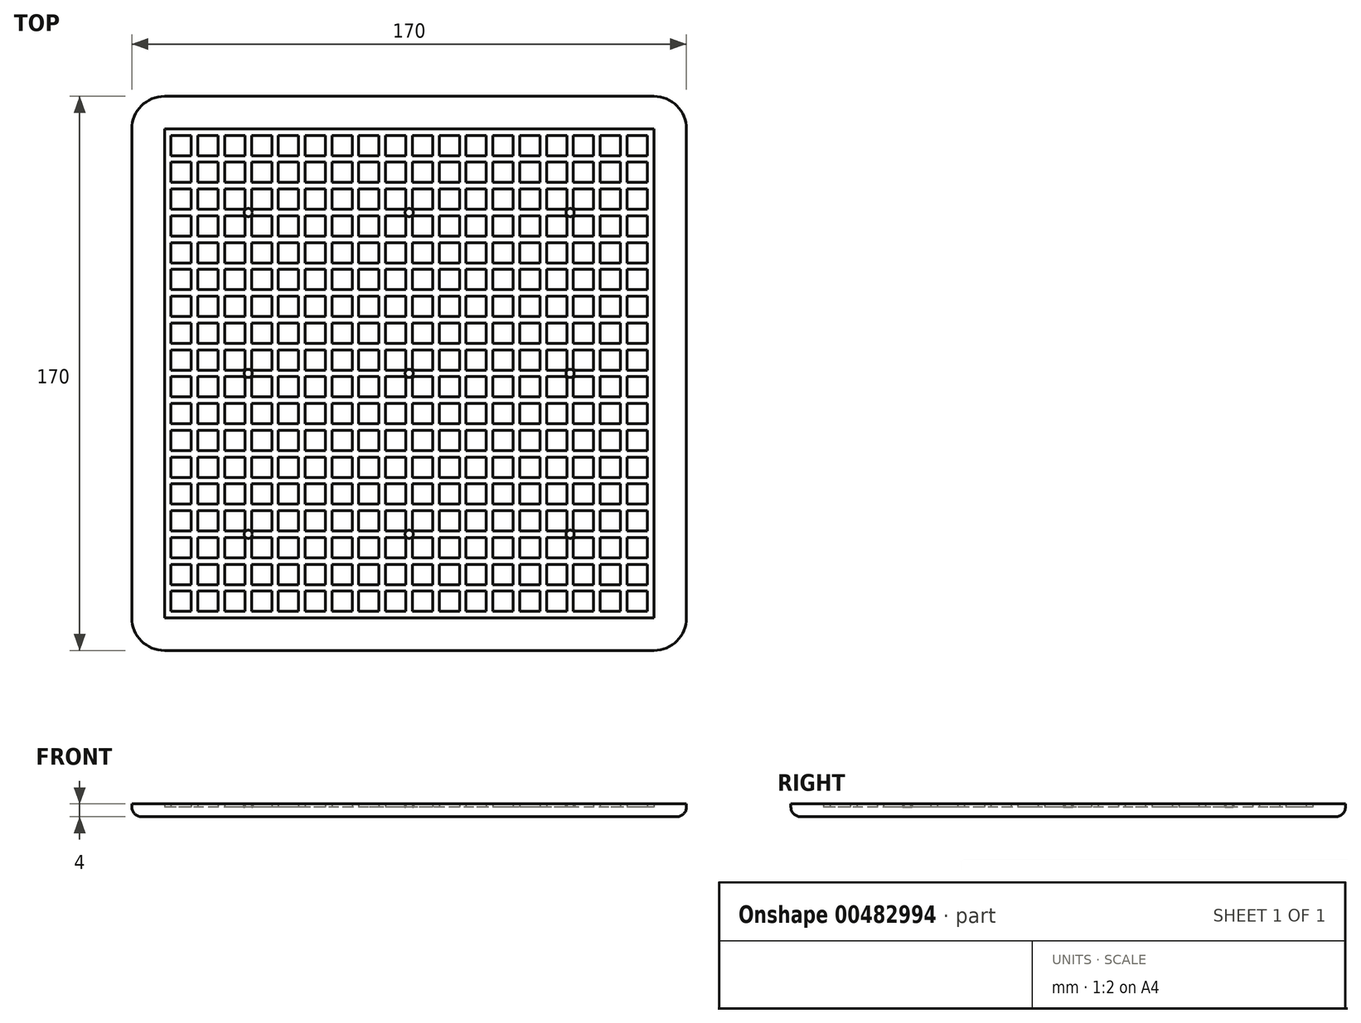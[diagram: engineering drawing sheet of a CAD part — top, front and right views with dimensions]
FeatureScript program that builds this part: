
annotation { "Feature Type Name" : "Feature", "Feature Type Description" : "" }
export const myFeature = defineFeature(function(context is Context, id is Id, definition is map)
    precondition{}
    {
        {
            var Q0;
            Q0=qCreatedBy(makeId("Top.planeOp"),FACE);
            var sketch = newSketch(context, id + "F0", { "sketchPlane" : qUnion([Q0])});
            skLineSegment(sketch, "E0.bottom", {"start": v(85, 85) * mm, "end": v(-85, 85) * mm});
            skLineSegment(sketch, "E0.top", {"start": v(85, -85) * mm, "end": v(-85, -85) * mm});
            skLineSegment(sketch, "E0.left", {"start": v(85, 85) * mm, "end": v(85, -85) * mm});
            skLineSegment(sketch, "E0.right", {"start": v(-85, 85) * mm, "end": v(-85, -85) * mm});
            skPoint(sketch, "E0.middle", {"position": v(0, 0) * mm});
            skSolve(sketch);
        }
        {
            var Q0;
            Q0=makeQuery(id+"F0.imprint","IMPRINT",FACE,{"disambiguationData":[TD([[makeQuery(id+"F0.imprint","IMPRINT",EDGE,{"derivedFrom":sQuery(id+"F0.wireOp",EDGE,"E0.bottom")}),1.0]])]});
            extrude(context, id + "F1", {"entities" : qUnion([Q0]), "depth" : 3 * mm});
        }
        {
            var Q0;
            Q0=makeQuery(id+"F1.opExtrude","CAP_FACE",FACE,{"disambiguationData":[OSD([sQuery(id+"F0.wireOp",EDGE,"E0.bottom"),sQuery(id+"F0.wireOp",EDGE,"E0.top"),sQuery(id+"F0.wireOp",EDGE,"E0.left"),sQuery(id+"F0.wireOp",EDGE,"E0.right")])],"isStart":false});
            var sketch = newSketch(context, id + "F2", { "sketchPlane" : qUnion([Q0])});
            skLineSegment(sketch, "E1.bottom", {"start": v(75, 75) * mm, "end": v(-75, 75) * mm});
            skLineSegment(sketch, "E1.top", {"start": v(75, -75) * mm, "end": v(-75, -75) * mm});
            skLineSegment(sketch, "E1.left", {"start": v(75, 75) * mm, "end": v(75, -75) * mm});
            skLineSegment(sketch, "E1.right", {"start": v(-75, 75) * mm, "end": v(-75, -75) * mm});
            skPoint(sketch, "E1.middle", {"position": v(0, 0) * mm});
            skSolve(sketch);
        }
        {
            var Q0;
            Q0=makeQuery(id+"F2.imprint","IMPRINT",FACE,{"disambiguationData":[TD([[makeQuery(id+"F2.imprint","IMPRINT",EDGE,{"derivedFrom":sQuery(id+"F2.wireOp",EDGE,"E1.bottom")}),-1.0]])]});
            extrude(context, id + "F3", {"entities" : qUnion([Q0]), "operationType" : NewBodyOperationType.ADD, "depth" : 1 * mm});
        }
        {
            var Q0;
            Q0=makeQuery(id+"F1.opExtrude","CAP_FACE",FACE,{"disambiguationData":[OSD([sQuery(id+"F0.wireOp",EDGE,"E0.bottom"),sQuery(id+"F0.wireOp",EDGE,"E0.top"),sQuery(id+"F0.wireOp",EDGE,"E0.left"),sQuery(id+"F0.wireOp",EDGE,"E0.right")])],"isStart":false});
            var sketch = newSketch(context, id + "F4", { "sketchPlane" : qUnion([Q0])});
            skLineSegment(sketch, "E2.bottom", {"start": v(-66.78, 73) * mm, "end": v(-73, 73) * mm});
            skLineSegment(sketch, "E2.top", {"start": v(-66.78, 66.78) * mm, "end": v(-73, 66.78) * mm});
            skLineSegment(sketch, "E2.left", {"start": v(-66.78, 73) * mm, "end": v(-66.78, 66.78) * mm});
            skLineSegment(sketch, "E2.right", {"start": v(-73, 73) * mm, "end": v(-73, 66.78) * mm});
            skPoint(sketch, "E2.middle", {"position": v(-69.89, 69.89) * mm});
            skLineSegment(sketch, "E3.0.1.0", {"start": v(-73, 64.78) * mm, "end": v(-73, 58.56) * mm});
            skLineSegment(sketch, "E3.0.1.1", {"start": v(-66.78, 58.56) * mm, "end": v(-73, 58.56) * mm});
            skLineSegment(sketch, "E3.0.1.2", {"start": v(-66.78, 64.78) * mm, "end": v(-66.78, 58.56) * mm});
            skLineSegment(sketch, "E3.0.1.3", {"start": v(-66.78, 64.78) * mm, "end": v(-73, 64.78) * mm});
            skLineSegment(sketch, "E3.0.2.0", {"start": v(-73, 56.56) * mm, "end": v(-73, 50.33) * mm});
            skLineSegment(sketch, "E3.0.2.1", {"start": v(-66.78, 50.33) * mm, "end": v(-73, 50.33) * mm});
            skLineSegment(sketch, "E3.0.2.2", {"start": v(-66.78, 56.56) * mm, "end": v(-66.78, 50.33) * mm});
            skLineSegment(sketch, "E3.0.2.3", {"start": v(-66.78, 56.56) * mm, "end": v(-73, 56.56) * mm});
            skLineSegment(sketch, "E3.0.3.0", {"start": v(-73, 48.33) * mm, "end": v(-73, 42.11) * mm});
            skLineSegment(sketch, "E3.0.3.1", {"start": v(-66.78, 42.11) * mm, "end": v(-73, 42.11) * mm});
            skLineSegment(sketch, "E3.0.3.2", {"start": v(-66.78, 48.33) * mm, "end": v(-66.78, 42.11) * mm});
            skLineSegment(sketch, "E3.0.3.3", {"start": v(-66.78, 48.33) * mm, "end": v(-73, 48.33) * mm});
            skLineSegment(sketch, "E3.0.4.0", {"start": v(-73, 40.11) * mm, "end": v(-73, 33.89) * mm});
            skLineSegment(sketch, "E3.0.4.1", {"start": v(-66.78, 33.89) * mm, "end": v(-73, 33.89) * mm});
            skLineSegment(sketch, "E3.0.4.2", {"start": v(-66.78, 40.11) * mm, "end": v(-66.78, 33.89) * mm});
            skLineSegment(sketch, "E3.0.4.3", {"start": v(-66.78, 40.11) * mm, "end": v(-73, 40.11) * mm});
            skLineSegment(sketch, "E3.0.5.0", {"start": v(-73, 31.89) * mm, "end": v(-73, 25.67) * mm});
            skLineSegment(sketch, "E3.0.5.1", {"start": v(-66.78, 25.67) * mm, "end": v(-73, 25.67) * mm});
            skLineSegment(sketch, "E3.0.5.2", {"start": v(-66.78, 31.89) * mm, "end": v(-66.78, 25.67) * mm});
            skLineSegment(sketch, "E3.0.5.3", {"start": v(-66.78, 31.89) * mm, "end": v(-73, 31.89) * mm});
            skLineSegment(sketch, "E3.0.6.0", {"start": v(-73, 23.67) * mm, "end": v(-73, 17.44) * mm});
            skLineSegment(sketch, "E3.0.6.1", {"start": v(-66.78, 17.44) * mm, "end": v(-73, 17.44) * mm});
            skLineSegment(sketch, "E3.0.6.2", {"start": v(-66.78, 23.67) * mm, "end": v(-66.78, 17.44) * mm});
            skLineSegment(sketch, "E3.0.6.3", {"start": v(-66.78, 23.67) * mm, "end": v(-73, 23.67) * mm});
            skLineSegment(sketch, "E3.0.7.0", {"start": v(-73, 15.44) * mm, "end": v(-73, 9.22) * mm});
            skLineSegment(sketch, "E3.0.7.1", {"start": v(-66.78, 9.22) * mm, "end": v(-73, 9.22) * mm});
            skLineSegment(sketch, "E3.0.7.2", {"start": v(-66.78, 15.44) * mm, "end": v(-66.78, 9.22) * mm});
            skLineSegment(sketch, "E3.0.7.3", {"start": v(-66.78, 15.44) * mm, "end": v(-73, 15.44) * mm});
            skLineSegment(sketch, "E3.0.8.0", {"start": v(-73, 7.22) * mm, "end": v(-73, 1) * mm});
            skLineSegment(sketch, "E3.0.8.1", {"start": v(-66.78, 1) * mm, "end": v(-73, 1) * mm});
            skLineSegment(sketch, "E3.0.8.2", {"start": v(-66.78, 7.22) * mm, "end": v(-66.78, 1) * mm});
            skLineSegment(sketch, "E3.0.8.3", {"start": v(-66.78, 7.22) * mm, "end": v(-73, 7.22) * mm});
            skLineSegment(sketch, "E3.0.9.0", {"start": v(-73, -1) * mm, "end": v(-73, -7.22) * mm});
            skLineSegment(sketch, "E3.0.9.1", {"start": v(-66.78, -7.22) * mm, "end": v(-73, -7.22) * mm});
            skLineSegment(sketch, "E3.0.9.2", {"start": v(-66.78, -1) * mm, "end": v(-66.78, -7.22) * mm});
            skLineSegment(sketch, "E3.0.9.3", {"start": v(-66.78, -1) * mm, "end": v(-73, -1) * mm});
            skLineSegment(sketch, "E3.0.10.0", {"start": v(-73, -9.22) * mm, "end": v(-73, -15.44) * mm});
            skLineSegment(sketch, "E3.0.10.1", {"start": v(-66.78, -15.44) * mm, "end": v(-73, -15.44) * mm});
            skLineSegment(sketch, "E3.0.10.2", {"start": v(-66.78, -9.22) * mm, "end": v(-66.78, -15.44) * mm});
            skLineSegment(sketch, "E3.0.10.3", {"start": v(-66.78, -9.22) * mm, "end": v(-73, -9.22) * mm});
            skLineSegment(sketch, "E3.0.11.0", {"start": v(-73, -17.44) * mm, "end": v(-73, -23.67) * mm});
            skLineSegment(sketch, "E3.0.11.1", {"start": v(-66.78, -23.67) * mm, "end": v(-73, -23.67) * mm});
            skLineSegment(sketch, "E3.0.11.2", {"start": v(-66.78, -17.44) * mm, "end": v(-66.78, -23.67) * mm});
            skLineSegment(sketch, "E3.0.11.3", {"start": v(-66.78, -17.44) * mm, "end": v(-73, -17.44) * mm});
            skLineSegment(sketch, "E3.0.12.0", {"start": v(-73, -25.67) * mm, "end": v(-73, -31.89) * mm});
            skLineSegment(sketch, "E3.0.12.1", {"start": v(-66.78, -31.89) * mm, "end": v(-73, -31.89) * mm});
            skLineSegment(sketch, "E3.0.12.2", {"start": v(-66.78, -25.67) * mm, "end": v(-66.78, -31.89) * mm});
            skLineSegment(sketch, "E3.0.12.3", {"start": v(-66.78, -25.67) * mm, "end": v(-73, -25.67) * mm});
            skLineSegment(sketch, "E3.0.13.0", {"start": v(-73, -33.89) * mm, "end": v(-73, -40.11) * mm});
            skLineSegment(sketch, "E3.0.13.1", {"start": v(-66.78, -40.11) * mm, "end": v(-73, -40.11) * mm});
            skLineSegment(sketch, "E3.0.13.2", {"start": v(-66.78, -33.89) * mm, "end": v(-66.78, -40.11) * mm});
            skLineSegment(sketch, "E3.0.13.3", {"start": v(-66.78, -33.89) * mm, "end": v(-73, -33.89) * mm});
            skLineSegment(sketch, "E3.0.14.0", {"start": v(-73, -42.11) * mm, "end": v(-73, -48.33) * mm});
            skLineSegment(sketch, "E3.0.14.1", {"start": v(-66.78, -48.33) * mm, "end": v(-73, -48.33) * mm});
            skLineSegment(sketch, "E3.0.14.2", {"start": v(-66.78, -42.11) * mm, "end": v(-66.78, -48.33) * mm});
            skLineSegment(sketch, "E3.0.14.3", {"start": v(-66.78, -42.11) * mm, "end": v(-73, -42.11) * mm});
            skLineSegment(sketch, "E3.0.15.0", {"start": v(-73, -50.33) * mm, "end": v(-73, -56.56) * mm});
            skLineSegment(sketch, "E3.0.15.1", {"start": v(-66.78, -56.56) * mm, "end": v(-73, -56.56) * mm});
            skLineSegment(sketch, "E3.0.15.2", {"start": v(-66.78, -50.33) * mm, "end": v(-66.78, -56.56) * mm});
            skLineSegment(sketch, "E3.0.15.3", {"start": v(-66.78, -50.33) * mm, "end": v(-73, -50.33) * mm});
            skLineSegment(sketch, "E3.0.16.0", {"start": v(-73, -58.56) * mm, "end": v(-73, -64.78) * mm});
            skLineSegment(sketch, "E3.0.16.1", {"start": v(-66.78, -64.78) * mm, "end": v(-73, -64.78) * mm});
            skLineSegment(sketch, "E3.0.16.2", {"start": v(-66.78, -58.56) * mm, "end": v(-66.78, -64.78) * mm});
            skLineSegment(sketch, "E3.0.16.3", {"start": v(-66.78, -58.56) * mm, "end": v(-73, -58.56) * mm});
            skLineSegment(sketch, "E3.0.17.0", {"start": v(-73, -66.78) * mm, "end": v(-73, -73) * mm});
            skLineSegment(sketch, "E3.0.17.1", {"start": v(-66.78, -73) * mm, "end": v(-73, -73) * mm});
            skLineSegment(sketch, "E3.0.17.2", {"start": v(-66.78, -66.78) * mm, "end": v(-66.78, -73) * mm});
            skLineSegment(sketch, "E3.0.17.3", {"start": v(-66.78, -66.78) * mm, "end": v(-73, -66.78) * mm});
            skLineSegment(sketch, "E3.1.0.0", {"start": v(-64.78, 73) * mm, "end": v(-64.78, 66.78) * mm});
            skLineSegment(sketch, "E3.1.0.1", {"start": v(-58.56, 66.78) * mm, "end": v(-64.78, 66.78) * mm});
            skLineSegment(sketch, "E3.1.0.2", {"start": v(-58.56, 73) * mm, "end": v(-58.56, 66.78) * mm});
            skLineSegment(sketch, "E3.1.0.3", {"start": v(-58.56, 73) * mm, "end": v(-64.78, 73) * mm});
            skLineSegment(sketch, "E3.1.1.0", {"start": v(-64.78, 64.78) * mm, "end": v(-64.78, 58.56) * mm});
            skLineSegment(sketch, "E3.1.1.1", {"start": v(-58.56, 58.56) * mm, "end": v(-64.78, 58.56) * mm});
            skLineSegment(sketch, "E3.1.1.2", {"start": v(-58.56, 64.78) * mm, "end": v(-58.56, 58.56) * mm});
            skLineSegment(sketch, "E3.1.1.3", {"start": v(-58.56, 64.78) * mm, "end": v(-64.78, 64.78) * mm});
            skLineSegment(sketch, "E3.1.2.0", {"start": v(-64.78, 56.56) * mm, "end": v(-64.78, 50.33) * mm});
            skLineSegment(sketch, "E3.1.2.1", {"start": v(-58.56, 50.33) * mm, "end": v(-64.78, 50.33) * mm});
            skLineSegment(sketch, "E3.1.2.2", {"start": v(-58.56, 56.56) * mm, "end": v(-58.56, 50.33) * mm});
            skLineSegment(sketch, "E3.1.2.3", {"start": v(-58.56, 56.56) * mm, "end": v(-64.78, 56.56) * mm});
            skLineSegment(sketch, "E3.1.3.0", {"start": v(-64.78, 48.33) * mm, "end": v(-64.78, 42.11) * mm});
            skLineSegment(sketch, "E3.1.3.1", {"start": v(-58.56, 42.11) * mm, "end": v(-64.78, 42.11) * mm});
            skLineSegment(sketch, "E3.1.3.2", {"start": v(-58.56, 48.33) * mm, "end": v(-58.56, 42.11) * mm});
            skLineSegment(sketch, "E3.1.3.3", {"start": v(-58.56, 48.33) * mm, "end": v(-64.78, 48.33) * mm});
            skLineSegment(sketch, "E3.1.4.0", {"start": v(-64.78, 40.11) * mm, "end": v(-64.78, 33.89) * mm});
            skLineSegment(sketch, "E3.1.4.1", {"start": v(-58.56, 33.89) * mm, "end": v(-64.78, 33.89) * mm});
            skLineSegment(sketch, "E3.1.4.2", {"start": v(-58.56, 40.11) * mm, "end": v(-58.56, 33.89) * mm});
            skLineSegment(sketch, "E3.1.4.3", {"start": v(-58.56, 40.11) * mm, "end": v(-64.78, 40.11) * mm});
            skLineSegment(sketch, "E3.1.5.0", {"start": v(-64.78, 31.89) * mm, "end": v(-64.78, 25.67) * mm});
            skLineSegment(sketch, "E3.1.5.1", {"start": v(-58.56, 25.67) * mm, "end": v(-64.78, 25.67) * mm});
            skLineSegment(sketch, "E3.1.5.2", {"start": v(-58.56, 31.89) * mm, "end": v(-58.56, 25.67) * mm});
            skLineSegment(sketch, "E3.1.5.3", {"start": v(-58.56, 31.89) * mm, "end": v(-64.78, 31.89) * mm});
            skLineSegment(sketch, "E3.1.6.0", {"start": v(-64.78, 23.67) * mm, "end": v(-64.78, 17.44) * mm});
            skLineSegment(sketch, "E3.1.6.1", {"start": v(-58.56, 17.44) * mm, "end": v(-64.78, 17.44) * mm});
            skLineSegment(sketch, "E3.1.6.2", {"start": v(-58.56, 23.67) * mm, "end": v(-58.56, 17.44) * mm});
            skLineSegment(sketch, "E3.1.6.3", {"start": v(-58.56, 23.67) * mm, "end": v(-64.78, 23.67) * mm});
            skLineSegment(sketch, "E3.1.7.0", {"start": v(-64.78, 15.44) * mm, "end": v(-64.78, 9.22) * mm});
            skLineSegment(sketch, "E3.1.7.1", {"start": v(-58.56, 9.22) * mm, "end": v(-64.78, 9.22) * mm});
            skLineSegment(sketch, "E3.1.7.2", {"start": v(-58.56, 15.44) * mm, "end": v(-58.56, 9.22) * mm});
            skLineSegment(sketch, "E3.1.7.3", {"start": v(-58.56, 15.44) * mm, "end": v(-64.78, 15.44) * mm});
            skLineSegment(sketch, "E3.1.8.0", {"start": v(-64.78, 7.22) * mm, "end": v(-64.78, 1) * mm});
            skLineSegment(sketch, "E3.1.8.1", {"start": v(-58.56, 1) * mm, "end": v(-64.78, 1) * mm});
            skLineSegment(sketch, "E3.1.8.2", {"start": v(-58.56, 7.22) * mm, "end": v(-58.56, 1) * mm});
            skLineSegment(sketch, "E3.1.8.3", {"start": v(-58.56, 7.22) * mm, "end": v(-64.78, 7.22) * mm});
            skLineSegment(sketch, "E3.1.9.0", {"start": v(-64.78, -1) * mm, "end": v(-64.78, -7.22) * mm});
            skLineSegment(sketch, "E3.1.9.1", {"start": v(-58.56, -7.22) * mm, "end": v(-64.78, -7.22) * mm});
            skLineSegment(sketch, "E3.1.9.2", {"start": v(-58.56, -1) * mm, "end": v(-58.56, -7.22) * mm});
            skLineSegment(sketch, "E3.1.9.3", {"start": v(-58.56, -1) * mm, "end": v(-64.78, -1) * mm});
            skLineSegment(sketch, "E3.1.10.0", {"start": v(-64.78, -9.22) * mm, "end": v(-64.78, -15.44) * mm});
            skLineSegment(sketch, "E3.1.10.1", {"start": v(-58.56, -15.44) * mm, "end": v(-64.78, -15.44) * mm});
            skLineSegment(sketch, "E3.1.10.2", {"start": v(-58.56, -9.22) * mm, "end": v(-58.56, -15.44) * mm});
            skLineSegment(sketch, "E3.1.10.3", {"start": v(-58.56, -9.22) * mm, "end": v(-64.78, -9.22) * mm});
            skLineSegment(sketch, "E3.1.11.0", {"start": v(-64.78, -17.44) * mm, "end": v(-64.78, -23.67) * mm});
            skLineSegment(sketch, "E3.1.11.1", {"start": v(-58.56, -23.67) * mm, "end": v(-64.78, -23.67) * mm});
            skLineSegment(sketch, "E3.1.11.2", {"start": v(-58.56, -17.44) * mm, "end": v(-58.56, -23.67) * mm});
            skLineSegment(sketch, "E3.1.11.3", {"start": v(-58.56, -17.44) * mm, "end": v(-64.78, -17.44) * mm});
            skLineSegment(sketch, "E3.1.12.0", {"start": v(-64.78, -25.67) * mm, "end": v(-64.78, -31.89) * mm});
            skLineSegment(sketch, "E3.1.12.1", {"start": v(-58.56, -31.89) * mm, "end": v(-64.78, -31.89) * mm});
            skLineSegment(sketch, "E3.1.12.2", {"start": v(-58.56, -25.67) * mm, "end": v(-58.56, -31.89) * mm});
            skLineSegment(sketch, "E3.1.12.3", {"start": v(-58.56, -25.67) * mm, "end": v(-64.78, -25.67) * mm});
            skLineSegment(sketch, "E3.1.13.0", {"start": v(-64.78, -33.89) * mm, "end": v(-64.78, -40.11) * mm});
            skLineSegment(sketch, "E3.1.13.1", {"start": v(-58.56, -40.11) * mm, "end": v(-64.78, -40.11) * mm});
            skLineSegment(sketch, "E3.1.13.2", {"start": v(-58.56, -33.89) * mm, "end": v(-58.56, -40.11) * mm});
            skLineSegment(sketch, "E3.1.13.3", {"start": v(-58.56, -33.89) * mm, "end": v(-64.78, -33.89) * mm});
            skLineSegment(sketch, "E3.1.14.0", {"start": v(-64.78, -42.11) * mm, "end": v(-64.78, -48.33) * mm});
            skLineSegment(sketch, "E3.1.14.1", {"start": v(-58.56, -48.33) * mm, "end": v(-64.78, -48.33) * mm});
            skLineSegment(sketch, "E3.1.14.2", {"start": v(-58.56, -42.11) * mm, "end": v(-58.56, -48.33) * mm});
            skLineSegment(sketch, "E3.1.14.3", {"start": v(-58.56, -42.11) * mm, "end": v(-64.78, -42.11) * mm});
            skLineSegment(sketch, "E3.1.15.0", {"start": v(-64.78, -50.33) * mm, "end": v(-64.78, -56.56) * mm});
            skLineSegment(sketch, "E3.1.15.1", {"start": v(-58.56, -56.56) * mm, "end": v(-64.78, -56.56) * mm});
            skLineSegment(sketch, "E3.1.15.2", {"start": v(-58.56, -50.33) * mm, "end": v(-58.56, -56.56) * mm});
            skLineSegment(sketch, "E3.1.15.3", {"start": v(-58.56, -50.33) * mm, "end": v(-64.78, -50.33) * mm});
            skLineSegment(sketch, "E3.1.16.0", {"start": v(-64.78, -58.56) * mm, "end": v(-64.78, -64.78) * mm});
            skLineSegment(sketch, "E3.1.16.1", {"start": v(-58.56, -64.78) * mm, "end": v(-64.78, -64.78) * mm});
            skLineSegment(sketch, "E3.1.16.2", {"start": v(-58.56, -58.56) * mm, "end": v(-58.56, -64.78) * mm});
            skLineSegment(sketch, "E3.1.16.3", {"start": v(-58.56, -58.56) * mm, "end": v(-64.78, -58.56) * mm});
            skLineSegment(sketch, "E3.1.17.0", {"start": v(-64.78, -66.78) * mm, "end": v(-64.78, -73) * mm});
            skLineSegment(sketch, "E3.1.17.1", {"start": v(-58.56, -73) * mm, "end": v(-64.78, -73) * mm});
            skLineSegment(sketch, "E3.1.17.2", {"start": v(-58.56, -66.78) * mm, "end": v(-58.56, -73) * mm});
            skLineSegment(sketch, "E3.1.17.3", {"start": v(-58.56, -66.78) * mm, "end": v(-64.78, -66.78) * mm});
            skLineSegment(sketch, "E3.2.0.0", {"start": v(-56.56, 73) * mm, "end": v(-56.56, 66.78) * mm});
            skLineSegment(sketch, "E3.2.0.1", {"start": v(-50.33, 66.78) * mm, "end": v(-56.56, 66.78) * mm});
            skLineSegment(sketch, "E3.2.0.2", {"start": v(-50.33, 73) * mm, "end": v(-50.33, 66.78) * mm});
            skLineSegment(sketch, "E3.2.0.3", {"start": v(-50.33, 73) * mm, "end": v(-56.56, 73) * mm});
            skLineSegment(sketch, "E3.2.1.0", {"start": v(-56.56, 64.78) * mm, "end": v(-56.56, 58.56) * mm});
            skLineSegment(sketch, "E3.2.1.1", {"start": v(-50.33, 58.56) * mm, "end": v(-56.56, 58.56) * mm});
            skLineSegment(sketch, "E3.2.1.2", {"start": v(-50.33, 64.78) * mm, "end": v(-50.33, 58.56) * mm});
            skLineSegment(sketch, "E3.2.1.3", {"start": v(-50.33, 64.78) * mm, "end": v(-56.56, 64.78) * mm});
            skLineSegment(sketch, "E3.2.2.0", {"start": v(-56.56, 56.56) * mm, "end": v(-56.56, 50.33) * mm});
            skLineSegment(sketch, "E3.2.2.1", {"start": v(-50.33, 50.33) * mm, "end": v(-56.56, 50.33) * mm});
            skLineSegment(sketch, "E3.2.2.2", {"start": v(-50.33, 56.56) * mm, "end": v(-50.33, 50.33) * mm});
            skLineSegment(sketch, "E3.2.2.3", {"start": v(-50.33, 56.56) * mm, "end": v(-56.56, 56.56) * mm});
            skLineSegment(sketch, "E3.2.3.0", {"start": v(-56.56, 48.33) * mm, "end": v(-56.56, 42.11) * mm});
            skLineSegment(sketch, "E3.2.3.1", {"start": v(-50.33, 42.11) * mm, "end": v(-56.56, 42.11) * mm});
            skLineSegment(sketch, "E3.2.3.2", {"start": v(-50.33, 48.33) * mm, "end": v(-50.33, 42.11) * mm});
            skLineSegment(sketch, "E3.2.3.3", {"start": v(-50.33, 48.33) * mm, "end": v(-56.56, 48.33) * mm});
            skLineSegment(sketch, "E3.2.4.0", {"start": v(-56.56, 40.11) * mm, "end": v(-56.56, 33.89) * mm});
            skLineSegment(sketch, "E3.2.4.1", {"start": v(-50.33, 33.89) * mm, "end": v(-56.56, 33.89) * mm});
            skLineSegment(sketch, "E3.2.4.2", {"start": v(-50.33, 40.11) * mm, "end": v(-50.33, 33.89) * mm});
            skLineSegment(sketch, "E3.2.4.3", {"start": v(-50.33, 40.11) * mm, "end": v(-56.56, 40.11) * mm});
            skLineSegment(sketch, "E3.2.5.0", {"start": v(-56.56, 31.89) * mm, "end": v(-56.56, 25.67) * mm});
            skLineSegment(sketch, "E3.2.5.1", {"start": v(-50.33, 25.67) * mm, "end": v(-56.56, 25.67) * mm});
            skLineSegment(sketch, "E3.2.5.2", {"start": v(-50.33, 31.89) * mm, "end": v(-50.33, 25.67) * mm});
            skLineSegment(sketch, "E3.2.5.3", {"start": v(-50.33, 31.89) * mm, "end": v(-56.56, 31.89) * mm});
            skLineSegment(sketch, "E3.2.6.0", {"start": v(-56.56, 23.67) * mm, "end": v(-56.56, 17.44) * mm});
            skLineSegment(sketch, "E3.2.6.1", {"start": v(-50.33, 17.44) * mm, "end": v(-56.56, 17.44) * mm});
            skLineSegment(sketch, "E3.2.6.2", {"start": v(-50.33, 23.67) * mm, "end": v(-50.33, 17.44) * mm});
            skLineSegment(sketch, "E3.2.6.3", {"start": v(-50.33, 23.67) * mm, "end": v(-56.56, 23.67) * mm});
            skLineSegment(sketch, "E3.2.7.0", {"start": v(-56.56, 15.44) * mm, "end": v(-56.56, 9.22) * mm});
            skLineSegment(sketch, "E3.2.7.1", {"start": v(-50.33, 9.22) * mm, "end": v(-56.56, 9.22) * mm});
            skLineSegment(sketch, "E3.2.7.2", {"start": v(-50.33, 15.44) * mm, "end": v(-50.33, 9.22) * mm});
            skLineSegment(sketch, "E3.2.7.3", {"start": v(-50.33, 15.44) * mm, "end": v(-56.56, 15.44) * mm});
            skLineSegment(sketch, "E3.2.8.0", {"start": v(-56.56, 7.22) * mm, "end": v(-56.56, 1) * mm});
            skLineSegment(sketch, "E3.2.8.1", {"start": v(-50.33, 1) * mm, "end": v(-56.56, 1) * mm});
            skLineSegment(sketch, "E3.2.8.2", {"start": v(-50.33, 7.22) * mm, "end": v(-50.33, 1) * mm});
            skLineSegment(sketch, "E3.2.8.3", {"start": v(-50.33, 7.22) * mm, "end": v(-56.56, 7.22) * mm});
            skLineSegment(sketch, "E3.2.9.0", {"start": v(-56.56, -1) * mm, "end": v(-56.56, -7.22) * mm});
            skLineSegment(sketch, "E3.2.9.1", {"start": v(-50.33, -7.22) * mm, "end": v(-56.56, -7.22) * mm});
            skLineSegment(sketch, "E3.2.9.2", {"start": v(-50.33, -1) * mm, "end": v(-50.33, -7.22) * mm});
            skLineSegment(sketch, "E3.2.9.3", {"start": v(-50.33, -1) * mm, "end": v(-56.56, -1) * mm});
            skLineSegment(sketch, "E3.2.10.0", {"start": v(-56.56, -9.22) * mm, "end": v(-56.56, -15.44) * mm});
            skLineSegment(sketch, "E3.2.10.1", {"start": v(-50.33, -15.44) * mm, "end": v(-56.56, -15.44) * mm});
            skLineSegment(sketch, "E3.2.10.2", {"start": v(-50.33, -9.22) * mm, "end": v(-50.33, -15.44) * mm});
            skLineSegment(sketch, "E3.2.10.3", {"start": v(-50.33, -9.22) * mm, "end": v(-56.56, -9.22) * mm});
            skLineSegment(sketch, "E3.2.11.0", {"start": v(-56.56, -17.44) * mm, "end": v(-56.56, -23.67) * mm});
            skLineSegment(sketch, "E3.2.11.1", {"start": v(-50.33, -23.67) * mm, "end": v(-56.56, -23.67) * mm});
            skLineSegment(sketch, "E3.2.11.2", {"start": v(-50.33, -17.44) * mm, "end": v(-50.33, -23.67) * mm});
            skLineSegment(sketch, "E3.2.11.3", {"start": v(-50.33, -17.44) * mm, "end": v(-56.56, -17.44) * mm});
            skLineSegment(sketch, "E3.2.12.0", {"start": v(-56.56, -25.67) * mm, "end": v(-56.56, -31.89) * mm});
            skLineSegment(sketch, "E3.2.12.1", {"start": v(-50.33, -31.89) * mm, "end": v(-56.56, -31.89) * mm});
            skLineSegment(sketch, "E3.2.12.2", {"start": v(-50.33, -25.67) * mm, "end": v(-50.33, -31.89) * mm});
            skLineSegment(sketch, "E3.2.12.3", {"start": v(-50.33, -25.67) * mm, "end": v(-56.56, -25.67) * mm});
            skLineSegment(sketch, "E3.2.13.0", {"start": v(-56.56, -33.89) * mm, "end": v(-56.56, -40.11) * mm});
            skLineSegment(sketch, "E3.2.13.1", {"start": v(-50.33, -40.11) * mm, "end": v(-56.56, -40.11) * mm});
            skLineSegment(sketch, "E3.2.13.2", {"start": v(-50.33, -33.89) * mm, "end": v(-50.33, -40.11) * mm});
            skLineSegment(sketch, "E3.2.13.3", {"start": v(-50.33, -33.89) * mm, "end": v(-56.56, -33.89) * mm});
            skLineSegment(sketch, "E3.2.14.0", {"start": v(-56.56, -42.11) * mm, "end": v(-56.56, -48.33) * mm});
            skLineSegment(sketch, "E3.2.14.1", {"start": v(-50.33, -48.33) * mm, "end": v(-56.56, -48.33) * mm});
            skLineSegment(sketch, "E3.2.14.2", {"start": v(-50.33, -42.11) * mm, "end": v(-50.33, -48.33) * mm});
            skLineSegment(sketch, "E3.2.14.3", {"start": v(-50.33, -42.11) * mm, "end": v(-56.56, -42.11) * mm});
            skLineSegment(sketch, "E3.2.15.0", {"start": v(-56.56, -50.33) * mm, "end": v(-56.56, -56.56) * mm});
            skLineSegment(sketch, "E3.2.15.1", {"start": v(-50.33, -56.56) * mm, "end": v(-56.56, -56.56) * mm});
            skLineSegment(sketch, "E3.2.15.2", {"start": v(-50.33, -50.33) * mm, "end": v(-50.33, -56.56) * mm});
            skLineSegment(sketch, "E3.2.15.3", {"start": v(-50.33, -50.33) * mm, "end": v(-56.56, -50.33) * mm});
            skLineSegment(sketch, "E3.2.16.0", {"start": v(-56.56, -58.56) * mm, "end": v(-56.56, -64.78) * mm});
            skLineSegment(sketch, "E3.2.16.1", {"start": v(-50.33, -64.78) * mm, "end": v(-56.56, -64.78) * mm});
            skLineSegment(sketch, "E3.2.16.2", {"start": v(-50.33, -58.56) * mm, "end": v(-50.33, -64.78) * mm});
            skLineSegment(sketch, "E3.2.16.3", {"start": v(-50.33, -58.56) * mm, "end": v(-56.56, -58.56) * mm});
            skLineSegment(sketch, "E3.2.17.0", {"start": v(-56.56, -66.78) * mm, "end": v(-56.56, -73) * mm});
            skLineSegment(sketch, "E3.2.17.1", {"start": v(-50.33, -73) * mm, "end": v(-56.56, -73) * mm});
            skLineSegment(sketch, "E3.2.17.2", {"start": v(-50.33, -66.78) * mm, "end": v(-50.33, -73) * mm});
            skLineSegment(sketch, "E3.2.17.3", {"start": v(-50.33, -66.78) * mm, "end": v(-56.56, -66.78) * mm});
            skLineSegment(sketch, "E3.3.0.0", {"start": v(-48.33, 73) * mm, "end": v(-48.33, 66.78) * mm});
            skLineSegment(sketch, "E3.3.0.1", {"start": v(-42.11, 66.78) * mm, "end": v(-48.33, 66.78) * mm});
            skLineSegment(sketch, "E3.3.0.2", {"start": v(-42.11, 73) * mm, "end": v(-42.11, 66.78) * mm});
            skLineSegment(sketch, "E3.3.0.3", {"start": v(-42.11, 73) * mm, "end": v(-48.33, 73) * mm});
            skLineSegment(sketch, "E3.3.1.0", {"start": v(-48.33, 64.78) * mm, "end": v(-48.33, 58.56) * mm});
            skLineSegment(sketch, "E3.3.1.1", {"start": v(-42.11, 58.56) * mm, "end": v(-48.33, 58.56) * mm});
            skLineSegment(sketch, "E3.3.1.2", {"start": v(-42.11, 64.78) * mm, "end": v(-42.11, 58.56) * mm});
            skLineSegment(sketch, "E3.3.1.3", {"start": v(-42.11, 64.78) * mm, "end": v(-48.33, 64.78) * mm});
            skLineSegment(sketch, "E3.3.2.0", {"start": v(-48.33, 56.56) * mm, "end": v(-48.33, 50.33) * mm});
            skLineSegment(sketch, "E3.3.2.1", {"start": v(-42.11, 50.33) * mm, "end": v(-48.33, 50.33) * mm});
            skLineSegment(sketch, "E3.3.2.2", {"start": v(-42.11, 56.56) * mm, "end": v(-42.11, 50.33) * mm});
            skLineSegment(sketch, "E3.3.2.3", {"start": v(-42.11, 56.56) * mm, "end": v(-48.33, 56.56) * mm});
            skLineSegment(sketch, "E3.3.3.0", {"start": v(-48.33, 48.33) * mm, "end": v(-48.33, 42.11) * mm});
            skLineSegment(sketch, "E3.3.3.1", {"start": v(-42.11, 42.11) * mm, "end": v(-48.33, 42.11) * mm});
            skLineSegment(sketch, "E3.3.3.2", {"start": v(-42.11, 48.33) * mm, "end": v(-42.11, 42.11) * mm});
            skLineSegment(sketch, "E3.3.3.3", {"start": v(-42.11, 48.33) * mm, "end": v(-48.33, 48.33) * mm});
            skLineSegment(sketch, "E3.3.4.0", {"start": v(-48.33, 40.11) * mm, "end": v(-48.33, 33.89) * mm});
            skLineSegment(sketch, "E3.3.4.1", {"start": v(-42.11, 33.89) * mm, "end": v(-48.33, 33.89) * mm});
            skLineSegment(sketch, "E3.3.4.2", {"start": v(-42.11, 40.11) * mm, "end": v(-42.11, 33.89) * mm});
            skLineSegment(sketch, "E3.3.4.3", {"start": v(-42.11, 40.11) * mm, "end": v(-48.33, 40.11) * mm});
            skLineSegment(sketch, "E3.3.5.0", {"start": v(-48.33, 31.89) * mm, "end": v(-48.33, 25.67) * mm});
            skLineSegment(sketch, "E3.3.5.1", {"start": v(-42.11, 25.67) * mm, "end": v(-48.33, 25.67) * mm});
            skLineSegment(sketch, "E3.3.5.2", {"start": v(-42.11, 31.89) * mm, "end": v(-42.11, 25.67) * mm});
            skLineSegment(sketch, "E3.3.5.3", {"start": v(-42.11, 31.89) * mm, "end": v(-48.33, 31.89) * mm});
            skLineSegment(sketch, "E3.3.6.0", {"start": v(-48.33, 23.67) * mm, "end": v(-48.33, 17.44) * mm});
            skLineSegment(sketch, "E3.3.6.1", {"start": v(-42.11, 17.44) * mm, "end": v(-48.33, 17.44) * mm});
            skLineSegment(sketch, "E3.3.6.2", {"start": v(-42.11, 23.67) * mm, "end": v(-42.11, 17.44) * mm});
            skLineSegment(sketch, "E3.3.6.3", {"start": v(-42.11, 23.67) * mm, "end": v(-48.33, 23.67) * mm});
            skLineSegment(sketch, "E3.3.7.0", {"start": v(-48.33, 15.44) * mm, "end": v(-48.33, 9.22) * mm});
            skLineSegment(sketch, "E3.3.7.1", {"start": v(-42.11, 9.22) * mm, "end": v(-48.33, 9.22) * mm});
            skLineSegment(sketch, "E3.3.7.2", {"start": v(-42.11, 15.44) * mm, "end": v(-42.11, 9.22) * mm});
            skLineSegment(sketch, "E3.3.7.3", {"start": v(-42.11, 15.44) * mm, "end": v(-48.33, 15.44) * mm});
            skLineSegment(sketch, "E3.3.8.0", {"start": v(-48.33, 7.22) * mm, "end": v(-48.33, 1) * mm});
            skLineSegment(sketch, "E3.3.8.1", {"start": v(-42.11, 1) * mm, "end": v(-48.33, 1) * mm});
            skLineSegment(sketch, "E3.3.8.2", {"start": v(-42.11, 7.22) * mm, "end": v(-42.11, 1) * mm});
            skLineSegment(sketch, "E3.3.8.3", {"start": v(-42.11, 7.22) * mm, "end": v(-48.33, 7.22) * mm});
            skLineSegment(sketch, "E3.3.9.0", {"start": v(-48.33, -1) * mm, "end": v(-48.33, -7.22) * mm});
            skLineSegment(sketch, "E3.3.9.1", {"start": v(-42.11, -7.22) * mm, "end": v(-48.33, -7.22) * mm});
            skLineSegment(sketch, "E3.3.9.2", {"start": v(-42.11, -1) * mm, "end": v(-42.11, -7.22) * mm});
            skLineSegment(sketch, "E3.3.9.3", {"start": v(-42.11, -1) * mm, "end": v(-48.33, -1) * mm});
            skLineSegment(sketch, "E3.3.10.0", {"start": v(-48.33, -9.22) * mm, "end": v(-48.33, -15.44) * mm});
            skLineSegment(sketch, "E3.3.10.1", {"start": v(-42.11, -15.44) * mm, "end": v(-48.33, -15.44) * mm});
            skLineSegment(sketch, "E3.3.10.2", {"start": v(-42.11, -9.22) * mm, "end": v(-42.11, -15.44) * mm});
            skLineSegment(sketch, "E3.3.10.3", {"start": v(-42.11, -9.22) * mm, "end": v(-48.33, -9.22) * mm});
            skLineSegment(sketch, "E3.3.11.0", {"start": v(-48.33, -17.44) * mm, "end": v(-48.33, -23.67) * mm});
            skLineSegment(sketch, "E3.3.11.1", {"start": v(-42.11, -23.67) * mm, "end": v(-48.33, -23.67) * mm});
            skLineSegment(sketch, "E3.3.11.2", {"start": v(-42.11, -17.44) * mm, "end": v(-42.11, -23.67) * mm});
            skLineSegment(sketch, "E3.3.11.3", {"start": v(-42.11, -17.44) * mm, "end": v(-48.33, -17.44) * mm});
            skLineSegment(sketch, "E3.3.12.0", {"start": v(-48.33, -25.67) * mm, "end": v(-48.33, -31.89) * mm});
            skLineSegment(sketch, "E3.3.12.1", {"start": v(-42.11, -31.89) * mm, "end": v(-48.33, -31.89) * mm});
            skLineSegment(sketch, "E3.3.12.2", {"start": v(-42.11, -25.67) * mm, "end": v(-42.11, -31.89) * mm});
            skLineSegment(sketch, "E3.3.12.3", {"start": v(-42.11, -25.67) * mm, "end": v(-48.33, -25.67) * mm});
            skLineSegment(sketch, "E3.3.13.0", {"start": v(-48.33, -33.89) * mm, "end": v(-48.33, -40.11) * mm});
            skLineSegment(sketch, "E3.3.13.1", {"start": v(-42.11, -40.11) * mm, "end": v(-48.33, -40.11) * mm});
            skLineSegment(sketch, "E3.3.13.2", {"start": v(-42.11, -33.89) * mm, "end": v(-42.11, -40.11) * mm});
            skLineSegment(sketch, "E3.3.13.3", {"start": v(-42.11, -33.89) * mm, "end": v(-48.33, -33.89) * mm});
            skLineSegment(sketch, "E3.3.14.0", {"start": v(-48.33, -42.11) * mm, "end": v(-48.33, -48.33) * mm});
            skLineSegment(sketch, "E3.3.14.1", {"start": v(-42.11, -48.33) * mm, "end": v(-48.33, -48.33) * mm});
            skLineSegment(sketch, "E3.3.14.2", {"start": v(-42.11, -42.11) * mm, "end": v(-42.11, -48.33) * mm});
            skLineSegment(sketch, "E3.3.14.3", {"start": v(-42.11, -42.11) * mm, "end": v(-48.33, -42.11) * mm});
            skLineSegment(sketch, "E3.3.15.0", {"start": v(-48.33, -50.33) * mm, "end": v(-48.33, -56.56) * mm});
            skLineSegment(sketch, "E3.3.15.1", {"start": v(-42.11, -56.56) * mm, "end": v(-48.33, -56.56) * mm});
            skLineSegment(sketch, "E3.3.15.2", {"start": v(-42.11, -50.33) * mm, "end": v(-42.11, -56.56) * mm});
            skLineSegment(sketch, "E3.3.15.3", {"start": v(-42.11, -50.33) * mm, "end": v(-48.33, -50.33) * mm});
            skLineSegment(sketch, "E3.3.16.0", {"start": v(-48.33, -58.56) * mm, "end": v(-48.33, -64.78) * mm});
            skLineSegment(sketch, "E3.3.16.1", {"start": v(-42.11, -64.78) * mm, "end": v(-48.33, -64.78) * mm});
            skLineSegment(sketch, "E3.3.16.2", {"start": v(-42.11, -58.56) * mm, "end": v(-42.11, -64.78) * mm});
            skLineSegment(sketch, "E3.3.16.3", {"start": v(-42.11, -58.56) * mm, "end": v(-48.33, -58.56) * mm});
            skLineSegment(sketch, "E3.3.17.0", {"start": v(-48.33, -66.78) * mm, "end": v(-48.33, -73) * mm});
            skLineSegment(sketch, "E3.3.17.1", {"start": v(-42.11, -73) * mm, "end": v(-48.33, -73) * mm});
            skLineSegment(sketch, "E3.3.17.2", {"start": v(-42.11, -66.78) * mm, "end": v(-42.11, -73) * mm});
            skLineSegment(sketch, "E3.3.17.3", {"start": v(-42.11, -66.78) * mm, "end": v(-48.33, -66.78) * mm});
            skLineSegment(sketch, "E3.4.0.0", {"start": v(-40.11, 73) * mm, "end": v(-40.11, 66.78) * mm});
            skLineSegment(sketch, "E3.4.0.1", {"start": v(-33.89, 66.78) * mm, "end": v(-40.11, 66.78) * mm});
            skLineSegment(sketch, "E3.4.0.2", {"start": v(-33.89, 73) * mm, "end": v(-33.89, 66.78) * mm});
            skLineSegment(sketch, "E3.4.0.3", {"start": v(-33.89, 73) * mm, "end": v(-40.11, 73) * mm});
            skLineSegment(sketch, "E3.4.1.0", {"start": v(-40.11, 64.78) * mm, "end": v(-40.11, 58.56) * mm});
            skLineSegment(sketch, "E3.4.1.1", {"start": v(-33.89, 58.56) * mm, "end": v(-40.11, 58.56) * mm});
            skLineSegment(sketch, "E3.4.1.2", {"start": v(-33.89, 64.78) * mm, "end": v(-33.89, 58.56) * mm});
            skLineSegment(sketch, "E3.4.1.3", {"start": v(-33.89, 64.78) * mm, "end": v(-40.11, 64.78) * mm});
            skLineSegment(sketch, "E3.4.2.0", {"start": v(-40.11, 56.56) * mm, "end": v(-40.11, 50.33) * mm});
            skLineSegment(sketch, "E3.4.2.1", {"start": v(-33.89, 50.33) * mm, "end": v(-40.11, 50.33) * mm});
            skLineSegment(sketch, "E3.4.2.2", {"start": v(-33.89, 56.56) * mm, "end": v(-33.89, 50.33) * mm});
            skLineSegment(sketch, "E3.4.2.3", {"start": v(-33.89, 56.56) * mm, "end": v(-40.11, 56.56) * mm});
            skLineSegment(sketch, "E3.4.3.0", {"start": v(-40.11, 48.33) * mm, "end": v(-40.11, 42.11) * mm});
            skLineSegment(sketch, "E3.4.3.1", {"start": v(-33.89, 42.11) * mm, "end": v(-40.11, 42.11) * mm});
            skLineSegment(sketch, "E3.4.3.2", {"start": v(-33.89, 48.33) * mm, "end": v(-33.89, 42.11) * mm});
            skLineSegment(sketch, "E3.4.3.3", {"start": v(-33.89, 48.33) * mm, "end": v(-40.11, 48.33) * mm});
            skLineSegment(sketch, "E3.4.4.0", {"start": v(-40.11, 40.11) * mm, "end": v(-40.11, 33.89) * mm});
            skLineSegment(sketch, "E3.4.4.1", {"start": v(-33.89, 33.89) * mm, "end": v(-40.11, 33.89) * mm});
            skLineSegment(sketch, "E3.4.4.2", {"start": v(-33.89, 40.11) * mm, "end": v(-33.89, 33.89) * mm});
            skLineSegment(sketch, "E3.4.4.3", {"start": v(-33.89, 40.11) * mm, "end": v(-40.11, 40.11) * mm});
            skLineSegment(sketch, "E3.4.5.0", {"start": v(-40.11, 31.89) * mm, "end": v(-40.11, 25.67) * mm});
            skLineSegment(sketch, "E3.4.5.1", {"start": v(-33.89, 25.67) * mm, "end": v(-40.11, 25.67) * mm});
            skLineSegment(sketch, "E3.4.5.2", {"start": v(-33.89, 31.89) * mm, "end": v(-33.89, 25.67) * mm});
            skLineSegment(sketch, "E3.4.5.3", {"start": v(-33.89, 31.89) * mm, "end": v(-40.11, 31.89) * mm});
            skLineSegment(sketch, "E3.4.6.0", {"start": v(-40.11, 23.67) * mm, "end": v(-40.11, 17.44) * mm});
            skLineSegment(sketch, "E3.4.6.1", {"start": v(-33.89, 17.44) * mm, "end": v(-40.11, 17.44) * mm});
            skLineSegment(sketch, "E3.4.6.2", {"start": v(-33.89, 23.67) * mm, "end": v(-33.89, 17.44) * mm});
            skLineSegment(sketch, "E3.4.6.3", {"start": v(-33.89, 23.67) * mm, "end": v(-40.11, 23.67) * mm});
            skLineSegment(sketch, "E3.4.7.0", {"start": v(-40.11, 15.44) * mm, "end": v(-40.11, 9.22) * mm});
            skLineSegment(sketch, "E3.4.7.1", {"start": v(-33.89, 9.22) * mm, "end": v(-40.11, 9.22) * mm});
            skLineSegment(sketch, "E3.4.7.2", {"start": v(-33.89, 15.44) * mm, "end": v(-33.89, 9.22) * mm});
            skLineSegment(sketch, "E3.4.7.3", {"start": v(-33.89, 15.44) * mm, "end": v(-40.11, 15.44) * mm});
            skLineSegment(sketch, "E3.4.8.0", {"start": v(-40.11, 7.22) * mm, "end": v(-40.11, 1) * mm});
            skLineSegment(sketch, "E3.4.8.1", {"start": v(-33.89, 1) * mm, "end": v(-40.11, 1) * mm});
            skLineSegment(sketch, "E3.4.8.2", {"start": v(-33.89, 7.22) * mm, "end": v(-33.89, 1) * mm});
            skLineSegment(sketch, "E3.4.8.3", {"start": v(-33.89, 7.22) * mm, "end": v(-40.11, 7.22) * mm});
            skLineSegment(sketch, "E3.4.9.0", {"start": v(-40.11, -1) * mm, "end": v(-40.11, -7.22) * mm});
            skLineSegment(sketch, "E3.4.9.1", {"start": v(-33.89, -7.22) * mm, "end": v(-40.11, -7.22) * mm});
            skLineSegment(sketch, "E3.4.9.2", {"start": v(-33.89, -1) * mm, "end": v(-33.89, -7.22) * mm});
            skLineSegment(sketch, "E3.4.9.3", {"start": v(-33.89, -1) * mm, "end": v(-40.11, -1) * mm});
            skLineSegment(sketch, "E3.4.10.0", {"start": v(-40.11, -9.22) * mm, "end": v(-40.11, -15.44) * mm});
            skLineSegment(sketch, "E3.4.10.1", {"start": v(-33.89, -15.44) * mm, "end": v(-40.11, -15.44) * mm});
            skLineSegment(sketch, "E3.4.10.2", {"start": v(-33.89, -9.22) * mm, "end": v(-33.89, -15.44) * mm});
            skLineSegment(sketch, "E3.4.10.3", {"start": v(-33.89, -9.22) * mm, "end": v(-40.11, -9.22) * mm});
            skLineSegment(sketch, "E3.4.11.0", {"start": v(-40.11, -17.44) * mm, "end": v(-40.11, -23.67) * mm});
            skLineSegment(sketch, "E3.4.11.1", {"start": v(-33.89, -23.67) * mm, "end": v(-40.11, -23.67) * mm});
            skLineSegment(sketch, "E3.4.11.2", {"start": v(-33.89, -17.44) * mm, "end": v(-33.89, -23.67) * mm});
            skLineSegment(sketch, "E3.4.11.3", {"start": v(-33.89, -17.44) * mm, "end": v(-40.11, -17.44) * mm});
            skLineSegment(sketch, "E3.4.12.0", {"start": v(-40.11, -25.67) * mm, "end": v(-40.11, -31.89) * mm});
            skLineSegment(sketch, "E3.4.12.1", {"start": v(-33.89, -31.89) * mm, "end": v(-40.11, -31.89) * mm});
            skLineSegment(sketch, "E3.4.12.2", {"start": v(-33.89, -25.67) * mm, "end": v(-33.89, -31.89) * mm});
            skLineSegment(sketch, "E3.4.12.3", {"start": v(-33.89, -25.67) * mm, "end": v(-40.11, -25.67) * mm});
            skLineSegment(sketch, "E3.4.13.0", {"start": v(-40.11, -33.89) * mm, "end": v(-40.11, -40.11) * mm});
            skLineSegment(sketch, "E3.4.13.1", {"start": v(-33.89, -40.11) * mm, "end": v(-40.11, -40.11) * mm});
            skLineSegment(sketch, "E3.4.13.2", {"start": v(-33.89, -33.89) * mm, "end": v(-33.89, -40.11) * mm});
            skLineSegment(sketch, "E3.4.13.3", {"start": v(-33.89, -33.89) * mm, "end": v(-40.11, -33.89) * mm});
            skLineSegment(sketch, "E3.4.14.0", {"start": v(-40.11, -42.11) * mm, "end": v(-40.11, -48.33) * mm});
            skLineSegment(sketch, "E3.4.14.1", {"start": v(-33.89, -48.33) * mm, "end": v(-40.11, -48.33) * mm});
            skLineSegment(sketch, "E3.4.14.2", {"start": v(-33.89, -42.11) * mm, "end": v(-33.89, -48.33) * mm});
            skLineSegment(sketch, "E3.4.14.3", {"start": v(-33.89, -42.11) * mm, "end": v(-40.11, -42.11) * mm});
            skLineSegment(sketch, "E3.4.15.0", {"start": v(-40.11, -50.33) * mm, "end": v(-40.11, -56.56) * mm});
            skLineSegment(sketch, "E3.4.15.1", {"start": v(-33.89, -56.56) * mm, "end": v(-40.11, -56.56) * mm});
            skLineSegment(sketch, "E3.4.15.2", {"start": v(-33.89, -50.33) * mm, "end": v(-33.89, -56.56) * mm});
            skLineSegment(sketch, "E3.4.15.3", {"start": v(-33.89, -50.33) * mm, "end": v(-40.11, -50.33) * mm});
            skLineSegment(sketch, "E3.4.16.0", {"start": v(-40.11, -58.56) * mm, "end": v(-40.11, -64.78) * mm});
            skLineSegment(sketch, "E3.4.16.1", {"start": v(-33.89, -64.78) * mm, "end": v(-40.11, -64.78) * mm});
            skLineSegment(sketch, "E3.4.16.2", {"start": v(-33.89, -58.56) * mm, "end": v(-33.89, -64.78) * mm});
            skLineSegment(sketch, "E3.4.16.3", {"start": v(-33.89, -58.56) * mm, "end": v(-40.11, -58.56) * mm});
            skLineSegment(sketch, "E3.4.17.0", {"start": v(-40.11, -66.78) * mm, "end": v(-40.11, -73) * mm});
            skLineSegment(sketch, "E3.4.17.1", {"start": v(-33.89, -73) * mm, "end": v(-40.11, -73) * mm});
            skLineSegment(sketch, "E3.4.17.2", {"start": v(-33.89, -66.78) * mm, "end": v(-33.89, -73) * mm});
            skLineSegment(sketch, "E3.4.17.3", {"start": v(-33.89, -66.78) * mm, "end": v(-40.11, -66.78) * mm});
            skLineSegment(sketch, "E3.5.0.0", {"start": v(-31.89, 73) * mm, "end": v(-31.89, 66.78) * mm});
            skLineSegment(sketch, "E3.5.0.1", {"start": v(-25.67, 66.78) * mm, "end": v(-31.89, 66.78) * mm});
            skLineSegment(sketch, "E3.5.0.2", {"start": v(-25.67, 73) * mm, "end": v(-25.67, 66.78) * mm});
            skLineSegment(sketch, "E3.5.0.3", {"start": v(-25.67, 73) * mm, "end": v(-31.89, 73) * mm});
            skLineSegment(sketch, "E3.5.1.0", {"start": v(-31.89, 64.78) * mm, "end": v(-31.89, 58.56) * mm});
            skLineSegment(sketch, "E3.5.1.1", {"start": v(-25.67, 58.56) * mm, "end": v(-31.89, 58.56) * mm});
            skLineSegment(sketch, "E3.5.1.2", {"start": v(-25.67, 64.78) * mm, "end": v(-25.67, 58.56) * mm});
            skLineSegment(sketch, "E3.5.1.3", {"start": v(-25.67, 64.78) * mm, "end": v(-31.89, 64.78) * mm});
            skLineSegment(sketch, "E3.5.2.0", {"start": v(-31.89, 56.56) * mm, "end": v(-31.89, 50.33) * mm});
            skLineSegment(sketch, "E3.5.2.1", {"start": v(-25.67, 50.33) * mm, "end": v(-31.89, 50.33) * mm});
            skLineSegment(sketch, "E3.5.2.2", {"start": v(-25.67, 56.56) * mm, "end": v(-25.67, 50.33) * mm});
            skLineSegment(sketch, "E3.5.2.3", {"start": v(-25.67, 56.56) * mm, "end": v(-31.89, 56.56) * mm});
            skLineSegment(sketch, "E3.5.3.0", {"start": v(-31.89, 48.33) * mm, "end": v(-31.89, 42.11) * mm});
            skLineSegment(sketch, "E3.5.3.1", {"start": v(-25.67, 42.11) * mm, "end": v(-31.89, 42.11) * mm});
            skLineSegment(sketch, "E3.5.3.2", {"start": v(-25.67, 48.33) * mm, "end": v(-25.67, 42.11) * mm});
            skLineSegment(sketch, "E3.5.3.3", {"start": v(-25.67, 48.33) * mm, "end": v(-31.89, 48.33) * mm});
            skLineSegment(sketch, "E3.5.4.0", {"start": v(-31.89, 40.11) * mm, "end": v(-31.89, 33.89) * mm});
            skLineSegment(sketch, "E3.5.4.1", {"start": v(-25.67, 33.89) * mm, "end": v(-31.89, 33.89) * mm});
            skLineSegment(sketch, "E3.5.4.2", {"start": v(-25.67, 40.11) * mm, "end": v(-25.67, 33.89) * mm});
            skLineSegment(sketch, "E3.5.4.3", {"start": v(-25.67, 40.11) * mm, "end": v(-31.89, 40.11) * mm});
            skLineSegment(sketch, "E3.5.5.0", {"start": v(-31.89, 31.89) * mm, "end": v(-31.89, 25.67) * mm});
            skLineSegment(sketch, "E3.5.5.1", {"start": v(-25.67, 25.67) * mm, "end": v(-31.89, 25.67) * mm});
            skLineSegment(sketch, "E3.5.5.2", {"start": v(-25.67, 31.89) * mm, "end": v(-25.67, 25.67) * mm});
            skLineSegment(sketch, "E3.5.5.3", {"start": v(-25.67, 31.89) * mm, "end": v(-31.89, 31.89) * mm});
            skLineSegment(sketch, "E3.5.6.0", {"start": v(-31.89, 23.67) * mm, "end": v(-31.89, 17.44) * mm});
            skLineSegment(sketch, "E3.5.6.1", {"start": v(-25.67, 17.44) * mm, "end": v(-31.89, 17.44) * mm});
            skLineSegment(sketch, "E3.5.6.2", {"start": v(-25.67, 23.67) * mm, "end": v(-25.67, 17.44) * mm});
            skLineSegment(sketch, "E3.5.6.3", {"start": v(-25.67, 23.67) * mm, "end": v(-31.89, 23.67) * mm});
            skLineSegment(sketch, "E3.5.7.0", {"start": v(-31.89, 15.44) * mm, "end": v(-31.89, 9.22) * mm});
            skLineSegment(sketch, "E3.5.7.1", {"start": v(-25.67, 9.22) * mm, "end": v(-31.89, 9.22) * mm});
            skLineSegment(sketch, "E3.5.7.2", {"start": v(-25.67, 15.44) * mm, "end": v(-25.67, 9.22) * mm});
            skLineSegment(sketch, "E3.5.7.3", {"start": v(-25.67, 15.44) * mm, "end": v(-31.89, 15.44) * mm});
            skLineSegment(sketch, "E3.5.8.0", {"start": v(-31.89, 7.22) * mm, "end": v(-31.89, 1) * mm});
            skLineSegment(sketch, "E3.5.8.1", {"start": v(-25.67, 1) * mm, "end": v(-31.89, 1) * mm});
            skLineSegment(sketch, "E3.5.8.2", {"start": v(-25.67, 7.22) * mm, "end": v(-25.67, 1) * mm});
            skLineSegment(sketch, "E3.5.8.3", {"start": v(-25.67, 7.22) * mm, "end": v(-31.89, 7.22) * mm});
            skLineSegment(sketch, "E3.5.9.0", {"start": v(-31.89, -1) * mm, "end": v(-31.89, -7.22) * mm});
            skLineSegment(sketch, "E3.5.9.1", {"start": v(-25.67, -7.22) * mm, "end": v(-31.89, -7.22) * mm});
            skLineSegment(sketch, "E3.5.9.2", {"start": v(-25.67, -1) * mm, "end": v(-25.67, -7.22) * mm});
            skLineSegment(sketch, "E3.5.9.3", {"start": v(-25.67, -1) * mm, "end": v(-31.89, -1) * mm});
            skLineSegment(sketch, "E3.5.10.0", {"start": v(-31.89, -9.22) * mm, "end": v(-31.89, -15.44) * mm});
            skLineSegment(sketch, "E3.5.10.1", {"start": v(-25.67, -15.44) * mm, "end": v(-31.89, -15.44) * mm});
            skLineSegment(sketch, "E3.5.10.2", {"start": v(-25.67, -9.22) * mm, "end": v(-25.67, -15.44) * mm});
            skLineSegment(sketch, "E3.5.10.3", {"start": v(-25.67, -9.22) * mm, "end": v(-31.89, -9.22) * mm});
            skLineSegment(sketch, "E3.5.11.0", {"start": v(-31.89, -17.44) * mm, "end": v(-31.89, -23.67) * mm});
            skLineSegment(sketch, "E3.5.11.1", {"start": v(-25.67, -23.67) * mm, "end": v(-31.89, -23.67) * mm});
            skLineSegment(sketch, "E3.5.11.2", {"start": v(-25.67, -17.44) * mm, "end": v(-25.67, -23.67) * mm});
            skLineSegment(sketch, "E3.5.11.3", {"start": v(-25.67, -17.44) * mm, "end": v(-31.89, -17.44) * mm});
            skLineSegment(sketch, "E3.5.12.0", {"start": v(-31.89, -25.67) * mm, "end": v(-31.89, -31.89) * mm});
            skLineSegment(sketch, "E3.5.12.1", {"start": v(-25.67, -31.89) * mm, "end": v(-31.89, -31.89) * mm});
            skLineSegment(sketch, "E3.5.12.2", {"start": v(-25.67, -25.67) * mm, "end": v(-25.67, -31.89) * mm});
            skLineSegment(sketch, "E3.5.12.3", {"start": v(-25.67, -25.67) * mm, "end": v(-31.89, -25.67) * mm});
            skLineSegment(sketch, "E3.5.13.0", {"start": v(-31.89, -33.89) * mm, "end": v(-31.89, -40.11) * mm});
            skLineSegment(sketch, "E3.5.13.1", {"start": v(-25.67, -40.11) * mm, "end": v(-31.89, -40.11) * mm});
            skLineSegment(sketch, "E3.5.13.2", {"start": v(-25.67, -33.89) * mm, "end": v(-25.67, -40.11) * mm});
            skLineSegment(sketch, "E3.5.13.3", {"start": v(-25.67, -33.89) * mm, "end": v(-31.89, -33.89) * mm});
            skLineSegment(sketch, "E3.5.14.0", {"start": v(-31.89, -42.11) * mm, "end": v(-31.89, -48.33) * mm});
            skLineSegment(sketch, "E3.5.14.1", {"start": v(-25.67, -48.33) * mm, "end": v(-31.89, -48.33) * mm});
            skLineSegment(sketch, "E3.5.14.2", {"start": v(-25.67, -42.11) * mm, "end": v(-25.67, -48.33) * mm});
            skLineSegment(sketch, "E3.5.14.3", {"start": v(-25.67, -42.11) * mm, "end": v(-31.89, -42.11) * mm});
            skLineSegment(sketch, "E3.5.15.0", {"start": v(-31.89, -50.33) * mm, "end": v(-31.89, -56.56) * mm});
            skLineSegment(sketch, "E3.5.15.1", {"start": v(-25.67, -56.56) * mm, "end": v(-31.89, -56.56) * mm});
            skLineSegment(sketch, "E3.5.15.2", {"start": v(-25.67, -50.33) * mm, "end": v(-25.67, -56.56) * mm});
            skLineSegment(sketch, "E3.5.15.3", {"start": v(-25.67, -50.33) * mm, "end": v(-31.89, -50.33) * mm});
            skLineSegment(sketch, "E3.5.16.0", {"start": v(-31.89, -58.56) * mm, "end": v(-31.89, -64.78) * mm});
            skLineSegment(sketch, "E3.5.16.1", {"start": v(-25.67, -64.78) * mm, "end": v(-31.89, -64.78) * mm});
            skLineSegment(sketch, "E3.5.16.2", {"start": v(-25.67, -58.56) * mm, "end": v(-25.67, -64.78) * mm});
            skLineSegment(sketch, "E3.5.16.3", {"start": v(-25.67, -58.56) * mm, "end": v(-31.89, -58.56) * mm});
            skLineSegment(sketch, "E3.5.17.0", {"start": v(-31.89, -66.78) * mm, "end": v(-31.89, -73) * mm});
            skLineSegment(sketch, "E3.5.17.1", {"start": v(-25.67, -73) * mm, "end": v(-31.89, -73) * mm});
            skLineSegment(sketch, "E3.5.17.2", {"start": v(-25.67, -66.78) * mm, "end": v(-25.67, -73) * mm});
            skLineSegment(sketch, "E3.5.17.3", {"start": v(-25.67, -66.78) * mm, "end": v(-31.89, -66.78) * mm});
            skLineSegment(sketch, "E3.6.0.0", {"start": v(-23.67, 73) * mm, "end": v(-23.67, 66.78) * mm});
            skLineSegment(sketch, "E3.6.0.1", {"start": v(-17.44, 66.78) * mm, "end": v(-23.67, 66.78) * mm});
            skLineSegment(sketch, "E3.6.0.2", {"start": v(-17.44, 73) * mm, "end": v(-17.44, 66.78) * mm});
            skLineSegment(sketch, "E3.6.0.3", {"start": v(-17.44, 73) * mm, "end": v(-23.67, 73) * mm});
            skLineSegment(sketch, "E3.6.1.0", {"start": v(-23.67, 64.78) * mm, "end": v(-23.67, 58.56) * mm});
            skLineSegment(sketch, "E3.6.1.1", {"start": v(-17.44, 58.56) * mm, "end": v(-23.67, 58.56) * mm});
            skLineSegment(sketch, "E3.6.1.2", {"start": v(-17.44, 64.78) * mm, "end": v(-17.44, 58.56) * mm});
            skLineSegment(sketch, "E3.6.1.3", {"start": v(-17.44, 64.78) * mm, "end": v(-23.67, 64.78) * mm});
            skLineSegment(sketch, "E3.6.2.0", {"start": v(-23.67, 56.56) * mm, "end": v(-23.67, 50.33) * mm});
            skLineSegment(sketch, "E3.6.2.1", {"start": v(-17.44, 50.33) * mm, "end": v(-23.67, 50.33) * mm});
            skLineSegment(sketch, "E3.6.2.2", {"start": v(-17.44, 56.56) * mm, "end": v(-17.44, 50.33) * mm});
            skLineSegment(sketch, "E3.6.2.3", {"start": v(-17.44, 56.56) * mm, "end": v(-23.67, 56.56) * mm});
            skLineSegment(sketch, "E3.6.3.0", {"start": v(-23.67, 48.33) * mm, "end": v(-23.67, 42.11) * mm});
            skLineSegment(sketch, "E3.6.3.1", {"start": v(-17.44, 42.11) * mm, "end": v(-23.67, 42.11) * mm});
            skLineSegment(sketch, "E3.6.3.2", {"start": v(-17.44, 48.33) * mm, "end": v(-17.44, 42.11) * mm});
            skLineSegment(sketch, "E3.6.3.3", {"start": v(-17.44, 48.33) * mm, "end": v(-23.67, 48.33) * mm});
            skLineSegment(sketch, "E3.6.4.0", {"start": v(-23.67, 40.11) * mm, "end": v(-23.67, 33.89) * mm});
            skLineSegment(sketch, "E3.6.4.1", {"start": v(-17.44, 33.89) * mm, "end": v(-23.67, 33.89) * mm});
            skLineSegment(sketch, "E3.6.4.2", {"start": v(-17.44, 40.11) * mm, "end": v(-17.44, 33.89) * mm});
            skLineSegment(sketch, "E3.6.4.3", {"start": v(-17.44, 40.11) * mm, "end": v(-23.67, 40.11) * mm});
            skLineSegment(sketch, "E3.6.5.0", {"start": v(-23.67, 31.89) * mm, "end": v(-23.67, 25.67) * mm});
            skLineSegment(sketch, "E3.6.5.1", {"start": v(-17.44, 25.67) * mm, "end": v(-23.67, 25.67) * mm});
            skLineSegment(sketch, "E3.6.5.2", {"start": v(-17.44, 31.89) * mm, "end": v(-17.44, 25.67) * mm});
            skLineSegment(sketch, "E3.6.5.3", {"start": v(-17.44, 31.89) * mm, "end": v(-23.67, 31.89) * mm});
            skLineSegment(sketch, "E3.6.6.0", {"start": v(-23.67, 23.67) * mm, "end": v(-23.67, 17.44) * mm});
            skLineSegment(sketch, "E3.6.6.1", {"start": v(-17.44, 17.44) * mm, "end": v(-23.67, 17.44) * mm});
            skLineSegment(sketch, "E3.6.6.2", {"start": v(-17.44, 23.67) * mm, "end": v(-17.44, 17.44) * mm});
            skLineSegment(sketch, "E3.6.6.3", {"start": v(-17.44, 23.67) * mm, "end": v(-23.67, 23.67) * mm});
            skLineSegment(sketch, "E3.6.7.0", {"start": v(-23.67, 15.44) * mm, "end": v(-23.67, 9.22) * mm});
            skLineSegment(sketch, "E3.6.7.1", {"start": v(-17.44, 9.22) * mm, "end": v(-23.67, 9.22) * mm});
            skLineSegment(sketch, "E3.6.7.2", {"start": v(-17.44, 15.44) * mm, "end": v(-17.44, 9.22) * mm});
            skLineSegment(sketch, "E3.6.7.3", {"start": v(-17.44, 15.44) * mm, "end": v(-23.67, 15.44) * mm});
            skLineSegment(sketch, "E3.6.8.0", {"start": v(-23.67, 7.22) * mm, "end": v(-23.67, 1) * mm});
            skLineSegment(sketch, "E3.6.8.1", {"start": v(-17.44, 1) * mm, "end": v(-23.67, 1) * mm});
            skLineSegment(sketch, "E3.6.8.2", {"start": v(-17.44, 7.22) * mm, "end": v(-17.44, 1) * mm});
            skLineSegment(sketch, "E3.6.8.3", {"start": v(-17.44, 7.22) * mm, "end": v(-23.67, 7.22) * mm});
            skLineSegment(sketch, "E3.6.9.0", {"start": v(-23.67, -1) * mm, "end": v(-23.67, -7.22) * mm});
            skLineSegment(sketch, "E3.6.9.1", {"start": v(-17.44, -7.22) * mm, "end": v(-23.67, -7.22) * mm});
            skLineSegment(sketch, "E3.6.9.2", {"start": v(-17.44, -1) * mm, "end": v(-17.44, -7.22) * mm});
            skLineSegment(sketch, "E3.6.9.3", {"start": v(-17.44, -1) * mm, "end": v(-23.67, -1) * mm});
            skLineSegment(sketch, "E3.6.10.0", {"start": v(-23.67, -9.22) * mm, "end": v(-23.67, -15.44) * mm});
            skLineSegment(sketch, "E3.6.10.1", {"start": v(-17.44, -15.44) * mm, "end": v(-23.67, -15.44) * mm});
            skLineSegment(sketch, "E3.6.10.2", {"start": v(-17.44, -9.22) * mm, "end": v(-17.44, -15.44) * mm});
            skLineSegment(sketch, "E3.6.10.3", {"start": v(-17.44, -9.22) * mm, "end": v(-23.67, -9.22) * mm});
            skLineSegment(sketch, "E3.6.11.0", {"start": v(-23.67, -17.44) * mm, "end": v(-23.67, -23.67) * mm});
            skLineSegment(sketch, "E3.6.11.1", {"start": v(-17.44, -23.67) * mm, "end": v(-23.67, -23.67) * mm});
            skLineSegment(sketch, "E3.6.11.2", {"start": v(-17.44, -17.44) * mm, "end": v(-17.44, -23.67) * mm});
            skLineSegment(sketch, "E3.6.11.3", {"start": v(-17.44, -17.44) * mm, "end": v(-23.67, -17.44) * mm});
            skLineSegment(sketch, "E3.6.12.0", {"start": v(-23.67, -25.67) * mm, "end": v(-23.67, -31.89) * mm});
            skLineSegment(sketch, "E3.6.12.1", {"start": v(-17.44, -31.89) * mm, "end": v(-23.67, -31.89) * mm});
            skLineSegment(sketch, "E3.6.12.2", {"start": v(-17.44, -25.67) * mm, "end": v(-17.44, -31.89) * mm});
            skLineSegment(sketch, "E3.6.12.3", {"start": v(-17.44, -25.67) * mm, "end": v(-23.67, -25.67) * mm});
            skLineSegment(sketch, "E3.6.13.0", {"start": v(-23.67, -33.89) * mm, "end": v(-23.67, -40.11) * mm});
            skLineSegment(sketch, "E3.6.13.1", {"start": v(-17.44, -40.11) * mm, "end": v(-23.67, -40.11) * mm});
            skLineSegment(sketch, "E3.6.13.2", {"start": v(-17.44, -33.89) * mm, "end": v(-17.44, -40.11) * mm});
            skLineSegment(sketch, "E3.6.13.3", {"start": v(-17.44, -33.89) * mm, "end": v(-23.67, -33.89) * mm});
            skLineSegment(sketch, "E3.6.14.0", {"start": v(-23.67, -42.11) * mm, "end": v(-23.67, -48.33) * mm});
            skLineSegment(sketch, "E3.6.14.1", {"start": v(-17.44, -48.33) * mm, "end": v(-23.67, -48.33) * mm});
            skLineSegment(sketch, "E3.6.14.2", {"start": v(-17.44, -42.11) * mm, "end": v(-17.44, -48.33) * mm});
            skLineSegment(sketch, "E3.6.14.3", {"start": v(-17.44, -42.11) * mm, "end": v(-23.67, -42.11) * mm});
            skLineSegment(sketch, "E3.6.15.0", {"start": v(-23.67, -50.33) * mm, "end": v(-23.67, -56.56) * mm});
            skLineSegment(sketch, "E3.6.15.1", {"start": v(-17.44, -56.56) * mm, "end": v(-23.67, -56.56) * mm});
            skLineSegment(sketch, "E3.6.15.2", {"start": v(-17.44, -50.33) * mm, "end": v(-17.44, -56.56) * mm});
            skLineSegment(sketch, "E3.6.15.3", {"start": v(-17.44, -50.33) * mm, "end": v(-23.67, -50.33) * mm});
            skLineSegment(sketch, "E3.6.16.0", {"start": v(-23.67, -58.56) * mm, "end": v(-23.67, -64.78) * mm});
            skLineSegment(sketch, "E3.6.16.1", {"start": v(-17.44, -64.78) * mm, "end": v(-23.67, -64.78) * mm});
            skLineSegment(sketch, "E3.6.16.2", {"start": v(-17.44, -58.56) * mm, "end": v(-17.44, -64.78) * mm});
            skLineSegment(sketch, "E3.6.16.3", {"start": v(-17.44, -58.56) * mm, "end": v(-23.67, -58.56) * mm});
            skLineSegment(sketch, "E3.6.17.0", {"start": v(-23.67, -66.78) * mm, "end": v(-23.67, -73) * mm});
            skLineSegment(sketch, "E3.6.17.1", {"start": v(-17.44, -73) * mm, "end": v(-23.67, -73) * mm});
            skLineSegment(sketch, "E3.6.17.2", {"start": v(-17.44, -66.78) * mm, "end": v(-17.44, -73) * mm});
            skLineSegment(sketch, "E3.6.17.3", {"start": v(-17.44, -66.78) * mm, "end": v(-23.67, -66.78) * mm});
            skLineSegment(sketch, "E3.7.0.0", {"start": v(-15.44, 73) * mm, "end": v(-15.44, 66.78) * mm});
            skLineSegment(sketch, "E3.7.0.1", {"start": v(-9.22, 66.78) * mm, "end": v(-15.44, 66.78) * mm});
            skLineSegment(sketch, "E3.7.0.2", {"start": v(-9.22, 73) * mm, "end": v(-9.22, 66.78) * mm});
            skLineSegment(sketch, "E3.7.0.3", {"start": v(-9.22, 73) * mm, "end": v(-15.44, 73) * mm});
            skLineSegment(sketch, "E3.7.1.0", {"start": v(-15.44, 64.78) * mm, "end": v(-15.44, 58.56) * mm});
            skLineSegment(sketch, "E3.7.1.1", {"start": v(-9.22, 58.56) * mm, "end": v(-15.44, 58.56) * mm});
            skLineSegment(sketch, "E3.7.1.2", {"start": v(-9.22, 64.78) * mm, "end": v(-9.22, 58.56) * mm});
            skLineSegment(sketch, "E3.7.1.3", {"start": v(-9.22, 64.78) * mm, "end": v(-15.44, 64.78) * mm});
            skLineSegment(sketch, "E3.7.2.0", {"start": v(-15.44, 56.56) * mm, "end": v(-15.44, 50.33) * mm});
            skLineSegment(sketch, "E3.7.2.1", {"start": v(-9.22, 50.33) * mm, "end": v(-15.44, 50.33) * mm});
            skLineSegment(sketch, "E3.7.2.2", {"start": v(-9.22, 56.56) * mm, "end": v(-9.22, 50.33) * mm});
            skLineSegment(sketch, "E3.7.2.3", {"start": v(-9.22, 56.56) * mm, "end": v(-15.44, 56.56) * mm});
            skLineSegment(sketch, "E3.7.3.0", {"start": v(-15.44, 48.33) * mm, "end": v(-15.44, 42.11) * mm});
            skLineSegment(sketch, "E3.7.3.1", {"start": v(-9.22, 42.11) * mm, "end": v(-15.44, 42.11) * mm});
            skLineSegment(sketch, "E3.7.3.2", {"start": v(-9.22, 48.33) * mm, "end": v(-9.22, 42.11) * mm});
            skLineSegment(sketch, "E3.7.3.3", {"start": v(-9.22, 48.33) * mm, "end": v(-15.44, 48.33) * mm});
            skLineSegment(sketch, "E3.7.4.0", {"start": v(-15.44, 40.11) * mm, "end": v(-15.44, 33.89) * mm});
            skLineSegment(sketch, "E3.7.4.1", {"start": v(-9.22, 33.89) * mm, "end": v(-15.44, 33.89) * mm});
            skLineSegment(sketch, "E3.7.4.2", {"start": v(-9.22, 40.11) * mm, "end": v(-9.22, 33.89) * mm});
            skLineSegment(sketch, "E3.7.4.3", {"start": v(-9.22, 40.11) * mm, "end": v(-15.44, 40.11) * mm});
            skLineSegment(sketch, "E3.7.5.0", {"start": v(-15.44, 31.89) * mm, "end": v(-15.44, 25.67) * mm});
            skLineSegment(sketch, "E3.7.5.1", {"start": v(-9.22, 25.67) * mm, "end": v(-15.44, 25.67) * mm});
            skLineSegment(sketch, "E3.7.5.2", {"start": v(-9.22, 31.89) * mm, "end": v(-9.22, 25.67) * mm});
            skLineSegment(sketch, "E3.7.5.3", {"start": v(-9.22, 31.89) * mm, "end": v(-15.44, 31.89) * mm});
            skLineSegment(sketch, "E3.7.6.0", {"start": v(-15.44, 23.67) * mm, "end": v(-15.44, 17.44) * mm});
            skLineSegment(sketch, "E3.7.6.1", {"start": v(-9.22, 17.44) * mm, "end": v(-15.44, 17.44) * mm});
            skLineSegment(sketch, "E3.7.6.2", {"start": v(-9.22, 23.67) * mm, "end": v(-9.22, 17.44) * mm});
            skLineSegment(sketch, "E3.7.6.3", {"start": v(-9.22, 23.67) * mm, "end": v(-15.44, 23.67) * mm});
            skLineSegment(sketch, "E3.7.7.0", {"start": v(-15.44, 15.44) * mm, "end": v(-15.44, 9.22) * mm});
            skLineSegment(sketch, "E3.7.7.1", {"start": v(-9.22, 9.22) * mm, "end": v(-15.44, 9.22) * mm});
            skLineSegment(sketch, "E3.7.7.2", {"start": v(-9.22, 15.44) * mm, "end": v(-9.22, 9.22) * mm});
            skLineSegment(sketch, "E3.7.7.3", {"start": v(-9.22, 15.44) * mm, "end": v(-15.44, 15.44) * mm});
            skLineSegment(sketch, "E3.7.8.0", {"start": v(-15.44, 7.22) * mm, "end": v(-15.44, 1) * mm});
            skLineSegment(sketch, "E3.7.8.1", {"start": v(-9.22, 1) * mm, "end": v(-15.44, 1) * mm});
            skLineSegment(sketch, "E3.7.8.2", {"start": v(-9.22, 7.22) * mm, "end": v(-9.22, 1) * mm});
            skLineSegment(sketch, "E3.7.8.3", {"start": v(-9.22, 7.22) * mm, "end": v(-15.44, 7.22) * mm});
            skLineSegment(sketch, "E3.7.9.0", {"start": v(-15.44, -1) * mm, "end": v(-15.44, -7.22) * mm});
            skLineSegment(sketch, "E3.7.9.1", {"start": v(-9.22, -7.22) * mm, "end": v(-15.44, -7.22) * mm});
            skLineSegment(sketch, "E3.7.9.2", {"start": v(-9.22, -1) * mm, "end": v(-9.22, -7.22) * mm});
            skLineSegment(sketch, "E3.7.9.3", {"start": v(-9.22, -1) * mm, "end": v(-15.44, -1) * mm});
            skLineSegment(sketch, "E3.7.10.0", {"start": v(-15.44, -9.22) * mm, "end": v(-15.44, -15.44) * mm});
            skLineSegment(sketch, "E3.7.10.1", {"start": v(-9.22, -15.44) * mm, "end": v(-15.44, -15.44) * mm});
            skLineSegment(sketch, "E3.7.10.2", {"start": v(-9.22, -9.22) * mm, "end": v(-9.22, -15.44) * mm});
            skLineSegment(sketch, "E3.7.10.3", {"start": v(-9.22, -9.22) * mm, "end": v(-15.44, -9.22) * mm});
            skLineSegment(sketch, "E3.7.11.0", {"start": v(-15.44, -17.44) * mm, "end": v(-15.44, -23.67) * mm});
            skLineSegment(sketch, "E3.7.11.1", {"start": v(-9.22, -23.67) * mm, "end": v(-15.44, -23.67) * mm});
            skLineSegment(sketch, "E3.7.11.2", {"start": v(-9.22, -17.44) * mm, "end": v(-9.22, -23.67) * mm});
            skLineSegment(sketch, "E3.7.11.3", {"start": v(-9.22, -17.44) * mm, "end": v(-15.44, -17.44) * mm});
            skLineSegment(sketch, "E3.7.12.0", {"start": v(-15.44, -25.67) * mm, "end": v(-15.44, -31.89) * mm});
            skLineSegment(sketch, "E3.7.12.1", {"start": v(-9.22, -31.89) * mm, "end": v(-15.44, -31.89) * mm});
            skLineSegment(sketch, "E3.7.12.2", {"start": v(-9.22, -25.67) * mm, "end": v(-9.22, -31.89) * mm});
            skLineSegment(sketch, "E3.7.12.3", {"start": v(-9.22, -25.67) * mm, "end": v(-15.44, -25.67) * mm});
            skLineSegment(sketch, "E3.7.13.0", {"start": v(-15.44, -33.89) * mm, "end": v(-15.44, -40.11) * mm});
            skLineSegment(sketch, "E3.7.13.1", {"start": v(-9.22, -40.11) * mm, "end": v(-15.44, -40.11) * mm});
            skLineSegment(sketch, "E3.7.13.2", {"start": v(-9.22, -33.89) * mm, "end": v(-9.22, -40.11) * mm});
            skLineSegment(sketch, "E3.7.13.3", {"start": v(-9.22, -33.89) * mm, "end": v(-15.44, -33.89) * mm});
            skLineSegment(sketch, "E3.7.14.0", {"start": v(-15.44, -42.11) * mm, "end": v(-15.44, -48.33) * mm});
            skLineSegment(sketch, "E3.7.14.1", {"start": v(-9.22, -48.33) * mm, "end": v(-15.44, -48.33) * mm});
            skLineSegment(sketch, "E3.7.14.2", {"start": v(-9.22, -42.11) * mm, "end": v(-9.22, -48.33) * mm});
            skLineSegment(sketch, "E3.7.14.3", {"start": v(-9.22, -42.11) * mm, "end": v(-15.44, -42.11) * mm});
            skLineSegment(sketch, "E3.7.15.0", {"start": v(-15.44, -50.33) * mm, "end": v(-15.44, -56.56) * mm});
            skLineSegment(sketch, "E3.7.15.1", {"start": v(-9.22, -56.56) * mm, "end": v(-15.44, -56.56) * mm});
            skLineSegment(sketch, "E3.7.15.2", {"start": v(-9.22, -50.33) * mm, "end": v(-9.22, -56.56) * mm});
            skLineSegment(sketch, "E3.7.15.3", {"start": v(-9.22, -50.33) * mm, "end": v(-15.44, -50.33) * mm});
            skLineSegment(sketch, "E3.7.16.0", {"start": v(-15.44, -58.56) * mm, "end": v(-15.44, -64.78) * mm});
            skLineSegment(sketch, "E3.7.16.1", {"start": v(-9.22, -64.78) * mm, "end": v(-15.44, -64.78) * mm});
            skLineSegment(sketch, "E3.7.16.2", {"start": v(-9.22, -58.56) * mm, "end": v(-9.22, -64.78) * mm});
            skLineSegment(sketch, "E3.7.16.3", {"start": v(-9.22, -58.56) * mm, "end": v(-15.44, -58.56) * mm});
            skLineSegment(sketch, "E3.7.17.0", {"start": v(-15.44, -66.78) * mm, "end": v(-15.44, -73) * mm});
            skLineSegment(sketch, "E3.7.17.1", {"start": v(-9.22, -73) * mm, "end": v(-15.44, -73) * mm});
            skLineSegment(sketch, "E3.7.17.2", {"start": v(-9.22, -66.78) * mm, "end": v(-9.22, -73) * mm});
            skLineSegment(sketch, "E3.7.17.3", {"start": v(-9.22, -66.78) * mm, "end": v(-15.44, -66.78) * mm});
            skLineSegment(sketch, "E3.8.0.0", {"start": v(-7.22, 73) * mm, "end": v(-7.22, 66.78) * mm});
            skLineSegment(sketch, "E3.8.0.1", {"start": v(-1, 66.78) * mm, "end": v(-7.22, 66.78) * mm});
            skLineSegment(sketch, "E3.8.0.2", {"start": v(-1, 73) * mm, "end": v(-1, 66.78) * mm});
            skLineSegment(sketch, "E3.8.0.3", {"start": v(-1, 73) * mm, "end": v(-7.22, 73) * mm});
            skLineSegment(sketch, "E3.8.1.0", {"start": v(-7.22, 64.78) * mm, "end": v(-7.22, 58.56) * mm});
            skLineSegment(sketch, "E3.8.1.1", {"start": v(-1, 58.56) * mm, "end": v(-7.22, 58.56) * mm});
            skLineSegment(sketch, "E3.8.1.2", {"start": v(-1, 64.78) * mm, "end": v(-1, 58.56) * mm});
            skLineSegment(sketch, "E3.8.1.3", {"start": v(-1, 64.78) * mm, "end": v(-7.22, 64.78) * mm});
            skLineSegment(sketch, "E3.8.2.0", {"start": v(-7.22, 56.56) * mm, "end": v(-7.22, 50.33) * mm});
            skLineSegment(sketch, "E3.8.2.1", {"start": v(-1, 50.33) * mm, "end": v(-7.22, 50.33) * mm});
            skLineSegment(sketch, "E3.8.2.2", {"start": v(-1, 56.56) * mm, "end": v(-1, 50.33) * mm});
            skLineSegment(sketch, "E3.8.2.3", {"start": v(-1, 56.56) * mm, "end": v(-7.22, 56.56) * mm});
            skLineSegment(sketch, "E3.8.3.0", {"start": v(-7.22, 48.33) * mm, "end": v(-7.22, 42.11) * mm});
            skLineSegment(sketch, "E3.8.3.1", {"start": v(-1, 42.11) * mm, "end": v(-7.22, 42.11) * mm});
            skLineSegment(sketch, "E3.8.3.2", {"start": v(-1, 48.33) * mm, "end": v(-1, 42.11) * mm});
            skLineSegment(sketch, "E3.8.3.3", {"start": v(-1, 48.33) * mm, "end": v(-7.22, 48.33) * mm});
            skLineSegment(sketch, "E3.8.4.0", {"start": v(-7.22, 40.11) * mm, "end": v(-7.22, 33.89) * mm});
            skLineSegment(sketch, "E3.8.4.1", {"start": v(-1, 33.89) * mm, "end": v(-7.22, 33.89) * mm});
            skLineSegment(sketch, "E3.8.4.2", {"start": v(-1, 40.11) * mm, "end": v(-1, 33.89) * mm});
            skLineSegment(sketch, "E3.8.4.3", {"start": v(-1, 40.11) * mm, "end": v(-7.22, 40.11) * mm});
            skLineSegment(sketch, "E3.8.5.0", {"start": v(-7.22, 31.89) * mm, "end": v(-7.22, 25.67) * mm});
            skLineSegment(sketch, "E3.8.5.1", {"start": v(-1, 25.67) * mm, "end": v(-7.22, 25.67) * mm});
            skLineSegment(sketch, "E3.8.5.2", {"start": v(-1, 31.89) * mm, "end": v(-1, 25.67) * mm});
            skLineSegment(sketch, "E3.8.5.3", {"start": v(-1, 31.89) * mm, "end": v(-7.22, 31.89) * mm});
            skLineSegment(sketch, "E3.8.6.0", {"start": v(-7.22, 23.67) * mm, "end": v(-7.22, 17.44) * mm});
            skLineSegment(sketch, "E3.8.6.1", {"start": v(-1, 17.44) * mm, "end": v(-7.22, 17.44) * mm});
            skLineSegment(sketch, "E3.8.6.2", {"start": v(-1, 23.67) * mm, "end": v(-1, 17.44) * mm});
            skLineSegment(sketch, "E3.8.6.3", {"start": v(-1, 23.67) * mm, "end": v(-7.22, 23.67) * mm});
            skLineSegment(sketch, "E3.8.7.0", {"start": v(-7.22, 15.44) * mm, "end": v(-7.22, 9.22) * mm});
            skLineSegment(sketch, "E3.8.7.1", {"start": v(-1, 9.22) * mm, "end": v(-7.22, 9.22) * mm});
            skLineSegment(sketch, "E3.8.7.2", {"start": v(-1, 15.44) * mm, "end": v(-1, 9.22) * mm});
            skLineSegment(sketch, "E3.8.7.3", {"start": v(-1, 15.44) * mm, "end": v(-7.22, 15.44) * mm});
            skLineSegment(sketch, "E3.8.8.0", {"start": v(-7.22, 7.22) * mm, "end": v(-7.22, 1) * mm});
            skLineSegment(sketch, "E3.8.8.1", {"start": v(-1, 1) * mm, "end": v(-7.22, 1) * mm});
            skLineSegment(sketch, "E3.8.8.2", {"start": v(-1, 7.22) * mm, "end": v(-1, 1) * mm});
            skLineSegment(sketch, "E3.8.8.3", {"start": v(-1, 7.22) * mm, "end": v(-7.22, 7.22) * mm});
            skLineSegment(sketch, "E3.8.9.0", {"start": v(-7.22, -1) * mm, "end": v(-7.22, -7.22) * mm});
            skLineSegment(sketch, "E3.8.9.1", {"start": v(-1, -7.22) * mm, "end": v(-7.22, -7.22) * mm});
            skLineSegment(sketch, "E3.8.9.2", {"start": v(-1, -1) * mm, "end": v(-1, -7.22) * mm});
            skLineSegment(sketch, "E3.8.9.3", {"start": v(-1, -1) * mm, "end": v(-7.22, -1) * mm});
            skLineSegment(sketch, "E3.8.10.0", {"start": v(-7.22, -9.22) * mm, "end": v(-7.22, -15.44) * mm});
            skLineSegment(sketch, "E3.8.10.1", {"start": v(-1, -15.44) * mm, "end": v(-7.22, -15.44) * mm});
            skLineSegment(sketch, "E3.8.10.2", {"start": v(-1, -9.22) * mm, "end": v(-1, -15.44) * mm});
            skLineSegment(sketch, "E3.8.10.3", {"start": v(-1, -9.22) * mm, "end": v(-7.22, -9.22) * mm});
            skLineSegment(sketch, "E3.8.11.0", {"start": v(-7.22, -17.44) * mm, "end": v(-7.22, -23.67) * mm});
            skLineSegment(sketch, "E3.8.11.1", {"start": v(-1, -23.67) * mm, "end": v(-7.22, -23.67) * mm});
            skLineSegment(sketch, "E3.8.11.2", {"start": v(-1, -17.44) * mm, "end": v(-1, -23.67) * mm});
            skLineSegment(sketch, "E3.8.11.3", {"start": v(-1, -17.44) * mm, "end": v(-7.22, -17.44) * mm});
            skLineSegment(sketch, "E3.8.12.0", {"start": v(-7.22, -25.67) * mm, "end": v(-7.22, -31.89) * mm});
            skLineSegment(sketch, "E3.8.12.1", {"start": v(-1, -31.89) * mm, "end": v(-7.22, -31.89) * mm});
            skLineSegment(sketch, "E3.8.12.2", {"start": v(-1, -25.67) * mm, "end": v(-1, -31.89) * mm});
            skLineSegment(sketch, "E3.8.12.3", {"start": v(-1, -25.67) * mm, "end": v(-7.22, -25.67) * mm});
            skLineSegment(sketch, "E3.8.13.0", {"start": v(-7.22, -33.89) * mm, "end": v(-7.22, -40.11) * mm});
            skLineSegment(sketch, "E3.8.13.1", {"start": v(-1, -40.11) * mm, "end": v(-7.22, -40.11) * mm});
            skLineSegment(sketch, "E3.8.13.2", {"start": v(-1, -33.89) * mm, "end": v(-1, -40.11) * mm});
            skLineSegment(sketch, "E3.8.13.3", {"start": v(-1, -33.89) * mm, "end": v(-7.22, -33.89) * mm});
            skLineSegment(sketch, "E3.8.14.0", {"start": v(-7.22, -42.11) * mm, "end": v(-7.22, -48.33) * mm});
            skLineSegment(sketch, "E3.8.14.1", {"start": v(-1, -48.33) * mm, "end": v(-7.22, -48.33) * mm});
            skLineSegment(sketch, "E3.8.14.2", {"start": v(-1, -42.11) * mm, "end": v(-1, -48.33) * mm});
            skLineSegment(sketch, "E3.8.14.3", {"start": v(-1, -42.11) * mm, "end": v(-7.22, -42.11) * mm});
            skLineSegment(sketch, "E3.8.15.0", {"start": v(-7.22, -50.33) * mm, "end": v(-7.22, -56.56) * mm});
            skLineSegment(sketch, "E3.8.15.1", {"start": v(-1, -56.56) * mm, "end": v(-7.22, -56.56) * mm});
            skLineSegment(sketch, "E3.8.15.2", {"start": v(-1, -50.33) * mm, "end": v(-1, -56.56) * mm});
            skLineSegment(sketch, "E3.8.15.3", {"start": v(-1, -50.33) * mm, "end": v(-7.22, -50.33) * mm});
            skLineSegment(sketch, "E3.8.16.0", {"start": v(-7.22, -58.56) * mm, "end": v(-7.22, -64.78) * mm});
            skLineSegment(sketch, "E3.8.16.1", {"start": v(-1, -64.78) * mm, "end": v(-7.22, -64.78) * mm});
            skLineSegment(sketch, "E3.8.16.2", {"start": v(-1, -58.56) * mm, "end": v(-1, -64.78) * mm});
            skLineSegment(sketch, "E3.8.16.3", {"start": v(-1, -58.56) * mm, "end": v(-7.22, -58.56) * mm});
            skLineSegment(sketch, "E3.8.17.0", {"start": v(-7.22, -66.78) * mm, "end": v(-7.22, -73) * mm});
            skLineSegment(sketch, "E3.8.17.1", {"start": v(-1, -73) * mm, "end": v(-7.22, -73) * mm});
            skLineSegment(sketch, "E3.8.17.2", {"start": v(-1, -66.78) * mm, "end": v(-1, -73) * mm});
            skLineSegment(sketch, "E3.8.17.3", {"start": v(-1, -66.78) * mm, "end": v(-7.22, -66.78) * mm});
            skLineSegment(sketch, "E3.9.0.0", {"start": v(1, 73) * mm, "end": v(1, 66.78) * mm});
            skLineSegment(sketch, "E3.9.0.1", {"start": v(7.22, 66.78) * mm, "end": v(1, 66.78) * mm});
            skLineSegment(sketch, "E3.9.0.2", {"start": v(7.22, 73) * mm, "end": v(7.22, 66.78) * mm});
            skLineSegment(sketch, "E3.9.0.3", {"start": v(7.22, 73) * mm, "end": v(1, 73) * mm});
            skLineSegment(sketch, "E3.9.1.0", {"start": v(1, 64.78) * mm, "end": v(1, 58.56) * mm});
            skLineSegment(sketch, "E3.9.1.1", {"start": v(7.22, 58.56) * mm, "end": v(1, 58.56) * mm});
            skLineSegment(sketch, "E3.9.1.2", {"start": v(7.22, 64.78) * mm, "end": v(7.22, 58.56) * mm});
            skLineSegment(sketch, "E3.9.1.3", {"start": v(7.22, 64.78) * mm, "end": v(1, 64.78) * mm});
            skLineSegment(sketch, "E3.9.2.0", {"start": v(1, 56.56) * mm, "end": v(1, 50.33) * mm});
            skLineSegment(sketch, "E3.9.2.1", {"start": v(7.22, 50.33) * mm, "end": v(1, 50.33) * mm});
            skLineSegment(sketch, "E3.9.2.2", {"start": v(7.22, 56.56) * mm, "end": v(7.22, 50.33) * mm});
            skLineSegment(sketch, "E3.9.2.3", {"start": v(7.22, 56.56) * mm, "end": v(1, 56.56) * mm});
            skLineSegment(sketch, "E3.9.3.0", {"start": v(1, 48.33) * mm, "end": v(1, 42.11) * mm});
            skLineSegment(sketch, "E3.9.3.1", {"start": v(7.22, 42.11) * mm, "end": v(1, 42.11) * mm});
            skLineSegment(sketch, "E3.9.3.2", {"start": v(7.22, 48.33) * mm, "end": v(7.22, 42.11) * mm});
            skLineSegment(sketch, "E3.9.3.3", {"start": v(7.22, 48.33) * mm, "end": v(1, 48.33) * mm});
            skLineSegment(sketch, "E3.9.4.0", {"start": v(1, 40.11) * mm, "end": v(1, 33.89) * mm});
            skLineSegment(sketch, "E3.9.4.1", {"start": v(7.22, 33.89) * mm, "end": v(1, 33.89) * mm});
            skLineSegment(sketch, "E3.9.4.2", {"start": v(7.22, 40.11) * mm, "end": v(7.22, 33.89) * mm});
            skLineSegment(sketch, "E3.9.4.3", {"start": v(7.22, 40.11) * mm, "end": v(1, 40.11) * mm});
            skLineSegment(sketch, "E3.9.5.0", {"start": v(1, 31.89) * mm, "end": v(1, 25.67) * mm});
            skLineSegment(sketch, "E3.9.5.1", {"start": v(7.22, 25.67) * mm, "end": v(1, 25.67) * mm});
            skLineSegment(sketch, "E3.9.5.2", {"start": v(7.22, 31.89) * mm, "end": v(7.22, 25.67) * mm});
            skLineSegment(sketch, "E3.9.5.3", {"start": v(7.22, 31.89) * mm, "end": v(1, 31.89) * mm});
            skLineSegment(sketch, "E3.9.6.0", {"start": v(1, 23.67) * mm, "end": v(1, 17.44) * mm});
            skLineSegment(sketch, "E3.9.6.1", {"start": v(7.22, 17.44) * mm, "end": v(1, 17.44) * mm});
            skLineSegment(sketch, "E3.9.6.2", {"start": v(7.22, 23.67) * mm, "end": v(7.22, 17.44) * mm});
            skLineSegment(sketch, "E3.9.6.3", {"start": v(7.22, 23.67) * mm, "end": v(1, 23.67) * mm});
            skLineSegment(sketch, "E3.9.7.0", {"start": v(1, 15.44) * mm, "end": v(1, 9.22) * mm});
            skLineSegment(sketch, "E3.9.7.1", {"start": v(7.22, 9.22) * mm, "end": v(1, 9.22) * mm});
            skLineSegment(sketch, "E3.9.7.2", {"start": v(7.22, 15.44) * mm, "end": v(7.22, 9.22) * mm});
            skLineSegment(sketch, "E3.9.7.3", {"start": v(7.22, 15.44) * mm, "end": v(1, 15.44) * mm});
            skLineSegment(sketch, "E3.9.8.0", {"start": v(1, 7.22) * mm, "end": v(1, 1) * mm});
            skLineSegment(sketch, "E3.9.8.1", {"start": v(7.22, 1) * mm, "end": v(1, 1) * mm});
            skLineSegment(sketch, "E3.9.8.2", {"start": v(7.22, 7.22) * mm, "end": v(7.22, 1) * mm});
            skLineSegment(sketch, "E3.9.8.3", {"start": v(7.22, 7.22) * mm, "end": v(1, 7.22) * mm});
            skLineSegment(sketch, "E3.9.9.0", {"start": v(1, -1) * mm, "end": v(1, -7.22) * mm});
            skLineSegment(sketch, "E3.9.9.1", {"start": v(7.22, -7.22) * mm, "end": v(1, -7.22) * mm});
            skLineSegment(sketch, "E3.9.9.2", {"start": v(7.22, -1) * mm, "end": v(7.22, -7.22) * mm});
            skLineSegment(sketch, "E3.9.9.3", {"start": v(7.22, -1) * mm, "end": v(1, -1) * mm});
            skLineSegment(sketch, "E3.9.10.0", {"start": v(1, -9.22) * mm, "end": v(1, -15.44) * mm});
            skLineSegment(sketch, "E3.9.10.1", {"start": v(7.22, -15.44) * mm, "end": v(1, -15.44) * mm});
            skLineSegment(sketch, "E3.9.10.2", {"start": v(7.22, -9.22) * mm, "end": v(7.22, -15.44) * mm});
            skLineSegment(sketch, "E3.9.10.3", {"start": v(7.22, -9.22) * mm, "end": v(1, -9.22) * mm});
            skLineSegment(sketch, "E3.9.11.0", {"start": v(1, -17.44) * mm, "end": v(1, -23.67) * mm});
            skLineSegment(sketch, "E3.9.11.1", {"start": v(7.22, -23.67) * mm, "end": v(1, -23.67) * mm});
            skLineSegment(sketch, "E3.9.11.2", {"start": v(7.22, -17.44) * mm, "end": v(7.22, -23.67) * mm});
            skLineSegment(sketch, "E3.9.11.3", {"start": v(7.22, -17.44) * mm, "end": v(1, -17.44) * mm});
            skLineSegment(sketch, "E3.9.12.0", {"start": v(1, -25.67) * mm, "end": v(1, -31.89) * mm});
            skLineSegment(sketch, "E3.9.12.1", {"start": v(7.22, -31.89) * mm, "end": v(1, -31.89) * mm});
            skLineSegment(sketch, "E3.9.12.2", {"start": v(7.22, -25.67) * mm, "end": v(7.22, -31.89) * mm});
            skLineSegment(sketch, "E3.9.12.3", {"start": v(7.22, -25.67) * mm, "end": v(1, -25.67) * mm});
            skLineSegment(sketch, "E3.9.13.0", {"start": v(1, -33.89) * mm, "end": v(1, -40.11) * mm});
            skLineSegment(sketch, "E3.9.13.1", {"start": v(7.22, -40.11) * mm, "end": v(1, -40.11) * mm});
            skLineSegment(sketch, "E3.9.13.2", {"start": v(7.22, -33.89) * mm, "end": v(7.22, -40.11) * mm});
            skLineSegment(sketch, "E3.9.13.3", {"start": v(7.22, -33.89) * mm, "end": v(1, -33.89) * mm});
            skLineSegment(sketch, "E3.9.14.0", {"start": v(1, -42.11) * mm, "end": v(1, -48.33) * mm});
            skLineSegment(sketch, "E3.9.14.1", {"start": v(7.22, -48.33) * mm, "end": v(1, -48.33) * mm});
            skLineSegment(sketch, "E3.9.14.2", {"start": v(7.22, -42.11) * mm, "end": v(7.22, -48.33) * mm});
            skLineSegment(sketch, "E3.9.14.3", {"start": v(7.22, -42.11) * mm, "end": v(1, -42.11) * mm});
            skLineSegment(sketch, "E3.9.15.0", {"start": v(1, -50.33) * mm, "end": v(1, -56.56) * mm});
            skLineSegment(sketch, "E3.9.15.1", {"start": v(7.22, -56.56) * mm, "end": v(1, -56.56) * mm});
            skLineSegment(sketch, "E3.9.15.2", {"start": v(7.22, -50.33) * mm, "end": v(7.22, -56.56) * mm});
            skLineSegment(sketch, "E3.9.15.3", {"start": v(7.22, -50.33) * mm, "end": v(1, -50.33) * mm});
            skLineSegment(sketch, "E3.9.16.0", {"start": v(1, -58.56) * mm, "end": v(1, -64.78) * mm});
            skLineSegment(sketch, "E3.9.16.1", {"start": v(7.22, -64.78) * mm, "end": v(1, -64.78) * mm});
            skLineSegment(sketch, "E3.9.16.2", {"start": v(7.22, -58.56) * mm, "end": v(7.22, -64.78) * mm});
            skLineSegment(sketch, "E3.9.16.3", {"start": v(7.22, -58.56) * mm, "end": v(1, -58.56) * mm});
            skLineSegment(sketch, "E3.9.17.0", {"start": v(1, -66.78) * mm, "end": v(1, -73) * mm});
            skLineSegment(sketch, "E3.9.17.1", {"start": v(7.22, -73) * mm, "end": v(1, -73) * mm});
            skLineSegment(sketch, "E3.9.17.2", {"start": v(7.22, -66.78) * mm, "end": v(7.22, -73) * mm});
            skLineSegment(sketch, "E3.9.17.3", {"start": v(7.22, -66.78) * mm, "end": v(1, -66.78) * mm});
            skLineSegment(sketch, "E3.10.0.0", {"start": v(9.22, 73) * mm, "end": v(9.22, 66.78) * mm});
            skLineSegment(sketch, "E3.10.0.1", {"start": v(15.44, 66.78) * mm, "end": v(9.22, 66.78) * mm});
            skLineSegment(sketch, "E3.10.0.2", {"start": v(15.44, 73) * mm, "end": v(15.44, 66.78) * mm});
            skLineSegment(sketch, "E3.10.0.3", {"start": v(15.44, 73) * mm, "end": v(9.22, 73) * mm});
            skLineSegment(sketch, "E3.10.1.0", {"start": v(9.22, 64.78) * mm, "end": v(9.22, 58.56) * mm});
            skLineSegment(sketch, "E3.10.1.1", {"start": v(15.44, 58.56) * mm, "end": v(9.22, 58.56) * mm});
            skLineSegment(sketch, "E3.10.1.2", {"start": v(15.44, 64.78) * mm, "end": v(15.44, 58.56) * mm});
            skLineSegment(sketch, "E3.10.1.3", {"start": v(15.44, 64.78) * mm, "end": v(9.22, 64.78) * mm});
            skLineSegment(sketch, "E3.10.2.0", {"start": v(9.22, 56.56) * mm, "end": v(9.22, 50.33) * mm});
            skLineSegment(sketch, "E3.10.2.1", {"start": v(15.44, 50.33) * mm, "end": v(9.22, 50.33) * mm});
            skLineSegment(sketch, "E3.10.2.2", {"start": v(15.44, 56.56) * mm, "end": v(15.44, 50.33) * mm});
            skLineSegment(sketch, "E3.10.2.3", {"start": v(15.44, 56.56) * mm, "end": v(9.22, 56.56) * mm});
            skLineSegment(sketch, "E3.10.3.0", {"start": v(9.22, 48.33) * mm, "end": v(9.22, 42.11) * mm});
            skLineSegment(sketch, "E3.10.3.1", {"start": v(15.44, 42.11) * mm, "end": v(9.22, 42.11) * mm});
            skLineSegment(sketch, "E3.10.3.2", {"start": v(15.44, 48.33) * mm, "end": v(15.44, 42.11) * mm});
            skLineSegment(sketch, "E3.10.3.3", {"start": v(15.44, 48.33) * mm, "end": v(9.22, 48.33) * mm});
            skLineSegment(sketch, "E3.10.4.0", {"start": v(9.22, 40.11) * mm, "end": v(9.22, 33.89) * mm});
            skLineSegment(sketch, "E3.10.4.1", {"start": v(15.44, 33.89) * mm, "end": v(9.22, 33.89) * mm});
            skLineSegment(sketch, "E3.10.4.2", {"start": v(15.44, 40.11) * mm, "end": v(15.44, 33.89) * mm});
            skLineSegment(sketch, "E3.10.4.3", {"start": v(15.44, 40.11) * mm, "end": v(9.22, 40.11) * mm});
            skLineSegment(sketch, "E3.10.5.0", {"start": v(9.22, 31.89) * mm, "end": v(9.22, 25.67) * mm});
            skLineSegment(sketch, "E3.10.5.1", {"start": v(15.44, 25.67) * mm, "end": v(9.22, 25.67) * mm});
            skLineSegment(sketch, "E3.10.5.2", {"start": v(15.44, 31.89) * mm, "end": v(15.44, 25.67) * mm});
            skLineSegment(sketch, "E3.10.5.3", {"start": v(15.44, 31.89) * mm, "end": v(9.22, 31.89) * mm});
            skLineSegment(sketch, "E3.10.6.0", {"start": v(9.22, 23.67) * mm, "end": v(9.22, 17.44) * mm});
            skLineSegment(sketch, "E3.10.6.1", {"start": v(15.44, 17.44) * mm, "end": v(9.22, 17.44) * mm});
            skLineSegment(sketch, "E3.10.6.2", {"start": v(15.44, 23.67) * mm, "end": v(15.44, 17.44) * mm});
            skLineSegment(sketch, "E3.10.6.3", {"start": v(15.44, 23.67) * mm, "end": v(9.22, 23.67) * mm});
            skLineSegment(sketch, "E3.10.7.0", {"start": v(9.22, 15.44) * mm, "end": v(9.22, 9.22) * mm});
            skLineSegment(sketch, "E3.10.7.1", {"start": v(15.44, 9.22) * mm, "end": v(9.22, 9.22) * mm});
            skLineSegment(sketch, "E3.10.7.2", {"start": v(15.44, 15.44) * mm, "end": v(15.44, 9.22) * mm});
            skLineSegment(sketch, "E3.10.7.3", {"start": v(15.44, 15.44) * mm, "end": v(9.22, 15.44) * mm});
            skLineSegment(sketch, "E3.10.8.0", {"start": v(9.22, 7.22) * mm, "end": v(9.22, 1) * mm});
            skLineSegment(sketch, "E3.10.8.1", {"start": v(15.44, 1) * mm, "end": v(9.22, 1) * mm});
            skLineSegment(sketch, "E3.10.8.2", {"start": v(15.44, 7.22) * mm, "end": v(15.44, 1) * mm});
            skLineSegment(sketch, "E3.10.8.3", {"start": v(15.44, 7.22) * mm, "end": v(9.22, 7.22) * mm});
            skLineSegment(sketch, "E3.10.9.0", {"start": v(9.22, -1) * mm, "end": v(9.22, -7.22) * mm});
            skLineSegment(sketch, "E3.10.9.1", {"start": v(15.44, -7.22) * mm, "end": v(9.22, -7.22) * mm});
            skLineSegment(sketch, "E3.10.9.2", {"start": v(15.44, -1) * mm, "end": v(15.44, -7.22) * mm});
            skLineSegment(sketch, "E3.10.9.3", {"start": v(15.44, -1) * mm, "end": v(9.22, -1) * mm});
            skLineSegment(sketch, "E3.10.10.0", {"start": v(9.22, -9.22) * mm, "end": v(9.22, -15.44) * mm});
            skLineSegment(sketch, "E3.10.10.1", {"start": v(15.44, -15.44) * mm, "end": v(9.22, -15.44) * mm});
            skLineSegment(sketch, "E3.10.10.2", {"start": v(15.44, -9.22) * mm, "end": v(15.44, -15.44) * mm});
            skLineSegment(sketch, "E3.10.10.3", {"start": v(15.44, -9.22) * mm, "end": v(9.22, -9.22) * mm});
            skLineSegment(sketch, "E3.10.11.0", {"start": v(9.22, -17.44) * mm, "end": v(9.22, -23.67) * mm});
            skLineSegment(sketch, "E3.10.11.1", {"start": v(15.44, -23.67) * mm, "end": v(9.22, -23.67) * mm});
            skLineSegment(sketch, "E3.10.11.2", {"start": v(15.44, -17.44) * mm, "end": v(15.44, -23.67) * mm});
            skLineSegment(sketch, "E3.10.11.3", {"start": v(15.44, -17.44) * mm, "end": v(9.22, -17.44) * mm});
            skLineSegment(sketch, "E3.10.12.0", {"start": v(9.22, -25.67) * mm, "end": v(9.22, -31.89) * mm});
            skLineSegment(sketch, "E3.10.12.1", {"start": v(15.44, -31.89) * mm, "end": v(9.22, -31.89) * mm});
            skLineSegment(sketch, "E3.10.12.2", {"start": v(15.44, -25.67) * mm, "end": v(15.44, -31.89) * mm});
            skLineSegment(sketch, "E3.10.12.3", {"start": v(15.44, -25.67) * mm, "end": v(9.22, -25.67) * mm});
            skLineSegment(sketch, "E3.10.13.0", {"start": v(9.22, -33.89) * mm, "end": v(9.22, -40.11) * mm});
            skLineSegment(sketch, "E3.10.13.1", {"start": v(15.44, -40.11) * mm, "end": v(9.22, -40.11) * mm});
            skLineSegment(sketch, "E3.10.13.2", {"start": v(15.44, -33.89) * mm, "end": v(15.44, -40.11) * mm});
            skLineSegment(sketch, "E3.10.13.3", {"start": v(15.44, -33.89) * mm, "end": v(9.22, -33.89) * mm});
            skLineSegment(sketch, "E3.10.14.0", {"start": v(9.22, -42.11) * mm, "end": v(9.22, -48.33) * mm});
            skLineSegment(sketch, "E3.10.14.1", {"start": v(15.44, -48.33) * mm, "end": v(9.22, -48.33) * mm});
            skLineSegment(sketch, "E3.10.14.2", {"start": v(15.44, -42.11) * mm, "end": v(15.44, -48.33) * mm});
            skLineSegment(sketch, "E3.10.14.3", {"start": v(15.44, -42.11) * mm, "end": v(9.22, -42.11) * mm});
            skLineSegment(sketch, "E3.10.15.0", {"start": v(9.22, -50.33) * mm, "end": v(9.22, -56.56) * mm});
            skLineSegment(sketch, "E3.10.15.1", {"start": v(15.44, -56.56) * mm, "end": v(9.22, -56.56) * mm});
            skLineSegment(sketch, "E3.10.15.2", {"start": v(15.44, -50.33) * mm, "end": v(15.44, -56.56) * mm});
            skLineSegment(sketch, "E3.10.15.3", {"start": v(15.44, -50.33) * mm, "end": v(9.22, -50.33) * mm});
            skLineSegment(sketch, "E3.10.16.0", {"start": v(9.22, -58.56) * mm, "end": v(9.22, -64.78) * mm});
            skLineSegment(sketch, "E3.10.16.1", {"start": v(15.44, -64.78) * mm, "end": v(9.22, -64.78) * mm});
            skLineSegment(sketch, "E3.10.16.2", {"start": v(15.44, -58.56) * mm, "end": v(15.44, -64.78) * mm});
            skLineSegment(sketch, "E3.10.16.3", {"start": v(15.44, -58.56) * mm, "end": v(9.22, -58.56) * mm});
            skLineSegment(sketch, "E3.10.17.0", {"start": v(9.22, -66.78) * mm, "end": v(9.22, -73) * mm});
            skLineSegment(sketch, "E3.10.17.1", {"start": v(15.44, -73) * mm, "end": v(9.22, -73) * mm});
            skLineSegment(sketch, "E3.10.17.2", {"start": v(15.44, -66.78) * mm, "end": v(15.44, -73) * mm});
            skLineSegment(sketch, "E3.10.17.3", {"start": v(15.44, -66.78) * mm, "end": v(9.22, -66.78) * mm});
            skLineSegment(sketch, "E3.11.0.0", {"start": v(17.44, 73) * mm, "end": v(17.44, 66.78) * mm});
            skLineSegment(sketch, "E3.11.0.1", {"start": v(23.67, 66.78) * mm, "end": v(17.44, 66.78) * mm});
            skLineSegment(sketch, "E3.11.0.2", {"start": v(23.67, 73) * mm, "end": v(23.67, 66.78) * mm});
            skLineSegment(sketch, "E3.11.0.3", {"start": v(23.67, 73) * mm, "end": v(17.44, 73) * mm});
            skLineSegment(sketch, "E3.11.1.0", {"start": v(17.44, 64.78) * mm, "end": v(17.44, 58.56) * mm});
            skLineSegment(sketch, "E3.11.1.1", {"start": v(23.67, 58.56) * mm, "end": v(17.44, 58.56) * mm});
            skLineSegment(sketch, "E3.11.1.2", {"start": v(23.67, 64.78) * mm, "end": v(23.67, 58.56) * mm});
            skLineSegment(sketch, "E3.11.1.3", {"start": v(23.67, 64.78) * mm, "end": v(17.44, 64.78) * mm});
            skLineSegment(sketch, "E3.11.2.0", {"start": v(17.44, 56.56) * mm, "end": v(17.44, 50.33) * mm});
            skLineSegment(sketch, "E3.11.2.1", {"start": v(23.67, 50.33) * mm, "end": v(17.44, 50.33) * mm});
            skLineSegment(sketch, "E3.11.2.2", {"start": v(23.67, 56.56) * mm, "end": v(23.67, 50.33) * mm});
            skLineSegment(sketch, "E3.11.2.3", {"start": v(23.67, 56.56) * mm, "end": v(17.44, 56.56) * mm});
            skLineSegment(sketch, "E3.11.3.0", {"start": v(17.44, 48.33) * mm, "end": v(17.44, 42.11) * mm});
            skLineSegment(sketch, "E3.11.3.1", {"start": v(23.67, 42.11) * mm, "end": v(17.44, 42.11) * mm});
            skLineSegment(sketch, "E3.11.3.2", {"start": v(23.67, 48.33) * mm, "end": v(23.67, 42.11) * mm});
            skLineSegment(sketch, "E3.11.3.3", {"start": v(23.67, 48.33) * mm, "end": v(17.44, 48.33) * mm});
            skLineSegment(sketch, "E3.11.4.0", {"start": v(17.44, 40.11) * mm, "end": v(17.44, 33.89) * mm});
            skLineSegment(sketch, "E3.11.4.1", {"start": v(23.67, 33.89) * mm, "end": v(17.44, 33.89) * mm});
            skLineSegment(sketch, "E3.11.4.2", {"start": v(23.67, 40.11) * mm, "end": v(23.67, 33.89) * mm});
            skLineSegment(sketch, "E3.11.4.3", {"start": v(23.67, 40.11) * mm, "end": v(17.44, 40.11) * mm});
            skLineSegment(sketch, "E3.11.5.0", {"start": v(17.44, 31.89) * mm, "end": v(17.44, 25.67) * mm});
            skLineSegment(sketch, "E3.11.5.1", {"start": v(23.67, 25.67) * mm, "end": v(17.44, 25.67) * mm});
            skLineSegment(sketch, "E3.11.5.2", {"start": v(23.67, 31.89) * mm, "end": v(23.67, 25.67) * mm});
            skLineSegment(sketch, "E3.11.5.3", {"start": v(23.67, 31.89) * mm, "end": v(17.44, 31.89) * mm});
            skLineSegment(sketch, "E3.11.6.0", {"start": v(17.44, 23.67) * mm, "end": v(17.44, 17.44) * mm});
            skLineSegment(sketch, "E3.11.6.1", {"start": v(23.67, 17.44) * mm, "end": v(17.44, 17.44) * mm});
            skLineSegment(sketch, "E3.11.6.2", {"start": v(23.67, 23.67) * mm, "end": v(23.67, 17.44) * mm});
            skLineSegment(sketch, "E3.11.6.3", {"start": v(23.67, 23.67) * mm, "end": v(17.44, 23.67) * mm});
            skLineSegment(sketch, "E3.11.7.0", {"start": v(17.44, 15.44) * mm, "end": v(17.44, 9.22) * mm});
            skLineSegment(sketch, "E3.11.7.1", {"start": v(23.67, 9.22) * mm, "end": v(17.44, 9.22) * mm});
            skLineSegment(sketch, "E3.11.7.2", {"start": v(23.67, 15.44) * mm, "end": v(23.67, 9.22) * mm});
            skLineSegment(sketch, "E3.11.7.3", {"start": v(23.67, 15.44) * mm, "end": v(17.44, 15.44) * mm});
            skLineSegment(sketch, "E3.11.8.0", {"start": v(17.44, 7.22) * mm, "end": v(17.44, 1) * mm});
            skLineSegment(sketch, "E3.11.8.1", {"start": v(23.67, 1) * mm, "end": v(17.44, 1) * mm});
            skLineSegment(sketch, "E3.11.8.2", {"start": v(23.67, 7.22) * mm, "end": v(23.67, 1) * mm});
            skLineSegment(sketch, "E3.11.8.3", {"start": v(23.67, 7.22) * mm, "end": v(17.44, 7.22) * mm});
            skLineSegment(sketch, "E3.11.9.0", {"start": v(17.44, -1) * mm, "end": v(17.44, -7.22) * mm});
            skLineSegment(sketch, "E3.11.9.1", {"start": v(23.67, -7.22) * mm, "end": v(17.44, -7.22) * mm});
            skLineSegment(sketch, "E3.11.9.2", {"start": v(23.67, -1) * mm, "end": v(23.67, -7.22) * mm});
            skLineSegment(sketch, "E3.11.9.3", {"start": v(23.67, -1) * mm, "end": v(17.44, -1) * mm});
            skLineSegment(sketch, "E3.11.10.0", {"start": v(17.44, -9.22) * mm, "end": v(17.44, -15.44) * mm});
            skLineSegment(sketch, "E3.11.10.1", {"start": v(23.67, -15.44) * mm, "end": v(17.44, -15.44) * mm});
            skLineSegment(sketch, "E3.11.10.2", {"start": v(23.67, -9.22) * mm, "end": v(23.67, -15.44) * mm});
            skLineSegment(sketch, "E3.11.10.3", {"start": v(23.67, -9.22) * mm, "end": v(17.44, -9.22) * mm});
            skLineSegment(sketch, "E3.11.11.0", {"start": v(17.44, -17.44) * mm, "end": v(17.44, -23.67) * mm});
            skLineSegment(sketch, "E3.11.11.1", {"start": v(23.67, -23.67) * mm, "end": v(17.44, -23.67) * mm});
            skLineSegment(sketch, "E3.11.11.2", {"start": v(23.67, -17.44) * mm, "end": v(23.67, -23.67) * mm});
            skLineSegment(sketch, "E3.11.11.3", {"start": v(23.67, -17.44) * mm, "end": v(17.44, -17.44) * mm});
            skLineSegment(sketch, "E3.11.12.0", {"start": v(17.44, -25.67) * mm, "end": v(17.44, -31.89) * mm});
            skLineSegment(sketch, "E3.11.12.1", {"start": v(23.67, -31.89) * mm, "end": v(17.44, -31.89) * mm});
            skLineSegment(sketch, "E3.11.12.2", {"start": v(23.67, -25.67) * mm, "end": v(23.67, -31.89) * mm});
            skLineSegment(sketch, "E3.11.12.3", {"start": v(23.67, -25.67) * mm, "end": v(17.44, -25.67) * mm});
            skLineSegment(sketch, "E3.11.13.0", {"start": v(17.44, -33.89) * mm, "end": v(17.44, -40.11) * mm});
            skLineSegment(sketch, "E3.11.13.1", {"start": v(23.67, -40.11) * mm, "end": v(17.44, -40.11) * mm});
            skLineSegment(sketch, "E3.11.13.2", {"start": v(23.67, -33.89) * mm, "end": v(23.67, -40.11) * mm});
            skLineSegment(sketch, "E3.11.13.3", {"start": v(23.67, -33.89) * mm, "end": v(17.44, -33.89) * mm});
            skLineSegment(sketch, "E3.11.14.0", {"start": v(17.44, -42.11) * mm, "end": v(17.44, -48.33) * mm});
            skLineSegment(sketch, "E3.11.14.1", {"start": v(23.67, -48.33) * mm, "end": v(17.44, -48.33) * mm});
            skLineSegment(sketch, "E3.11.14.2", {"start": v(23.67, -42.11) * mm, "end": v(23.67, -48.33) * mm});
            skLineSegment(sketch, "E3.11.14.3", {"start": v(23.67, -42.11) * mm, "end": v(17.44, -42.11) * mm});
            skLineSegment(sketch, "E3.11.15.0", {"start": v(17.44, -50.33) * mm, "end": v(17.44, -56.56) * mm});
            skLineSegment(sketch, "E3.11.15.1", {"start": v(23.67, -56.56) * mm, "end": v(17.44, -56.56) * mm});
            skLineSegment(sketch, "E3.11.15.2", {"start": v(23.67, -50.33) * mm, "end": v(23.67, -56.56) * mm});
            skLineSegment(sketch, "E3.11.15.3", {"start": v(23.67, -50.33) * mm, "end": v(17.44, -50.33) * mm});
            skLineSegment(sketch, "E3.11.16.0", {"start": v(17.44, -58.56) * mm, "end": v(17.44, -64.78) * mm});
            skLineSegment(sketch, "E3.11.16.1", {"start": v(23.67, -64.78) * mm, "end": v(17.44, -64.78) * mm});
            skLineSegment(sketch, "E3.11.16.2", {"start": v(23.67, -58.56) * mm, "end": v(23.67, -64.78) * mm});
            skLineSegment(sketch, "E3.11.16.3", {"start": v(23.67, -58.56) * mm, "end": v(17.44, -58.56) * mm});
            skLineSegment(sketch, "E3.11.17.0", {"start": v(17.44, -66.78) * mm, "end": v(17.44, -73) * mm});
            skLineSegment(sketch, "E3.11.17.1", {"start": v(23.67, -73) * mm, "end": v(17.44, -73) * mm});
            skLineSegment(sketch, "E3.11.17.2", {"start": v(23.67, -66.78) * mm, "end": v(23.67, -73) * mm});
            skLineSegment(sketch, "E3.11.17.3", {"start": v(23.67, -66.78) * mm, "end": v(17.44, -66.78) * mm});
            skLineSegment(sketch, "E3.12.0.0", {"start": v(25.67, 73) * mm, "end": v(25.67, 66.78) * mm});
            skLineSegment(sketch, "E3.12.0.1", {"start": v(31.89, 66.78) * mm, "end": v(25.67, 66.78) * mm});
            skLineSegment(sketch, "E3.12.0.2", {"start": v(31.89, 73) * mm, "end": v(31.89, 66.78) * mm});
            skLineSegment(sketch, "E3.12.0.3", {"start": v(31.89, 73) * mm, "end": v(25.67, 73) * mm});
            skLineSegment(sketch, "E3.12.1.0", {"start": v(25.67, 64.78) * mm, "end": v(25.67, 58.56) * mm});
            skLineSegment(sketch, "E3.12.1.1", {"start": v(31.89, 58.56) * mm, "end": v(25.67, 58.56) * mm});
            skLineSegment(sketch, "E3.12.1.2", {"start": v(31.89, 64.78) * mm, "end": v(31.89, 58.56) * mm});
            skLineSegment(sketch, "E3.12.1.3", {"start": v(31.89, 64.78) * mm, "end": v(25.67, 64.78) * mm});
            skLineSegment(sketch, "E3.12.2.0", {"start": v(25.67, 56.56) * mm, "end": v(25.67, 50.33) * mm});
            skLineSegment(sketch, "E3.12.2.1", {"start": v(31.89, 50.33) * mm, "end": v(25.67, 50.33) * mm});
            skLineSegment(sketch, "E3.12.2.2", {"start": v(31.89, 56.56) * mm, "end": v(31.89, 50.33) * mm});
            skLineSegment(sketch, "E3.12.2.3", {"start": v(31.89, 56.56) * mm, "end": v(25.67, 56.56) * mm});
            skLineSegment(sketch, "E3.12.3.0", {"start": v(25.67, 48.33) * mm, "end": v(25.67, 42.11) * mm});
            skLineSegment(sketch, "E3.12.3.1", {"start": v(31.89, 42.11) * mm, "end": v(25.67, 42.11) * mm});
            skLineSegment(sketch, "E3.12.3.2", {"start": v(31.89, 48.33) * mm, "end": v(31.89, 42.11) * mm});
            skLineSegment(sketch, "E3.12.3.3", {"start": v(31.89, 48.33) * mm, "end": v(25.67, 48.33) * mm});
            skLineSegment(sketch, "E3.12.4.0", {"start": v(25.67, 40.11) * mm, "end": v(25.67, 33.89) * mm});
            skLineSegment(sketch, "E3.12.4.1", {"start": v(31.89, 33.89) * mm, "end": v(25.67, 33.89) * mm});
            skLineSegment(sketch, "E3.12.4.2", {"start": v(31.89, 40.11) * mm, "end": v(31.89, 33.89) * mm});
            skLineSegment(sketch, "E3.12.4.3", {"start": v(31.89, 40.11) * mm, "end": v(25.67, 40.11) * mm});
            skLineSegment(sketch, "E3.12.5.0", {"start": v(25.67, 31.89) * mm, "end": v(25.67, 25.67) * mm});
            skLineSegment(sketch, "E3.12.5.1", {"start": v(31.89, 25.67) * mm, "end": v(25.67, 25.67) * mm});
            skLineSegment(sketch, "E3.12.5.2", {"start": v(31.89, 31.89) * mm, "end": v(31.89, 25.67) * mm});
            skLineSegment(sketch, "E3.12.5.3", {"start": v(31.89, 31.89) * mm, "end": v(25.67, 31.89) * mm});
            skLineSegment(sketch, "E3.12.6.0", {"start": v(25.67, 23.67) * mm, "end": v(25.67, 17.44) * mm});
            skLineSegment(sketch, "E3.12.6.1", {"start": v(31.89, 17.44) * mm, "end": v(25.67, 17.44) * mm});
            skLineSegment(sketch, "E3.12.6.2", {"start": v(31.89, 23.67) * mm, "end": v(31.89, 17.44) * mm});
            skLineSegment(sketch, "E3.12.6.3", {"start": v(31.89, 23.67) * mm, "end": v(25.67, 23.67) * mm});
            skLineSegment(sketch, "E3.12.7.0", {"start": v(25.67, 15.44) * mm, "end": v(25.67, 9.22) * mm});
            skLineSegment(sketch, "E3.12.7.1", {"start": v(31.89, 9.22) * mm, "end": v(25.67, 9.22) * mm});
            skLineSegment(sketch, "E3.12.7.2", {"start": v(31.89, 15.44) * mm, "end": v(31.89, 9.22) * mm});
            skLineSegment(sketch, "E3.12.7.3", {"start": v(31.89, 15.44) * mm, "end": v(25.67, 15.44) * mm});
            skLineSegment(sketch, "E3.12.8.0", {"start": v(25.67, 7.22) * mm, "end": v(25.67, 1) * mm});
            skLineSegment(sketch, "E3.12.8.1", {"start": v(31.89, 1) * mm, "end": v(25.67, 1) * mm});
            skLineSegment(sketch, "E3.12.8.2", {"start": v(31.89, 7.22) * mm, "end": v(31.89, 1) * mm});
            skLineSegment(sketch, "E3.12.8.3", {"start": v(31.89, 7.22) * mm, "end": v(25.67, 7.22) * mm});
            skLineSegment(sketch, "E3.12.9.0", {"start": v(25.67, -1) * mm, "end": v(25.67, -7.22) * mm});
            skLineSegment(sketch, "E3.12.9.1", {"start": v(31.89, -7.22) * mm, "end": v(25.67, -7.22) * mm});
            skLineSegment(sketch, "E3.12.9.2", {"start": v(31.89, -1) * mm, "end": v(31.89, -7.22) * mm});
            skLineSegment(sketch, "E3.12.9.3", {"start": v(31.89, -1) * mm, "end": v(25.67, -1) * mm});
            skLineSegment(sketch, "E3.12.10.0", {"start": v(25.67, -9.22) * mm, "end": v(25.67, -15.44) * mm});
            skLineSegment(sketch, "E3.12.10.1", {"start": v(31.89, -15.44) * mm, "end": v(25.67, -15.44) * mm});
            skLineSegment(sketch, "E3.12.10.2", {"start": v(31.89, -9.22) * mm, "end": v(31.89, -15.44) * mm});
            skLineSegment(sketch, "E3.12.10.3", {"start": v(31.89, -9.22) * mm, "end": v(25.67, -9.22) * mm});
            skLineSegment(sketch, "E3.12.11.0", {"start": v(25.67, -17.44) * mm, "end": v(25.67, -23.67) * mm});
            skLineSegment(sketch, "E3.12.11.1", {"start": v(31.89, -23.67) * mm, "end": v(25.67, -23.67) * mm});
            skLineSegment(sketch, "E3.12.11.2", {"start": v(31.89, -17.44) * mm, "end": v(31.89, -23.67) * mm});
            skLineSegment(sketch, "E3.12.11.3", {"start": v(31.89, -17.44) * mm, "end": v(25.67, -17.44) * mm});
            skLineSegment(sketch, "E3.12.12.0", {"start": v(25.67, -25.67) * mm, "end": v(25.67, -31.89) * mm});
            skLineSegment(sketch, "E3.12.12.1", {"start": v(31.89, -31.89) * mm, "end": v(25.67, -31.89) * mm});
            skLineSegment(sketch, "E3.12.12.2", {"start": v(31.89, -25.67) * mm, "end": v(31.89, -31.89) * mm});
            skLineSegment(sketch, "E3.12.12.3", {"start": v(31.89, -25.67) * mm, "end": v(25.67, -25.67) * mm});
            skLineSegment(sketch, "E3.12.13.0", {"start": v(25.67, -33.89) * mm, "end": v(25.67, -40.11) * mm});
            skLineSegment(sketch, "E3.12.13.1", {"start": v(31.89, -40.11) * mm, "end": v(25.67, -40.11) * mm});
            skLineSegment(sketch, "E3.12.13.2", {"start": v(31.89, -33.89) * mm, "end": v(31.89, -40.11) * mm});
            skLineSegment(sketch, "E3.12.13.3", {"start": v(31.89, -33.89) * mm, "end": v(25.67, -33.89) * mm});
            skLineSegment(sketch, "E3.12.14.0", {"start": v(25.67, -42.11) * mm, "end": v(25.67, -48.33) * mm});
            skLineSegment(sketch, "E3.12.14.1", {"start": v(31.89, -48.33) * mm, "end": v(25.67, -48.33) * mm});
            skLineSegment(sketch, "E3.12.14.2", {"start": v(31.89, -42.11) * mm, "end": v(31.89, -48.33) * mm});
            skLineSegment(sketch, "E3.12.14.3", {"start": v(31.89, -42.11) * mm, "end": v(25.67, -42.11) * mm});
            skLineSegment(sketch, "E3.12.15.0", {"start": v(25.67, -50.33) * mm, "end": v(25.67, -56.56) * mm});
            skLineSegment(sketch, "E3.12.15.1", {"start": v(31.89, -56.56) * mm, "end": v(25.67, -56.56) * mm});
            skLineSegment(sketch, "E3.12.15.2", {"start": v(31.89, -50.33) * mm, "end": v(31.89, -56.56) * mm});
            skLineSegment(sketch, "E3.12.15.3", {"start": v(31.89, -50.33) * mm, "end": v(25.67, -50.33) * mm});
            skLineSegment(sketch, "E3.12.16.0", {"start": v(25.67, -58.56) * mm, "end": v(25.67, -64.78) * mm});
            skLineSegment(sketch, "E3.12.16.1", {"start": v(31.89, -64.78) * mm, "end": v(25.67, -64.78) * mm});
            skLineSegment(sketch, "E3.12.16.2", {"start": v(31.89, -58.56) * mm, "end": v(31.89, -64.78) * mm});
            skLineSegment(sketch, "E3.12.16.3", {"start": v(31.89, -58.56) * mm, "end": v(25.67, -58.56) * mm});
            skLineSegment(sketch, "E3.12.17.0", {"start": v(25.67, -66.78) * mm, "end": v(25.67, -73) * mm});
            skLineSegment(sketch, "E3.12.17.1", {"start": v(31.89, -73) * mm, "end": v(25.67, -73) * mm});
            skLineSegment(sketch, "E3.12.17.2", {"start": v(31.89, -66.78) * mm, "end": v(31.89, -73) * mm});
            skLineSegment(sketch, "E3.12.17.3", {"start": v(31.89, -66.78) * mm, "end": v(25.67, -66.78) * mm});
            skLineSegment(sketch, "E3.13.0.0", {"start": v(33.89, 73) * mm, "end": v(33.89, 66.78) * mm});
            skLineSegment(sketch, "E3.13.0.1", {"start": v(40.11, 66.78) * mm, "end": v(33.89, 66.78) * mm});
            skLineSegment(sketch, "E3.13.0.2", {"start": v(40.11, 73) * mm, "end": v(40.11, 66.78) * mm});
            skLineSegment(sketch, "E3.13.0.3", {"start": v(40.11, 73) * mm, "end": v(33.89, 73) * mm});
            skLineSegment(sketch, "E3.13.1.0", {"start": v(33.89, 64.78) * mm, "end": v(33.89, 58.56) * mm});
            skLineSegment(sketch, "E3.13.1.1", {"start": v(40.11, 58.56) * mm, "end": v(33.89, 58.56) * mm});
            skLineSegment(sketch, "E3.13.1.2", {"start": v(40.11, 64.78) * mm, "end": v(40.11, 58.56) * mm});
            skLineSegment(sketch, "E3.13.1.3", {"start": v(40.11, 64.78) * mm, "end": v(33.89, 64.78) * mm});
            skLineSegment(sketch, "E3.13.2.0", {"start": v(33.89, 56.56) * mm, "end": v(33.89, 50.33) * mm});
            skLineSegment(sketch, "E3.13.2.1", {"start": v(40.11, 50.33) * mm, "end": v(33.89, 50.33) * mm});
            skLineSegment(sketch, "E3.13.2.2", {"start": v(40.11, 56.56) * mm, "end": v(40.11, 50.33) * mm});
            skLineSegment(sketch, "E3.13.2.3", {"start": v(40.11, 56.56) * mm, "end": v(33.89, 56.56) * mm});
            skLineSegment(sketch, "E3.13.3.0", {"start": v(33.89, 48.33) * mm, "end": v(33.89, 42.11) * mm});
            skLineSegment(sketch, "E3.13.3.1", {"start": v(40.11, 42.11) * mm, "end": v(33.89, 42.11) * mm});
            skLineSegment(sketch, "E3.13.3.2", {"start": v(40.11, 48.33) * mm, "end": v(40.11, 42.11) * mm});
            skLineSegment(sketch, "E3.13.3.3", {"start": v(40.11, 48.33) * mm, "end": v(33.89, 48.33) * mm});
            skLineSegment(sketch, "E3.13.4.0", {"start": v(33.89, 40.11) * mm, "end": v(33.89, 33.89) * mm});
            skLineSegment(sketch, "E3.13.4.1", {"start": v(40.11, 33.89) * mm, "end": v(33.89, 33.89) * mm});
            skLineSegment(sketch, "E3.13.4.2", {"start": v(40.11, 40.11) * mm, "end": v(40.11, 33.89) * mm});
            skLineSegment(sketch, "E3.13.4.3", {"start": v(40.11, 40.11) * mm, "end": v(33.89, 40.11) * mm});
            skLineSegment(sketch, "E3.13.5.0", {"start": v(33.89, 31.89) * mm, "end": v(33.89, 25.67) * mm});
            skLineSegment(sketch, "E3.13.5.1", {"start": v(40.11, 25.67) * mm, "end": v(33.89, 25.67) * mm});
            skLineSegment(sketch, "E3.13.5.2", {"start": v(40.11, 31.89) * mm, "end": v(40.11, 25.67) * mm});
            skLineSegment(sketch, "E3.13.5.3", {"start": v(40.11, 31.89) * mm, "end": v(33.89, 31.89) * mm});
            skLineSegment(sketch, "E3.13.6.0", {"start": v(33.89, 23.67) * mm, "end": v(33.89, 17.44) * mm});
            skLineSegment(sketch, "E3.13.6.1", {"start": v(40.11, 17.44) * mm, "end": v(33.89, 17.44) * mm});
            skLineSegment(sketch, "E3.13.6.2", {"start": v(40.11, 23.67) * mm, "end": v(40.11, 17.44) * mm});
            skLineSegment(sketch, "E3.13.6.3", {"start": v(40.11, 23.67) * mm, "end": v(33.89, 23.67) * mm});
            skLineSegment(sketch, "E3.13.7.0", {"start": v(33.89, 15.44) * mm, "end": v(33.89, 9.22) * mm});
            skLineSegment(sketch, "E3.13.7.1", {"start": v(40.11, 9.22) * mm, "end": v(33.89, 9.22) * mm});
            skLineSegment(sketch, "E3.13.7.2", {"start": v(40.11, 15.44) * mm, "end": v(40.11, 9.22) * mm});
            skLineSegment(sketch, "E3.13.7.3", {"start": v(40.11, 15.44) * mm, "end": v(33.89, 15.44) * mm});
            skLineSegment(sketch, "E3.13.8.0", {"start": v(33.89, 7.22) * mm, "end": v(33.89, 1) * mm});
            skLineSegment(sketch, "E3.13.8.1", {"start": v(40.11, 1) * mm, "end": v(33.89, 1) * mm});
            skLineSegment(sketch, "E3.13.8.2", {"start": v(40.11, 7.22) * mm, "end": v(40.11, 1) * mm});
            skLineSegment(sketch, "E3.13.8.3", {"start": v(40.11, 7.22) * mm, "end": v(33.89, 7.22) * mm});
            skLineSegment(sketch, "E3.13.9.0", {"start": v(33.89, -1) * mm, "end": v(33.89, -7.22) * mm});
            skLineSegment(sketch, "E3.13.9.1", {"start": v(40.11, -7.22) * mm, "end": v(33.89, -7.22) * mm});
            skLineSegment(sketch, "E3.13.9.2", {"start": v(40.11, -1) * mm, "end": v(40.11, -7.22) * mm});
            skLineSegment(sketch, "E3.13.9.3", {"start": v(40.11, -1) * mm, "end": v(33.89, -1) * mm});
            skLineSegment(sketch, "E3.13.10.0", {"start": v(33.89, -9.22) * mm, "end": v(33.89, -15.44) * mm});
            skLineSegment(sketch, "E3.13.10.1", {"start": v(40.11, -15.44) * mm, "end": v(33.89, -15.44) * mm});
            skLineSegment(sketch, "E3.13.10.2", {"start": v(40.11, -9.22) * mm, "end": v(40.11, -15.44) * mm});
            skLineSegment(sketch, "E3.13.10.3", {"start": v(40.11, -9.22) * mm, "end": v(33.89, -9.22) * mm});
            skLineSegment(sketch, "E3.13.11.0", {"start": v(33.89, -17.44) * mm, "end": v(33.89, -23.67) * mm});
            skLineSegment(sketch, "E3.13.11.1", {"start": v(40.11, -23.67) * mm, "end": v(33.89, -23.67) * mm});
            skLineSegment(sketch, "E3.13.11.2", {"start": v(40.11, -17.44) * mm, "end": v(40.11, -23.67) * mm});
            skLineSegment(sketch, "E3.13.11.3", {"start": v(40.11, -17.44) * mm, "end": v(33.89, -17.44) * mm});
            skLineSegment(sketch, "E3.13.12.0", {"start": v(33.89, -25.67) * mm, "end": v(33.89, -31.89) * mm});
            skLineSegment(sketch, "E3.13.12.1", {"start": v(40.11, -31.89) * mm, "end": v(33.89, -31.89) * mm});
            skLineSegment(sketch, "E3.13.12.2", {"start": v(40.11, -25.67) * mm, "end": v(40.11, -31.89) * mm});
            skLineSegment(sketch, "E3.13.12.3", {"start": v(40.11, -25.67) * mm, "end": v(33.89, -25.67) * mm});
            skLineSegment(sketch, "E3.13.13.0", {"start": v(33.89, -33.89) * mm, "end": v(33.89, -40.11) * mm});
            skLineSegment(sketch, "E3.13.13.1", {"start": v(40.11, -40.11) * mm, "end": v(33.89, -40.11) * mm});
            skLineSegment(sketch, "E3.13.13.2", {"start": v(40.11, -33.89) * mm, "end": v(40.11, -40.11) * mm});
            skLineSegment(sketch, "E3.13.13.3", {"start": v(40.11, -33.89) * mm, "end": v(33.89, -33.89) * mm});
            skLineSegment(sketch, "E3.13.14.0", {"start": v(33.89, -42.11) * mm, "end": v(33.89, -48.33) * mm});
            skLineSegment(sketch, "E3.13.14.1", {"start": v(40.11, -48.33) * mm, "end": v(33.89, -48.33) * mm});
            skLineSegment(sketch, "E3.13.14.2", {"start": v(40.11, -42.11) * mm, "end": v(40.11, -48.33) * mm});
            skLineSegment(sketch, "E3.13.14.3", {"start": v(40.11, -42.11) * mm, "end": v(33.89, -42.11) * mm});
            skLineSegment(sketch, "E3.13.15.0", {"start": v(33.89, -50.33) * mm, "end": v(33.89, -56.56) * mm});
            skLineSegment(sketch, "E3.13.15.1", {"start": v(40.11, -56.56) * mm, "end": v(33.89, -56.56) * mm});
            skLineSegment(sketch, "E3.13.15.2", {"start": v(40.11, -50.33) * mm, "end": v(40.11, -56.56) * mm});
            skLineSegment(sketch, "E3.13.15.3", {"start": v(40.11, -50.33) * mm, "end": v(33.89, -50.33) * mm});
            skLineSegment(sketch, "E3.13.16.0", {"start": v(33.89, -58.56) * mm, "end": v(33.89, -64.78) * mm});
            skLineSegment(sketch, "E3.13.16.1", {"start": v(40.11, -64.78) * mm, "end": v(33.89, -64.78) * mm});
            skLineSegment(sketch, "E3.13.16.2", {"start": v(40.11, -58.56) * mm, "end": v(40.11, -64.78) * mm});
            skLineSegment(sketch, "E3.13.16.3", {"start": v(40.11, -58.56) * mm, "end": v(33.89, -58.56) * mm});
            skLineSegment(sketch, "E3.13.17.0", {"start": v(33.89, -66.78) * mm, "end": v(33.89, -73) * mm});
            skLineSegment(sketch, "E3.13.17.1", {"start": v(40.11, -73) * mm, "end": v(33.89, -73) * mm});
            skLineSegment(sketch, "E3.13.17.2", {"start": v(40.11, -66.78) * mm, "end": v(40.11, -73) * mm});
            skLineSegment(sketch, "E3.13.17.3", {"start": v(40.11, -66.78) * mm, "end": v(33.89, -66.78) * mm});
            skLineSegment(sketch, "E3.14.0.0", {"start": v(42.11, 73) * mm, "end": v(42.11, 66.78) * mm});
            skLineSegment(sketch, "E3.14.0.1", {"start": v(48.33, 66.78) * mm, "end": v(42.11, 66.78) * mm});
            skLineSegment(sketch, "E3.14.0.2", {"start": v(48.33, 73) * mm, "end": v(48.33, 66.78) * mm});
            skLineSegment(sketch, "E3.14.0.3", {"start": v(48.33, 73) * mm, "end": v(42.11, 73) * mm});
            skLineSegment(sketch, "E3.14.1.0", {"start": v(42.11, 64.78) * mm, "end": v(42.11, 58.56) * mm});
            skLineSegment(sketch, "E3.14.1.1", {"start": v(48.33, 58.56) * mm, "end": v(42.11, 58.56) * mm});
            skLineSegment(sketch, "E3.14.1.2", {"start": v(48.33, 64.78) * mm, "end": v(48.33, 58.56) * mm});
            skLineSegment(sketch, "E3.14.1.3", {"start": v(48.33, 64.78) * mm, "end": v(42.11, 64.78) * mm});
            skLineSegment(sketch, "E3.14.2.0", {"start": v(42.11, 56.56) * mm, "end": v(42.11, 50.33) * mm});
            skLineSegment(sketch, "E3.14.2.1", {"start": v(48.33, 50.33) * mm, "end": v(42.11, 50.33) * mm});
            skLineSegment(sketch, "E3.14.2.2", {"start": v(48.33, 56.56) * mm, "end": v(48.33, 50.33) * mm});
            skLineSegment(sketch, "E3.14.2.3", {"start": v(48.33, 56.56) * mm, "end": v(42.11, 56.56) * mm});
            skLineSegment(sketch, "E3.14.3.0", {"start": v(42.11, 48.33) * mm, "end": v(42.11, 42.11) * mm});
            skLineSegment(sketch, "E3.14.3.1", {"start": v(48.33, 42.11) * mm, "end": v(42.11, 42.11) * mm});
            skLineSegment(sketch, "E3.14.3.2", {"start": v(48.33, 48.33) * mm, "end": v(48.33, 42.11) * mm});
            skLineSegment(sketch, "E3.14.3.3", {"start": v(48.33, 48.33) * mm, "end": v(42.11, 48.33) * mm});
            skLineSegment(sketch, "E3.14.4.0", {"start": v(42.11, 40.11) * mm, "end": v(42.11, 33.89) * mm});
            skLineSegment(sketch, "E3.14.4.1", {"start": v(48.33, 33.89) * mm, "end": v(42.11, 33.89) * mm});
            skLineSegment(sketch, "E3.14.4.2", {"start": v(48.33, 40.11) * mm, "end": v(48.33, 33.89) * mm});
            skLineSegment(sketch, "E3.14.4.3", {"start": v(48.33, 40.11) * mm, "end": v(42.11, 40.11) * mm});
            skLineSegment(sketch, "E3.14.5.0", {"start": v(42.11, 31.89) * mm, "end": v(42.11, 25.67) * mm});
            skLineSegment(sketch, "E3.14.5.1", {"start": v(48.33, 25.67) * mm, "end": v(42.11, 25.67) * mm});
            skLineSegment(sketch, "E3.14.5.2", {"start": v(48.33, 31.89) * mm, "end": v(48.33, 25.67) * mm});
            skLineSegment(sketch, "E3.14.5.3", {"start": v(48.33, 31.89) * mm, "end": v(42.11, 31.89) * mm});
            skLineSegment(sketch, "E3.14.6.0", {"start": v(42.11, 23.67) * mm, "end": v(42.11, 17.44) * mm});
            skLineSegment(sketch, "E3.14.6.1", {"start": v(48.33, 17.44) * mm, "end": v(42.11, 17.44) * mm});
            skLineSegment(sketch, "E3.14.6.2", {"start": v(48.33, 23.67) * mm, "end": v(48.33, 17.44) * mm});
            skLineSegment(sketch, "E3.14.6.3", {"start": v(48.33, 23.67) * mm, "end": v(42.11, 23.67) * mm});
            skLineSegment(sketch, "E3.14.7.0", {"start": v(42.11, 15.44) * mm, "end": v(42.11, 9.22) * mm});
            skLineSegment(sketch, "E3.14.7.1", {"start": v(48.33, 9.22) * mm, "end": v(42.11, 9.22) * mm});
            skLineSegment(sketch, "E3.14.7.2", {"start": v(48.33, 15.44) * mm, "end": v(48.33, 9.22) * mm});
            skLineSegment(sketch, "E3.14.7.3", {"start": v(48.33, 15.44) * mm, "end": v(42.11, 15.44) * mm});
            skLineSegment(sketch, "E3.14.8.0", {"start": v(42.11, 7.22) * mm, "end": v(42.11, 1) * mm});
            skLineSegment(sketch, "E3.14.8.1", {"start": v(48.33, 1) * mm, "end": v(42.11, 1) * mm});
            skLineSegment(sketch, "E3.14.8.2", {"start": v(48.33, 7.22) * mm, "end": v(48.33, 1) * mm});
            skLineSegment(sketch, "E3.14.8.3", {"start": v(48.33, 7.22) * mm, "end": v(42.11, 7.22) * mm});
            skLineSegment(sketch, "E3.14.9.0", {"start": v(42.11, -1) * mm, "end": v(42.11, -7.22) * mm});
            skLineSegment(sketch, "E3.14.9.1", {"start": v(48.33, -7.22) * mm, "end": v(42.11, -7.22) * mm});
            skLineSegment(sketch, "E3.14.9.2", {"start": v(48.33, -1) * mm, "end": v(48.33, -7.22) * mm});
            skLineSegment(sketch, "E3.14.9.3", {"start": v(48.33, -1) * mm, "end": v(42.11, -1) * mm});
            skLineSegment(sketch, "E3.14.10.0", {"start": v(42.11, -9.22) * mm, "end": v(42.11, -15.44) * mm});
            skLineSegment(sketch, "E3.14.10.1", {"start": v(48.33, -15.44) * mm, "end": v(42.11, -15.44) * mm});
            skLineSegment(sketch, "E3.14.10.2", {"start": v(48.33, -9.22) * mm, "end": v(48.33, -15.44) * mm});
            skLineSegment(sketch, "E3.14.10.3", {"start": v(48.33, -9.22) * mm, "end": v(42.11, -9.22) * mm});
            skLineSegment(sketch, "E3.14.11.0", {"start": v(42.11, -17.44) * mm, "end": v(42.11, -23.67) * mm});
            skLineSegment(sketch, "E3.14.11.1", {"start": v(48.33, -23.67) * mm, "end": v(42.11, -23.67) * mm});
            skLineSegment(sketch, "E3.14.11.2", {"start": v(48.33, -17.44) * mm, "end": v(48.33, -23.67) * mm});
            skLineSegment(sketch, "E3.14.11.3", {"start": v(48.33, -17.44) * mm, "end": v(42.11, -17.44) * mm});
            skLineSegment(sketch, "E3.14.12.0", {"start": v(42.11, -25.67) * mm, "end": v(42.11, -31.89) * mm});
            skLineSegment(sketch, "E3.14.12.1", {"start": v(48.33, -31.89) * mm, "end": v(42.11, -31.89) * mm});
            skLineSegment(sketch, "E3.14.12.2", {"start": v(48.33, -25.67) * mm, "end": v(48.33, -31.89) * mm});
            skLineSegment(sketch, "E3.14.12.3", {"start": v(48.33, -25.67) * mm, "end": v(42.11, -25.67) * mm});
            skLineSegment(sketch, "E3.14.13.0", {"start": v(42.11, -33.89) * mm, "end": v(42.11, -40.11) * mm});
            skLineSegment(sketch, "E3.14.13.1", {"start": v(48.33, -40.11) * mm, "end": v(42.11, -40.11) * mm});
            skLineSegment(sketch, "E3.14.13.2", {"start": v(48.33, -33.89) * mm, "end": v(48.33, -40.11) * mm});
            skLineSegment(sketch, "E3.14.13.3", {"start": v(48.33, -33.89) * mm, "end": v(42.11, -33.89) * mm});
            skLineSegment(sketch, "E3.14.14.0", {"start": v(42.11, -42.11) * mm, "end": v(42.11, -48.33) * mm});
            skLineSegment(sketch, "E3.14.14.1", {"start": v(48.33, -48.33) * mm, "end": v(42.11, -48.33) * mm});
            skLineSegment(sketch, "E3.14.14.2", {"start": v(48.33, -42.11) * mm, "end": v(48.33, -48.33) * mm});
            skLineSegment(sketch, "E3.14.14.3", {"start": v(48.33, -42.11) * mm, "end": v(42.11, -42.11) * mm});
            skLineSegment(sketch, "E3.14.15.0", {"start": v(42.11, -50.33) * mm, "end": v(42.11, -56.56) * mm});
            skLineSegment(sketch, "E3.14.15.1", {"start": v(48.33, -56.56) * mm, "end": v(42.11, -56.56) * mm});
            skLineSegment(sketch, "E3.14.15.2", {"start": v(48.33, -50.33) * mm, "end": v(48.33, -56.56) * mm});
            skLineSegment(sketch, "E3.14.15.3", {"start": v(48.33, -50.33) * mm, "end": v(42.11, -50.33) * mm});
            skLineSegment(sketch, "E3.14.16.0", {"start": v(42.11, -58.56) * mm, "end": v(42.11, -64.78) * mm});
            skLineSegment(sketch, "E3.14.16.1", {"start": v(48.33, -64.78) * mm, "end": v(42.11, -64.78) * mm});
            skLineSegment(sketch, "E3.14.16.2", {"start": v(48.33, -58.56) * mm, "end": v(48.33, -64.78) * mm});
            skLineSegment(sketch, "E3.14.16.3", {"start": v(48.33, -58.56) * mm, "end": v(42.11, -58.56) * mm});
            skLineSegment(sketch, "E3.14.17.0", {"start": v(42.11, -66.78) * mm, "end": v(42.11, -73) * mm});
            skLineSegment(sketch, "E3.14.17.1", {"start": v(48.33, -73) * mm, "end": v(42.11, -73) * mm});
            skLineSegment(sketch, "E3.14.17.2", {"start": v(48.33, -66.78) * mm, "end": v(48.33, -73) * mm});
            skLineSegment(sketch, "E3.14.17.3", {"start": v(48.33, -66.78) * mm, "end": v(42.11, -66.78) * mm});
            skLineSegment(sketch, "E3.15.0.0", {"start": v(50.33, 73) * mm, "end": v(50.33, 66.78) * mm});
            skLineSegment(sketch, "E3.15.0.1", {"start": v(56.56, 66.78) * mm, "end": v(50.33, 66.78) * mm});
            skLineSegment(sketch, "E3.15.0.2", {"start": v(56.56, 73) * mm, "end": v(56.56, 66.78) * mm});
            skLineSegment(sketch, "E3.15.0.3", {"start": v(56.56, 73) * mm, "end": v(50.33, 73) * mm});
            skLineSegment(sketch, "E3.15.1.0", {"start": v(50.33, 64.78) * mm, "end": v(50.33, 58.56) * mm});
            skLineSegment(sketch, "E3.15.1.1", {"start": v(56.56, 58.56) * mm, "end": v(50.33, 58.56) * mm});
            skLineSegment(sketch, "E3.15.1.2", {"start": v(56.56, 64.78) * mm, "end": v(56.56, 58.56) * mm});
            skLineSegment(sketch, "E3.15.1.3", {"start": v(56.56, 64.78) * mm, "end": v(50.33, 64.78) * mm});
            skLineSegment(sketch, "E3.15.2.0", {"start": v(50.33, 56.56) * mm, "end": v(50.33, 50.33) * mm});
            skLineSegment(sketch, "E3.15.2.1", {"start": v(56.56, 50.33) * mm, "end": v(50.33, 50.33) * mm});
            skLineSegment(sketch, "E3.15.2.2", {"start": v(56.56, 56.56) * mm, "end": v(56.56, 50.33) * mm});
            skLineSegment(sketch, "E3.15.2.3", {"start": v(56.56, 56.56) * mm, "end": v(50.33, 56.56) * mm});
            skLineSegment(sketch, "E3.15.3.0", {"start": v(50.33, 48.33) * mm, "end": v(50.33, 42.11) * mm});
            skLineSegment(sketch, "E3.15.3.1", {"start": v(56.56, 42.11) * mm, "end": v(50.33, 42.11) * mm});
            skLineSegment(sketch, "E3.15.3.2", {"start": v(56.56, 48.33) * mm, "end": v(56.56, 42.11) * mm});
            skLineSegment(sketch, "E3.15.3.3", {"start": v(56.56, 48.33) * mm, "end": v(50.33, 48.33) * mm});
            skLineSegment(sketch, "E3.15.4.0", {"start": v(50.33, 40.11) * mm, "end": v(50.33, 33.89) * mm});
            skLineSegment(sketch, "E3.15.4.1", {"start": v(56.56, 33.89) * mm, "end": v(50.33, 33.89) * mm});
            skLineSegment(sketch, "E3.15.4.2", {"start": v(56.56, 40.11) * mm, "end": v(56.56, 33.89) * mm});
            skLineSegment(sketch, "E3.15.4.3", {"start": v(56.56, 40.11) * mm, "end": v(50.33, 40.11) * mm});
            skLineSegment(sketch, "E3.15.5.0", {"start": v(50.33, 31.89) * mm, "end": v(50.33, 25.67) * mm});
            skLineSegment(sketch, "E3.15.5.1", {"start": v(56.56, 25.67) * mm, "end": v(50.33, 25.67) * mm});
            skLineSegment(sketch, "E3.15.5.2", {"start": v(56.56, 31.89) * mm, "end": v(56.56, 25.67) * mm});
            skLineSegment(sketch, "E3.15.5.3", {"start": v(56.56, 31.89) * mm, "end": v(50.33, 31.89) * mm});
            skLineSegment(sketch, "E3.15.6.0", {"start": v(50.33, 23.67) * mm, "end": v(50.33, 17.44) * mm});
            skLineSegment(sketch, "E3.15.6.1", {"start": v(56.56, 17.44) * mm, "end": v(50.33, 17.44) * mm});
            skLineSegment(sketch, "E3.15.6.2", {"start": v(56.56, 23.67) * mm, "end": v(56.56, 17.44) * mm});
            skLineSegment(sketch, "E3.15.6.3", {"start": v(56.56, 23.67) * mm, "end": v(50.33, 23.67) * mm});
            skLineSegment(sketch, "E3.15.7.0", {"start": v(50.33, 15.44) * mm, "end": v(50.33, 9.22) * mm});
            skLineSegment(sketch, "E3.15.7.1", {"start": v(56.56, 9.22) * mm, "end": v(50.33, 9.22) * mm});
            skLineSegment(sketch, "E3.15.7.2", {"start": v(56.56, 15.44) * mm, "end": v(56.56, 9.22) * mm});
            skLineSegment(sketch, "E3.15.7.3", {"start": v(56.56, 15.44) * mm, "end": v(50.33, 15.44) * mm});
            skLineSegment(sketch, "E3.15.8.0", {"start": v(50.33, 7.22) * mm, "end": v(50.33, 1) * mm});
            skLineSegment(sketch, "E3.15.8.1", {"start": v(56.56, 1) * mm, "end": v(50.33, 1) * mm});
            skLineSegment(sketch, "E3.15.8.2", {"start": v(56.56, 7.22) * mm, "end": v(56.56, 1) * mm});
            skLineSegment(sketch, "E3.15.8.3", {"start": v(56.56, 7.22) * mm, "end": v(50.33, 7.22) * mm});
            skLineSegment(sketch, "E3.15.9.0", {"start": v(50.33, -1) * mm, "end": v(50.33, -7.22) * mm});
            skLineSegment(sketch, "E3.15.9.1", {"start": v(56.56, -7.22) * mm, "end": v(50.33, -7.22) * mm});
            skLineSegment(sketch, "E3.15.9.2", {"start": v(56.56, -1) * mm, "end": v(56.56, -7.22) * mm});
            skLineSegment(sketch, "E3.15.9.3", {"start": v(56.56, -1) * mm, "end": v(50.33, -1) * mm});
            skLineSegment(sketch, "E3.15.10.0", {"start": v(50.33, -9.22) * mm, "end": v(50.33, -15.44) * mm});
            skLineSegment(sketch, "E3.15.10.1", {"start": v(56.56, -15.44) * mm, "end": v(50.33, -15.44) * mm});
            skLineSegment(sketch, "E3.15.10.2", {"start": v(56.56, -9.22) * mm, "end": v(56.56, -15.44) * mm});
            skLineSegment(sketch, "E3.15.10.3", {"start": v(56.56, -9.22) * mm, "end": v(50.33, -9.22) * mm});
            skLineSegment(sketch, "E3.15.11.0", {"start": v(50.33, -17.44) * mm, "end": v(50.33, -23.67) * mm});
            skLineSegment(sketch, "E3.15.11.1", {"start": v(56.56, -23.67) * mm, "end": v(50.33, -23.67) * mm});
            skLineSegment(sketch, "E3.15.11.2", {"start": v(56.56, -17.44) * mm, "end": v(56.56, -23.67) * mm});
            skLineSegment(sketch, "E3.15.11.3", {"start": v(56.56, -17.44) * mm, "end": v(50.33, -17.44) * mm});
            skLineSegment(sketch, "E3.15.12.0", {"start": v(50.33, -25.67) * mm, "end": v(50.33, -31.89) * mm});
            skLineSegment(sketch, "E3.15.12.1", {"start": v(56.56, -31.89) * mm, "end": v(50.33, -31.89) * mm});
            skLineSegment(sketch, "E3.15.12.2", {"start": v(56.56, -25.67) * mm, "end": v(56.56, -31.89) * mm});
            skLineSegment(sketch, "E3.15.12.3", {"start": v(56.56, -25.67) * mm, "end": v(50.33, -25.67) * mm});
            skLineSegment(sketch, "E3.15.13.0", {"start": v(50.33, -33.89) * mm, "end": v(50.33, -40.11) * mm});
            skLineSegment(sketch, "E3.15.13.1", {"start": v(56.56, -40.11) * mm, "end": v(50.33, -40.11) * mm});
            skLineSegment(sketch, "E3.15.13.2", {"start": v(56.56, -33.89) * mm, "end": v(56.56, -40.11) * mm});
            skLineSegment(sketch, "E3.15.13.3", {"start": v(56.56, -33.89) * mm, "end": v(50.33, -33.89) * mm});
            skLineSegment(sketch, "E3.15.14.0", {"start": v(50.33, -42.11) * mm, "end": v(50.33, -48.33) * mm});
            skLineSegment(sketch, "E3.15.14.1", {"start": v(56.56, -48.33) * mm, "end": v(50.33, -48.33) * mm});
            skLineSegment(sketch, "E3.15.14.2", {"start": v(56.56, -42.11) * mm, "end": v(56.56, -48.33) * mm});
            skLineSegment(sketch, "E3.15.14.3", {"start": v(56.56, -42.11) * mm, "end": v(50.33, -42.11) * mm});
            skLineSegment(sketch, "E3.15.15.0", {"start": v(50.33, -50.33) * mm, "end": v(50.33, -56.56) * mm});
            skLineSegment(sketch, "E3.15.15.1", {"start": v(56.56, -56.56) * mm, "end": v(50.33, -56.56) * mm});
            skLineSegment(sketch, "E3.15.15.2", {"start": v(56.56, -50.33) * mm, "end": v(56.56, -56.56) * mm});
            skLineSegment(sketch, "E3.15.15.3", {"start": v(56.56, -50.33) * mm, "end": v(50.33, -50.33) * mm});
            skLineSegment(sketch, "E3.15.16.0", {"start": v(50.33, -58.56) * mm, "end": v(50.33, -64.78) * mm});
            skLineSegment(sketch, "E3.15.16.1", {"start": v(56.56, -64.78) * mm, "end": v(50.33, -64.78) * mm});
            skLineSegment(sketch, "E3.15.16.2", {"start": v(56.56, -58.56) * mm, "end": v(56.56, -64.78) * mm});
            skLineSegment(sketch, "E3.15.16.3", {"start": v(56.56, -58.56) * mm, "end": v(50.33, -58.56) * mm});
            skLineSegment(sketch, "E3.15.17.0", {"start": v(50.33, -66.78) * mm, "end": v(50.33, -73) * mm});
            skLineSegment(sketch, "E3.15.17.1", {"start": v(56.56, -73) * mm, "end": v(50.33, -73) * mm});
            skLineSegment(sketch, "E3.15.17.2", {"start": v(56.56, -66.78) * mm, "end": v(56.56, -73) * mm});
            skLineSegment(sketch, "E3.15.17.3", {"start": v(56.56, -66.78) * mm, "end": v(50.33, -66.78) * mm});
            skLineSegment(sketch, "E3.16.0.0", {"start": v(58.56, 73) * mm, "end": v(58.56, 66.78) * mm});
            skLineSegment(sketch, "E3.16.0.1", {"start": v(64.78, 66.78) * mm, "end": v(58.56, 66.78) * mm});
            skLineSegment(sketch, "E3.16.0.2", {"start": v(64.78, 73) * mm, "end": v(64.78, 66.78) * mm});
            skLineSegment(sketch, "E3.16.0.3", {"start": v(64.78, 73) * mm, "end": v(58.56, 73) * mm});
            skLineSegment(sketch, "E3.16.1.0", {"start": v(58.56, 64.78) * mm, "end": v(58.56, 58.56) * mm});
            skLineSegment(sketch, "E3.16.1.1", {"start": v(64.78, 58.56) * mm, "end": v(58.56, 58.56) * mm});
            skLineSegment(sketch, "E3.16.1.2", {"start": v(64.78, 64.78) * mm, "end": v(64.78, 58.56) * mm});
            skLineSegment(sketch, "E3.16.1.3", {"start": v(64.78, 64.78) * mm, "end": v(58.56, 64.78) * mm});
            skLineSegment(sketch, "E3.16.2.0", {"start": v(58.56, 56.56) * mm, "end": v(58.56, 50.33) * mm});
            skLineSegment(sketch, "E3.16.2.1", {"start": v(64.78, 50.33) * mm, "end": v(58.56, 50.33) * mm});
            skLineSegment(sketch, "E3.16.2.2", {"start": v(64.78, 56.56) * mm, "end": v(64.78, 50.33) * mm});
            skLineSegment(sketch, "E3.16.2.3", {"start": v(64.78, 56.56) * mm, "end": v(58.56, 56.56) * mm});
            skLineSegment(sketch, "E3.16.3.0", {"start": v(58.56, 48.33) * mm, "end": v(58.56, 42.11) * mm});
            skLineSegment(sketch, "E3.16.3.1", {"start": v(64.78, 42.11) * mm, "end": v(58.56, 42.11) * mm});
            skLineSegment(sketch, "E3.16.3.2", {"start": v(64.78, 48.33) * mm, "end": v(64.78, 42.11) * mm});
            skLineSegment(sketch, "E3.16.3.3", {"start": v(64.78, 48.33) * mm, "end": v(58.56, 48.33) * mm});
            skLineSegment(sketch, "E3.16.4.0", {"start": v(58.56, 40.11) * mm, "end": v(58.56, 33.89) * mm});
            skLineSegment(sketch, "E3.16.4.1", {"start": v(64.78, 33.89) * mm, "end": v(58.56, 33.89) * mm});
            skLineSegment(sketch, "E3.16.4.2", {"start": v(64.78, 40.11) * mm, "end": v(64.78, 33.89) * mm});
            skLineSegment(sketch, "E3.16.4.3", {"start": v(64.78, 40.11) * mm, "end": v(58.56, 40.11) * mm});
            skLineSegment(sketch, "E3.16.5.0", {"start": v(58.56, 31.89) * mm, "end": v(58.56, 25.67) * mm});
            skLineSegment(sketch, "E3.16.5.1", {"start": v(64.78, 25.67) * mm, "end": v(58.56, 25.67) * mm});
            skLineSegment(sketch, "E3.16.5.2", {"start": v(64.78, 31.89) * mm, "end": v(64.78, 25.67) * mm});
            skLineSegment(sketch, "E3.16.5.3", {"start": v(64.78, 31.89) * mm, "end": v(58.56, 31.89) * mm});
            skLineSegment(sketch, "E3.16.6.0", {"start": v(58.56, 23.67) * mm, "end": v(58.56, 17.44) * mm});
            skLineSegment(sketch, "E3.16.6.1", {"start": v(64.78, 17.44) * mm, "end": v(58.56, 17.44) * mm});
            skLineSegment(sketch, "E3.16.6.2", {"start": v(64.78, 23.67) * mm, "end": v(64.78, 17.44) * mm});
            skLineSegment(sketch, "E3.16.6.3", {"start": v(64.78, 23.67) * mm, "end": v(58.56, 23.67) * mm});
            skLineSegment(sketch, "E3.16.7.0", {"start": v(58.56, 15.44) * mm, "end": v(58.56, 9.22) * mm});
            skLineSegment(sketch, "E3.16.7.1", {"start": v(64.78, 9.22) * mm, "end": v(58.56, 9.22) * mm});
            skLineSegment(sketch, "E3.16.7.2", {"start": v(64.78, 15.44) * mm, "end": v(64.78, 9.22) * mm});
            skLineSegment(sketch, "E3.16.7.3", {"start": v(64.78, 15.44) * mm, "end": v(58.56, 15.44) * mm});
            skLineSegment(sketch, "E3.16.8.0", {"start": v(58.56, 7.22) * mm, "end": v(58.56, 1) * mm});
            skLineSegment(sketch, "E3.16.8.1", {"start": v(64.78, 1) * mm, "end": v(58.56, 1) * mm});
            skLineSegment(sketch, "E3.16.8.2", {"start": v(64.78, 7.22) * mm, "end": v(64.78, 1) * mm});
            skLineSegment(sketch, "E3.16.8.3", {"start": v(64.78, 7.22) * mm, "end": v(58.56, 7.22) * mm});
            skLineSegment(sketch, "E3.16.9.0", {"start": v(58.56, -1) * mm, "end": v(58.56, -7.22) * mm});
            skLineSegment(sketch, "E3.16.9.1", {"start": v(64.78, -7.22) * mm, "end": v(58.56, -7.22) * mm});
            skLineSegment(sketch, "E3.16.9.2", {"start": v(64.78, -1) * mm, "end": v(64.78, -7.22) * mm});
            skLineSegment(sketch, "E3.16.9.3", {"start": v(64.78, -1) * mm, "end": v(58.56, -1) * mm});
            skLineSegment(sketch, "E3.16.10.0", {"start": v(58.56, -9.22) * mm, "end": v(58.56, -15.44) * mm});
            skLineSegment(sketch, "E3.16.10.1", {"start": v(64.78, -15.44) * mm, "end": v(58.56, -15.44) * mm});
            skLineSegment(sketch, "E3.16.10.2", {"start": v(64.78, -9.22) * mm, "end": v(64.78, -15.44) * mm});
            skLineSegment(sketch, "E3.16.10.3", {"start": v(64.78, -9.22) * mm, "end": v(58.56, -9.22) * mm});
            skLineSegment(sketch, "E3.16.11.0", {"start": v(58.56, -17.44) * mm, "end": v(58.56, -23.67) * mm});
            skLineSegment(sketch, "E3.16.11.1", {"start": v(64.78, -23.67) * mm, "end": v(58.56, -23.67) * mm});
            skLineSegment(sketch, "E3.16.11.2", {"start": v(64.78, -17.44) * mm, "end": v(64.78, -23.67) * mm});
            skLineSegment(sketch, "E3.16.11.3", {"start": v(64.78, -17.44) * mm, "end": v(58.56, -17.44) * mm});
            skLineSegment(sketch, "E3.16.12.0", {"start": v(58.56, -25.67) * mm, "end": v(58.56, -31.89) * mm});
            skLineSegment(sketch, "E3.16.12.1", {"start": v(64.78, -31.89) * mm, "end": v(58.56, -31.89) * mm});
            skLineSegment(sketch, "E3.16.12.2", {"start": v(64.78, -25.67) * mm, "end": v(64.78, -31.89) * mm});
            skLineSegment(sketch, "E3.16.12.3", {"start": v(64.78, -25.67) * mm, "end": v(58.56, -25.67) * mm});
            skLineSegment(sketch, "E3.16.13.0", {"start": v(58.56, -33.89) * mm, "end": v(58.56, -40.11) * mm});
            skLineSegment(sketch, "E3.16.13.1", {"start": v(64.78, -40.11) * mm, "end": v(58.56, -40.11) * mm});
            skLineSegment(sketch, "E3.16.13.2", {"start": v(64.78, -33.89) * mm, "end": v(64.78, -40.11) * mm});
            skLineSegment(sketch, "E3.16.13.3", {"start": v(64.78, -33.89) * mm, "end": v(58.56, -33.89) * mm});
            skLineSegment(sketch, "E3.16.14.0", {"start": v(58.56, -42.11) * mm, "end": v(58.56, -48.33) * mm});
            skLineSegment(sketch, "E3.16.14.1", {"start": v(64.78, -48.33) * mm, "end": v(58.56, -48.33) * mm});
            skLineSegment(sketch, "E3.16.14.2", {"start": v(64.78, -42.11) * mm, "end": v(64.78, -48.33) * mm});
            skLineSegment(sketch, "E3.16.14.3", {"start": v(64.78, -42.11) * mm, "end": v(58.56, -42.11) * mm});
            skLineSegment(sketch, "E3.16.15.0", {"start": v(58.56, -50.33) * mm, "end": v(58.56, -56.56) * mm});
            skLineSegment(sketch, "E3.16.15.1", {"start": v(64.78, -56.56) * mm, "end": v(58.56, -56.56) * mm});
            skLineSegment(sketch, "E3.16.15.2", {"start": v(64.78, -50.33) * mm, "end": v(64.78, -56.56) * mm});
            skLineSegment(sketch, "E3.16.15.3", {"start": v(64.78, -50.33) * mm, "end": v(58.56, -50.33) * mm});
            skLineSegment(sketch, "E3.16.16.0", {"start": v(58.56, -58.56) * mm, "end": v(58.56, -64.78) * mm});
            skLineSegment(sketch, "E3.16.16.1", {"start": v(64.78, -64.78) * mm, "end": v(58.56, -64.78) * mm});
            skLineSegment(sketch, "E3.16.16.2", {"start": v(64.78, -58.56) * mm, "end": v(64.78, -64.78) * mm});
            skLineSegment(sketch, "E3.16.16.3", {"start": v(64.78, -58.56) * mm, "end": v(58.56, -58.56) * mm});
            skLineSegment(sketch, "E3.16.17.0", {"start": v(58.56, -66.78) * mm, "end": v(58.56, -73) * mm});
            skLineSegment(sketch, "E3.16.17.1", {"start": v(64.78, -73) * mm, "end": v(58.56, -73) * mm});
            skLineSegment(sketch, "E3.16.17.2", {"start": v(64.78, -66.78) * mm, "end": v(64.78, -73) * mm});
            skLineSegment(sketch, "E3.16.17.3", {"start": v(64.78, -66.78) * mm, "end": v(58.56, -66.78) * mm});
            skLineSegment(sketch, "E3.17.0.0", {"start": v(66.78, 73) * mm, "end": v(66.78, 66.78) * mm});
            skLineSegment(sketch, "E3.17.0.1", {"start": v(73, 66.78) * mm, "end": v(66.78, 66.78) * mm});
            skLineSegment(sketch, "E3.17.0.2", {"start": v(73, 73) * mm, "end": v(73, 66.78) * mm});
            skLineSegment(sketch, "E3.17.0.3", {"start": v(73, 73) * mm, "end": v(66.78, 73) * mm});
            skLineSegment(sketch, "E3.17.1.0", {"start": v(66.78, 64.78) * mm, "end": v(66.78, 58.56) * mm});
            skLineSegment(sketch, "E3.17.1.1", {"start": v(73, 58.56) * mm, "end": v(66.78, 58.56) * mm});
            skLineSegment(sketch, "E3.17.1.2", {"start": v(73, 64.78) * mm, "end": v(73, 58.56) * mm});
            skLineSegment(sketch, "E3.17.1.3", {"start": v(73, 64.78) * mm, "end": v(66.78, 64.78) * mm});
            skLineSegment(sketch, "E3.17.2.0", {"start": v(66.78, 56.56) * mm, "end": v(66.78, 50.33) * mm});
            skLineSegment(sketch, "E3.17.2.1", {"start": v(73, 50.33) * mm, "end": v(66.78, 50.33) * mm});
            skLineSegment(sketch, "E3.17.2.2", {"start": v(73, 56.56) * mm, "end": v(73, 50.33) * mm});
            skLineSegment(sketch, "E3.17.2.3", {"start": v(73, 56.56) * mm, "end": v(66.78, 56.56) * mm});
            skLineSegment(sketch, "E3.17.3.0", {"start": v(66.78, 48.33) * mm, "end": v(66.78, 42.11) * mm});
            skLineSegment(sketch, "E3.17.3.1", {"start": v(73, 42.11) * mm, "end": v(66.78, 42.11) * mm});
            skLineSegment(sketch, "E3.17.3.2", {"start": v(73, 48.33) * mm, "end": v(73, 42.11) * mm});
            skLineSegment(sketch, "E3.17.3.3", {"start": v(73, 48.33) * mm, "end": v(66.78, 48.33) * mm});
            skLineSegment(sketch, "E3.17.4.0", {"start": v(66.78, 40.11) * mm, "end": v(66.78, 33.89) * mm});
            skLineSegment(sketch, "E3.17.4.1", {"start": v(73, 33.89) * mm, "end": v(66.78, 33.89) * mm});
            skLineSegment(sketch, "E3.17.4.2", {"start": v(73, 40.11) * mm, "end": v(73, 33.89) * mm});
            skLineSegment(sketch, "E3.17.4.3", {"start": v(73, 40.11) * mm, "end": v(66.78, 40.11) * mm});
            skLineSegment(sketch, "E3.17.5.0", {"start": v(66.78, 31.89) * mm, "end": v(66.78, 25.67) * mm});
            skLineSegment(sketch, "E3.17.5.1", {"start": v(73, 25.67) * mm, "end": v(66.78, 25.67) * mm});
            skLineSegment(sketch, "E3.17.5.2", {"start": v(73, 31.89) * mm, "end": v(73, 25.67) * mm});
            skLineSegment(sketch, "E3.17.5.3", {"start": v(73, 31.89) * mm, "end": v(66.78, 31.89) * mm});
            skLineSegment(sketch, "E3.17.6.0", {"start": v(66.78, 23.67) * mm, "end": v(66.78, 17.44) * mm});
            skLineSegment(sketch, "E3.17.6.1", {"start": v(73, 17.44) * mm, "end": v(66.78, 17.44) * mm});
            skLineSegment(sketch, "E3.17.6.2", {"start": v(73, 23.67) * mm, "end": v(73, 17.44) * mm});
            skLineSegment(sketch, "E3.17.6.3", {"start": v(73, 23.67) * mm, "end": v(66.78, 23.67) * mm});
            skLineSegment(sketch, "E3.17.7.0", {"start": v(66.78, 15.44) * mm, "end": v(66.78, 9.22) * mm});
            skLineSegment(sketch, "E3.17.7.1", {"start": v(73, 9.22) * mm, "end": v(66.78, 9.22) * mm});
            skLineSegment(sketch, "E3.17.7.2", {"start": v(73, 15.44) * mm, "end": v(73, 9.22) * mm});
            skLineSegment(sketch, "E3.17.7.3", {"start": v(73, 15.44) * mm, "end": v(66.78, 15.44) * mm});
            skLineSegment(sketch, "E3.17.8.0", {"start": v(66.78, 7.22) * mm, "end": v(66.78, 1) * mm});
            skLineSegment(sketch, "E3.17.8.1", {"start": v(73, 1) * mm, "end": v(66.78, 1) * mm});
            skLineSegment(sketch, "E3.17.8.2", {"start": v(73, 7.22) * mm, "end": v(73, 1) * mm});
            skLineSegment(sketch, "E3.17.8.3", {"start": v(73, 7.22) * mm, "end": v(66.78, 7.22) * mm});
            skLineSegment(sketch, "E3.17.9.0", {"start": v(66.78, -1) * mm, "end": v(66.78, -7.22) * mm});
            skLineSegment(sketch, "E3.17.9.1", {"start": v(73, -7.22) * mm, "end": v(66.78, -7.22) * mm});
            skLineSegment(sketch, "E3.17.9.2", {"start": v(73, -1) * mm, "end": v(73, -7.22) * mm});
            skLineSegment(sketch, "E3.17.9.3", {"start": v(73, -1) * mm, "end": v(66.78, -1) * mm});
            skLineSegment(sketch, "E3.17.10.0", {"start": v(66.78, -9.22) * mm, "end": v(66.78, -15.44) * mm});
            skLineSegment(sketch, "E3.17.10.1", {"start": v(73, -15.44) * mm, "end": v(66.78, -15.44) * mm});
            skLineSegment(sketch, "E3.17.10.2", {"start": v(73, -9.22) * mm, "end": v(73, -15.44) * mm});
            skLineSegment(sketch, "E3.17.10.3", {"start": v(73, -9.22) * mm, "end": v(66.78, -9.22) * mm});
            skLineSegment(sketch, "E3.17.11.0", {"start": v(66.78, -17.44) * mm, "end": v(66.78, -23.67) * mm});
            skLineSegment(sketch, "E3.17.11.1", {"start": v(73, -23.67) * mm, "end": v(66.78, -23.67) * mm});
            skLineSegment(sketch, "E3.17.11.2", {"start": v(73, -17.44) * mm, "end": v(73, -23.67) * mm});
            skLineSegment(sketch, "E3.17.11.3", {"start": v(73, -17.44) * mm, "end": v(66.78, -17.44) * mm});
            skLineSegment(sketch, "E3.17.12.0", {"start": v(66.78, -25.67) * mm, "end": v(66.78, -31.89) * mm});
            skLineSegment(sketch, "E3.17.12.1", {"start": v(73, -31.89) * mm, "end": v(66.78, -31.89) * mm});
            skLineSegment(sketch, "E3.17.12.2", {"start": v(73, -25.67) * mm, "end": v(73, -31.89) * mm});
            skLineSegment(sketch, "E3.17.12.3", {"start": v(73, -25.67) * mm, "end": v(66.78, -25.67) * mm});
            skLineSegment(sketch, "E3.17.13.0", {"start": v(66.78, -33.89) * mm, "end": v(66.78, -40.11) * mm});
            skLineSegment(sketch, "E3.17.13.1", {"start": v(73, -40.11) * mm, "end": v(66.78, -40.11) * mm});
            skLineSegment(sketch, "E3.17.13.2", {"start": v(73, -33.89) * mm, "end": v(73, -40.11) * mm});
            skLineSegment(sketch, "E3.17.13.3", {"start": v(73, -33.89) * mm, "end": v(66.78, -33.89) * mm});
            skLineSegment(sketch, "E3.17.14.0", {"start": v(66.78, -42.11) * mm, "end": v(66.78, -48.33) * mm});
            skLineSegment(sketch, "E3.17.14.1", {"start": v(73, -48.33) * mm, "end": v(66.78, -48.33) * mm});
            skLineSegment(sketch, "E3.17.14.2", {"start": v(73, -42.11) * mm, "end": v(73, -48.33) * mm});
            skLineSegment(sketch, "E3.17.14.3", {"start": v(73, -42.11) * mm, "end": v(66.78, -42.11) * mm});
            skLineSegment(sketch, "E3.17.15.0", {"start": v(66.78, -50.33) * mm, "end": v(66.78, -56.56) * mm});
            skLineSegment(sketch, "E3.17.15.1", {"start": v(73, -56.56) * mm, "end": v(66.78, -56.56) * mm});
            skLineSegment(sketch, "E3.17.15.2", {"start": v(73, -50.33) * mm, "end": v(73, -56.56) * mm});
            skLineSegment(sketch, "E3.17.15.3", {"start": v(73, -50.33) * mm, "end": v(66.78, -50.33) * mm});
            skLineSegment(sketch, "E3.17.16.0", {"start": v(66.78, -58.56) * mm, "end": v(66.78, -64.78) * mm});
            skLineSegment(sketch, "E3.17.16.1", {"start": v(73, -64.78) * mm, "end": v(66.78, -64.78) * mm});
            skLineSegment(sketch, "E3.17.16.2", {"start": v(73, -58.56) * mm, "end": v(73, -64.78) * mm});
            skLineSegment(sketch, "E3.17.16.3", {"start": v(73, -58.56) * mm, "end": v(66.78, -58.56) * mm});
            skLineSegment(sketch, "E3.17.17.0", {"start": v(66.78, -66.78) * mm, "end": v(66.78, -73) * mm});
            skLineSegment(sketch, "E3.17.17.1", {"start": v(73, -73) * mm, "end": v(66.78, -73) * mm});
            skLineSegment(sketch, "E3.17.17.2", {"start": v(73, -66.78) * mm, "end": v(73, -73) * mm});
            skLineSegment(sketch, "E3.17.17.3", {"start": v(73, -66.78) * mm, "end": v(66.78, -66.78) * mm});
            skLineSegment(sketch, "E3.direction1", {"start": v(-73, 66.78) * mm, "end": v(-64.78, 66.78) * mm, "construction": true});
            skLineSegment(sketch, "E3.direction2", {"start": v(-73, 66.78) * mm, "end": v(-73, 58.56) * mm, "construction": true});
            skSolve(sketch);
        }
        {
            var Q0;
            Q0 = qSketchRegion(id + "F4", true);
            extrude(context, id + "F5", {"entities" : qUnion([Q0]), "operationType" : NewBodyOperationType.ADD, "depth" : 1 * mm});
        }
        {
            var Q0;
            Q0=makeQuery(id+"F1.opExtrude","CAP_FACE",FACE,{"disambiguationData":[OSD([sQuery(id+"F0.wireOp",EDGE,"E0.bottom"),sQuery(id+"F0.wireOp",EDGE,"E0.top"),sQuery(id+"F0.wireOp",EDGE,"E0.left"),sQuery(id+"F0.wireOp",EDGE,"E0.right")])],"isStart":false});
            var sketch = newSketch(context, id + "F6", { "sketchPlane" : qUnion([Q0])});
            skCircle(sketch, "E4", {"center": v(-49.33, 49.33) * mm, "radius": 1.25 * mm});
            skCircle(sketch, "E5.0.1.0", {"center": v(-49.33, 0) * mm, "radius": 1.25 * mm});
            skCircle(sketch, "E5.0.2.0", {"center": v(-49.33, -49.33) * mm, "radius": 1.25 * mm});
            skCircle(sketch, "E5.1.0.0", {"center": v(0, 49.33) * mm, "radius": 1.25 * mm});
            skCircle(sketch, "E5.1.1.0", {"center": v(0, 0) * mm, "radius": 1.25 * mm});
            skCircle(sketch, "E5.1.2.0", {"center": v(0, -49.33) * mm, "radius": 1.25 * mm});
            skCircle(sketch, "E5.2.0.0", {"center": v(49.33, 49.33) * mm, "radius": 1.25 * mm});
            skCircle(sketch, "E5.2.1.0", {"center": v(49.33, 0) * mm, "radius": 1.25 * mm});
            skCircle(sketch, "E5.2.2.0", {"center": v(49.33, -49.33) * mm, "radius": 1.25 * mm});
            skLineSegment(sketch, "E5.direction1", {"start": v(-49.33, 49.33) * mm, "end": v(0, 49.33) * mm, "construction": true});
            skLineSegment(sketch, "E5.direction2", {"start": v(-49.33, 49.33) * mm, "end": v(-49.33, 0) * mm, "construction": true});
            skSolve(sketch);
        }
        {
            var Q0;
            Q0=makeQuery(id+"F10.boolean.opBoolean","MERGE",FACE,{"derivedFrom":[makeQuery(id+"F1.opExtrude","CAP_FACE",FACE,{"disambiguationData":[OSD([sQuery(id+"F0.wireOp",EDGE,"E0.bottom"),sQuery(id+"F0.wireOp",EDGE,"E0.top"),sQuery(id+"F0.wireOp",EDGE,"E0.left"),sQuery(id+"F0.wireOp",EDGE,"E0.right")])],"isStart":false}),makeQuery(id+"F10.opExtrude","CAP_FACE",FACE,{"disambiguationData":[OSD([sQuery(id+"F6.wireOp",EDGE,"SSSCFJ4h-9EXo-NQlt-ujyr-DV0z3uI3B6aU")])],"isStart":false})]});
            var sketch = newSketch(context, id + "F7", { "sketchPlane" : qUnion([Q0])});
            skCircle(sketch, "E6", {"center": v(-49.33, 49.33) * mm, "radius": 1.75 * mm});
            skCircle(sketch, "E7.0.1.0", {"center": v(-49.33, 0) * mm, "radius": 1.75 * mm});
            skCircle(sketch, "E7.0.2.0", {"center": v(-49.33, -49.33) * mm, "radius": 1.75 * mm});
            skCircle(sketch, "E7.1.0.0", {"center": v(0, 49.33) * mm, "radius": 1.75 * mm});
            skCircle(sketch, "E7.1.1.0", {"center": v(0, 0) * mm, "radius": 1.75 * mm});
            skCircle(sketch, "E7.1.2.0", {"center": v(0, -49.33) * mm, "radius": 1.75 * mm});
            skCircle(sketch, "E7.2.0.0", {"center": v(49.33, 49.33) * mm, "radius": 1.75 * mm});
            skCircle(sketch, "E7.2.1.0", {"center": v(49.33, 0) * mm, "radius": 1.75 * mm});
            skCircle(sketch, "E7.2.2.0", {"center": v(49.33, -49.33) * mm, "radius": 1.75 * mm});
            skLineSegment(sketch, "E7.direction1", {"start": v(-49.33, 49.33) * mm, "end": v(0, 49.33) * mm, "construction": true});
            skLineSegment(sketch, "E7.direction2", {"start": v(-49.33, 49.33) * mm, "end": v(-49.33, 0) * mm, "construction": true});
            skSolve(sketch);
        }
        {
            var Q0;
            Q0 = qSketchRegion(id + "F7", true);
            extrude(context, id + "F8", {"entities" : qUnion([Q0]), "operationType" : NewBodyOperationType.ADD, "depth" : 1 * mm});
        }
        {
            var Q0;
            Q0 = qSketchRegion(id + "F7", true);
            extrude(context, id + "F9", {"entities" : qUnion([Q0]), "operationType" : NewBodyOperationType.REMOVE, "depth" : 1 * mm});
        }
        {
            var Q0;
            Q0 = qSketchRegion(id + "F6", true);
            extrude(context, id + "F10", {"entities" : qUnion([Q0]), "operationType" : NewBodyOperationType.ADD, "depth" : 1 * mm});
        }
        {
            var Q0;
            Q0=makeQuery(id+"F10.opExtrude","CAP_EDGE",EDGE,{"disambiguationData":[OSD([sQuery(id+"F6.wireOp",EDGE,"E5.0.2.0")])],"isStart":false});
            var Q1;
            Q1=makeQuery(id+"F10.opExtrude","CAP_EDGE",EDGE,{"disambiguationData":[OSD([sQuery(id+"F6.wireOp",EDGE,"E5.1.2.0")])],"isStart":false});
            var Q2;
            Q2=makeQuery(id+"F10.opExtrude","CAP_EDGE",EDGE,{"disambiguationData":[OSD([sQuery(id+"F6.wireOp",EDGE,"E5.2.2.0")])],"isStart":false});
            var Q3;
            Q3=makeQuery(id+"F10.opExtrude","CAP_EDGE",EDGE,{"disambiguationData":[OSD([sQuery(id+"F6.wireOp",EDGE,"E5.1.1.0")])],"isStart":false});
            var Q4;
            Q4=makeQuery(id+"F10.opExtrude","CAP_EDGE",EDGE,{"disambiguationData":[OSD([sQuery(id+"F6.wireOp",EDGE,"E5.0.1.0")])],"isStart":false});
            var Q5;
            Q5=makeQuery(id+"F10.opExtrude","CAP_EDGE",EDGE,{"disambiguationData":[OSD([sQuery(id+"F6.wireOp",EDGE,"E5.2.1.0")])],"isStart":false});
            var Q6;
            Q6=makeQuery(id+"F10.opExtrude","CAP_EDGE",EDGE,{"disambiguationData":[OSD([sQuery(id+"F6.wireOp",EDGE,"E4")])],"isStart":false});
            var Q7;
            Q7=makeQuery(id+"F10.opExtrude","CAP_EDGE",EDGE,{"disambiguationData":[OSD([sQuery(id+"F6.wireOp",EDGE,"E5.1.0.0")])],"isStart":false});
            var Q8;
            Q8=makeQuery(id+"F10.opExtrude","CAP_EDGE",EDGE,{"disambiguationData":[OSD([sQuery(id+"F6.wireOp",EDGE,"E5.2.0.0")])],"isStart":false});
            fillet(context, id + "F11", {"entities" : qUnion([Q0, Q1, Q2, Q3, Q4, Q5, Q6, Q7, Q8]), "radius" : 1 * mm, "tangentPropagation" : true, "allowEdgeOverflow" : false});
        }
        {
            var Q0;
            {var subQ0=sQuery(id+"F0.wireOp",EDGE,"E0.right");var subQ1=sQuery(id+"F0.wireOp",EDGE,"E0.bottom");Q0=makeQuery(id+"F3.boolean.opBoolean","MERGE",EDGE,{"derivedFrom":[makeQuery(id+"F1.opExtrude","SWEPT_EDGE",EDGE,{"disambiguationData":[OSD([subQ1,subQ0])]}),makeQuery(id+"F3.opExtrude","SWEPT_EDGE",EDGE,{"disambiguationData":[OSD([subQ1,subQ0])]})]});}
            var Q1;
            {var subQ0=sQuery(id+"F0.wireOp",EDGE,"E0.right");var subQ1=sQuery(id+"F0.wireOp",EDGE,"E0.top");Q1=makeQuery(id+"F3.boolean.opBoolean","MERGE",EDGE,{"derivedFrom":[makeQuery(id+"F1.opExtrude","SWEPT_EDGE",EDGE,{"disambiguationData":[OSD([subQ1,subQ0])]}),makeQuery(id+"F3.opExtrude","SWEPT_EDGE",EDGE,{"disambiguationData":[OSD([subQ1,subQ0])]})]});}
            var Q2;
            {var subQ0=sQuery(id+"F0.wireOp",EDGE,"E0.left");var subQ1=sQuery(id+"F0.wireOp",EDGE,"E0.top");Q2=makeQuery(id+"F3.boolean.opBoolean","MERGE",EDGE,{"derivedFrom":[makeQuery(id+"F1.opExtrude","SWEPT_EDGE",EDGE,{"disambiguationData":[OSD([subQ1,subQ0])]}),makeQuery(id+"F3.opExtrude","SWEPT_EDGE",EDGE,{"disambiguationData":[OSD([subQ1,subQ0])]})]});}
            var Q3;
            {var subQ0=sQuery(id+"F0.wireOp",EDGE,"E0.left");var subQ1=sQuery(id+"F0.wireOp",EDGE,"E0.bottom");Q3=makeQuery(id+"F3.boolean.opBoolean","MERGE",EDGE,{"derivedFrom":[makeQuery(id+"F1.opExtrude","SWEPT_EDGE",EDGE,{"disambiguationData":[OSD([subQ1,subQ0])]}),makeQuery(id+"F3.opExtrude","SWEPT_EDGE",EDGE,{"disambiguationData":[OSD([subQ1,subQ0])]})]});}
            fillet(context, id + "F12", {"entities" : qUnion([Q0, Q1, Q2, Q3]), "radius" : 10 * mm, "tangentPropagation" : true, "allowEdgeOverflow" : false});
        }
        {
            var Q0;
            Q0=makeQuery(id+"F1.opExtrude","CAP_FACE",FACE,{"disambiguationData":[OSD([sQuery(id+"F0.wireOp",EDGE,"E0.bottom"),sQuery(id+"F0.wireOp",EDGE,"E0.top"),sQuery(id+"F0.wireOp",EDGE,"E0.left"),sQuery(id+"F0.wireOp",EDGE,"E0.right")])],"isStart":true});
            fillet(context, id + "F13", {"entities" : qUnion([Q0]), "radius" : 3 * mm, "tangentPropagation" : true, "allowEdgeOverflow" : false});
        }
    });
